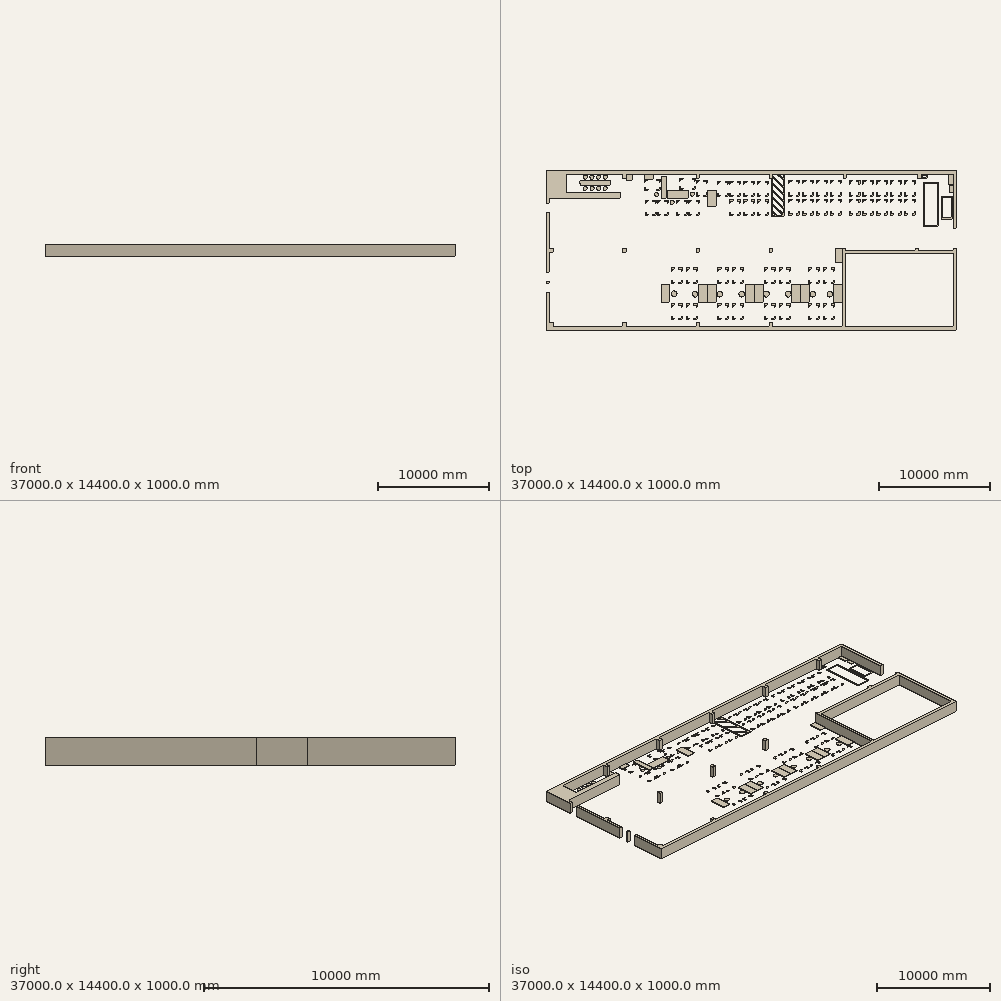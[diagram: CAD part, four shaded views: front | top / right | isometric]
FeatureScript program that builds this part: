
annotation { "Feature Type Name" : "Feature", "Feature Type Description" : "" }
export const myFeature = defineFeature(function(context is Context, id is Id, definition is map)
    precondition{}
    {
        {
            var Q0;
            Q0=qCreatedBy(makeId("Top.planeOp"),FACE);
            var sketch = newSketch(context, id + "F0", { "sketchPlane" : qUnion([Q0])});
            skLineSegment(sketch, "E0.bottom", {"start": v(-16600, 6700) * mm, "end": v(-16300, 6700) * mm});
            skLineSegment(sketch, "E0.top", {"start": v(-16600, 6300) * mm, "end": v(-16300, 6300) * mm});
            skLineSegment(sketch, "E0.left", {"start": v(-16600, 6700) * mm, "end": v(-16600, 6300) * mm});
            skLineSegment(sketch, "E0.right", {"start": v(-16300, 6700) * mm, "end": v(-16300, 6300) * mm});
            skLineSegment(sketch, "E1.1.0.0", {"start": v(-22900, 6700) * mm, "end": v(-22900, 6300) * mm});
            skLineSegment(sketch, "E1.1.0.1", {"start": v(-23200, 6700) * mm, "end": v(-23200, 6300) * mm});
            skLineSegment(sketch, "E1.1.0.2", {"start": v(-23200, 6700) * mm, "end": v(-22900, 6700) * mm});
            skLineSegment(sketch, "E1.1.0.3", {"start": v(-23200, 6300) * mm, "end": v(-22900, 6300) * mm});
            skLineSegment(sketch, "E1.2.0.0", {"start": v(-29500, 6700) * mm, "end": v(-29500, 6300) * mm});
            skLineSegment(sketch, "E1.2.0.1", {"start": v(-29800, 6700) * mm, "end": v(-29800, 6300) * mm});
            skLineSegment(sketch, "E1.2.0.2", {"start": v(-29800, 6700) * mm, "end": v(-29500, 6700) * mm});
            skLineSegment(sketch, "E1.2.0.3", {"start": v(-29800, 6300) * mm, "end": v(-29500, 6300) * mm});
            skLineSegment(sketch, "E1.3.0.0", {"start": v(-36100, 6700) * mm, "end": v(-36100, 6300) * mm});
            skLineSegment(sketch, "E1.3.0.1", {"start": v(-36400, 6700) * mm, "end": v(-36400, 6300) * mm});
            skLineSegment(sketch, "E1.3.0.2", {"start": v(-36400, 6700) * mm, "end": v(-36100, 6700) * mm});
            skLineSegment(sketch, "E1.3.0.3", {"start": v(-36400, 6300) * mm, "end": v(-36100, 6300) * mm});
            skLineSegment(sketch, "E2", {"start": v(-36400, 6700) * mm, "end": v(-36400, 9900) * mm});
            skLineSegment(sketch, "E3.left", {"start": v(-36400, 10700) * mm, "end": v(-36400, 11200) * mm});
            skLineSegment(sketch, "E4.0.1.0", {"start": v(-36400, -400) * mm, "end": v(-36100, -400) * mm});
            skLineSegment(sketch, "E4.0.1.1", {"start": v(-36400, 0) * mm, "end": v(-36400, -400) * mm});
            skLineSegment(sketch, "E4.0.1.2", {"start": v(-36400, 0) * mm, "end": v(-36100, 0) * mm});
            skLineSegment(sketch, "E4.0.1.3", {"start": v(-36100, 0) * mm, "end": v(-36100, -400) * mm});
            skLineSegment(sketch, "E4.0.1.4", {"start": v(-29800, 0) * mm, "end": v(-29500, 0) * mm});
            skLineSegment(sketch, "E4.0.1.5", {"start": v(-29800, 0) * mm, "end": v(-29800, -400) * mm});
            skLineSegment(sketch, "E4.0.1.6", {"start": v(-29800, -400) * mm, "end": v(-29500, -400) * mm});
            skLineSegment(sketch, "E4.0.1.7", {"start": v(-29500, 0) * mm, "end": v(-29500, -400) * mm});
            skLineSegment(sketch, "E4.0.1.8", {"start": v(-22900, 0) * mm, "end": v(-22900, -400) * mm});
            skLineSegment(sketch, "E4.0.1.9", {"start": v(-23200, 0) * mm, "end": v(-23200, -400) * mm});
            skLineSegment(sketch, "E4.0.1.10", {"start": v(-23200, 0) * mm, "end": v(-22900, 0) * mm});
            skLineSegment(sketch, "E4.0.1.11", {"start": v(-23200, -400) * mm, "end": v(-22900, -400) * mm});
            skLineSegment(sketch, "E4.0.1.12", {"start": v(-16600, 0) * mm, "end": v(-16300, 0) * mm});
            skLineSegment(sketch, "E4.0.1.13", {"start": v(-16600, -400) * mm, "end": v(-16300, -400) * mm});
            skLineSegment(sketch, "E4.0.1.14", {"start": v(-16600, 0) * mm, "end": v(-16600, -400) * mm});
            skLineSegment(sketch, "E4.0.1.15", {"start": v(-16300, 0) * mm, "end": v(-16300, -400) * mm});
            skLineSegment(sketch, "E5", {"start": v(-36400, -400) * mm, "end": v(0, -400) * mm});
            skLineSegment(sketch, "E6.bottom", {"start": v(0, -400) * mm, "end": v(-10000, -400) * mm});
            skLineSegment(sketch, "E6.left", {"start": v(0, -400) * mm, "end": v(0, 6300) * mm});
            skLineSegment(sketch, "E6.right", {"start": v(-10000, -400) * mm, "end": v(-10000, 6300) * mm});
            skLineSegment(sketch, "E7.0.1.0", {"start": v(-29800, 13400) * mm, "end": v(-29500, 13400) * mm});
            skLineSegment(sketch, "E7.0.1.1", {"start": v(-29800, 13400) * mm, "end": v(-29800, 13000) * mm});
            skLineSegment(sketch, "E7.0.1.2", {"start": v(-16600, 13000) * mm, "end": v(-16300, 13000) * mm});
            skLineSegment(sketch, "E7.0.1.3", {"start": v(-29800, 13000) * mm, "end": v(-29500, 13000) * mm});
            skLineSegment(sketch, "E7.0.1.4", {"start": v(-36100, 13400) * mm, "end": v(-36100, 13000) * mm});
            skLineSegment(sketch, "E7.0.1.5", {"start": v(-23200, 13000) * mm, "end": v(-22900, 13000) * mm});
            skLineSegment(sketch, "E7.0.1.6", {"start": v(-29500, 13400) * mm, "end": v(-29500, 13000) * mm});
            skLineSegment(sketch, "E7.0.1.7", {"start": v(-23200, 13400) * mm, "end": v(-22900, 13400) * mm});
            skLineSegment(sketch, "E7.0.1.8", {"start": v(-23200, 13400) * mm, "end": v(-23200, 13000) * mm});
            skLineSegment(sketch, "E7.0.1.9", {"start": v(-22900, 13400) * mm, "end": v(-22900, 13000) * mm});
            skLineSegment(sketch, "E7.0.1.10", {"start": v(-16300, 13400) * mm, "end": v(-16300, 13000) * mm});
            skLineSegment(sketch, "E7.0.1.11", {"start": v(-16600, 13400) * mm, "end": v(-16300, 13400) * mm});
            skLineSegment(sketch, "E7.0.1.12", {"start": v(-16600, 13400) * mm, "end": v(-16600, 13000) * mm});
            skLineSegment(sketch, "E7.0.1.13", {"start": v(-36400, 13400) * mm, "end": v(-36100, 13400) * mm});
            skLineSegment(sketch, "E7.0.1.14", {"start": v(-36400, 13400) * mm, "end": v(-36400, 13000) * mm});
            skLineSegment(sketch, "E7.0.1.16", {"start": v(-36400, 13000) * mm, "end": v(-36100, 13000) * mm});
            skLineSegment(sketch, "E8.bottom", {"start": v(-36400, 13400) * mm, "end": v(-34900, 13400) * mm});
            skLineSegment(sketch, "E8.top", {"start": v(-36400, 11200) * mm, "end": v(-34900, 11200) * mm});
            skLineSegment(sketch, "E8.left", {"start": v(-36400, 13400) * mm, "end": v(-36400, 11200) * mm});
            skLineSegment(sketch, "E8.right", {"start": v(-34900, 13400) * mm, "end": v(-34900, 11200) * mm});
            skLineSegment(sketch, "E9.bottom", {"start": v(-34900, 11200) * mm, "end": v(-30000, 11200) * mm});
            skLineSegment(sketch, "E9.top", {"start": v(-34900, 11700) * mm, "end": v(-30000, 11700) * mm});
            skLineSegment(sketch, "E9.left", {"start": v(-34900, 11200) * mm, "end": v(-34900, 11700) * mm});
            skLineSegment(sketch, "E9.right", {"start": v(-30000, 11200) * mm, "end": v(-30000, 11700) * mm});
            skLineSegment(sketch, "E10", {"start": v(-34900, 13400) * mm, "end": v(0, 13400) * mm});
            skLineSegment(sketch, "E11", {"start": v(0, 13400) * mm, "end": v(0, 8500) * mm});
            skLineSegment(sketch, "E12.1.0.0", {"start": v(-9600, 13400) * mm, "end": v(-9600, 13000) * mm});
            skLineSegment(sketch, "E12.1.0.1", {"start": v(-9900, 13000) * mm, "end": v(-9600, 13000) * mm});
            skLineSegment(sketch, "E12.1.0.2", {"start": v(-9900, 13400) * mm, "end": v(-9900, 13000) * mm});
            skLineSegment(sketch, "E12.1.0.3", {"start": v(-9900, 13400) * mm, "end": v(-9600, 13400) * mm});
            skLineSegment(sketch, "E12.2.0.0", {"start": v(-2900, 13400) * mm, "end": v(-2900, 13000) * mm});
            skLineSegment(sketch, "E12.2.0.1", {"start": v(-3200, 13000) * mm, "end": v(-2900, 13000) * mm});
            skLineSegment(sketch, "E12.2.0.2", {"start": v(-3200, 13400) * mm, "end": v(-3200, 13000) * mm});
            skLineSegment(sketch, "E12.2.0.3", {"start": v(-3200, 13400) * mm, "end": v(-2900, 13400) * mm});
            skLineSegment(sketch, "E13", {"start": v(-36400, 6300) * mm, "end": v(-36400, 4500) * mm});
            skLineSegment(sketch, "E14", {"start": v(-36400, 3700) * mm, "end": v(-36400, 3500) * mm});
            skLineSegment(sketch, "E15", {"start": v(-36400, 0) * mm, "end": v(-36400, 2700) * mm});
            skLineSegment(sketch, "E16.1.0.0", {"start": v(-10000, 6700) * mm, "end": v(-10000, 6300) * mm});
            skLineSegment(sketch, "E16.1.0.1", {"start": v(-10000, 6700) * mm, "end": v(-9700, 6700) * mm});
            skLineSegment(sketch, "E16.1.0.2", {"start": v(-9700, 6700) * mm, "end": v(-9700, 6300) * mm});
            skLineSegment(sketch, "E16.1.0.3", {"start": v(-10000, 6300) * mm, "end": v(-9700, 6300) * mm});
            skLineSegment(sketch, "E16.2.0.0", {"start": v(-3400, 6700) * mm, "end": v(-3400, 6300) * mm});
            skLineSegment(sketch, "E16.2.0.1", {"start": v(-3400, 6700) * mm, "end": v(-3100, 6700) * mm});
            skLineSegment(sketch, "E16.2.0.2", {"start": v(-3100, 6700) * mm, "end": v(-3100, 6300) * mm});
            skLineSegment(sketch, "E16.2.0.3", {"start": v(-3400, 6300) * mm, "end": v(-3100, 6300) * mm});
            skLineSegment(sketch, "E17.0", {"start": v(-36700, 13700) * mm, "end": v(300, 13700) * mm});
            skLineSegment(sketch, "E18", {"start": v(-36700, 13700) * mm, "end": v(-36700, 10700) * mm});
            skLineSegment(sketch, "E19", {"start": v(-36700, 10700) * mm, "end": v(-36400, 10700) * mm});
            skLineSegment(sketch, "E20", {"start": v(-36400, 9900) * mm, "end": v(-36700, 9900) * mm});
            skLineSegment(sketch, "E21", {"start": v(-36700, 9900) * mm, "end": v(-36700, 4500) * mm});
            skLineSegment(sketch, "E22", {"start": v(-36400, 3700) * mm, "end": v(-36700, 3700) * mm});
            skLineSegment(sketch, "E23", {"start": v(-36700, 3700) * mm, "end": v(-36700, 3500) * mm});
            skLineSegment(sketch, "E24", {"start": v(-36700, 3500) * mm, "end": v(-36400, 3500) * mm});
            skLineSegment(sketch, "E25", {"start": v(-36400, 2700) * mm, "end": v(-36700, 2700) * mm});
            skLineSegment(sketch, "E26", {"start": v(-36700, 2700) * mm, "end": v(-36700, -700) * mm});
            skLineSegment(sketch, "E27", {"start": v(-36700, -700) * mm, "end": v(300, -700) * mm});
            skLineSegment(sketch, "E28", {"start": v(300, -700) * mm, "end": v(300, 6300) * mm});
            skLineSegment(sketch, "E29", {"start": v(-36700, 4500) * mm, "end": v(-36400, 4500) * mm});
            skLineSegment(sketch, "E30", {"start": v(300, 13700) * mm, "end": v(300, 8500) * mm});
            skLineSegment(sketch, "E31", {"start": v(0, 8500) * mm, "end": v(300, 8500) * mm});
            skLineSegment(sketch, "E32.top", {"start": v(0, 6700) * mm, "end": v(300, 6700) * mm});
            skLineSegment(sketch, "E32.left", {"start": v(0, 6300) * mm, "end": v(0, 6700) * mm});
            skLineSegment(sketch, "E32.right", {"start": v(300, 6300) * mm, "end": v(300, 6700) * mm});
            skLineSegment(sketch, "E33", {"start": v(-9700, -400) * mm, "end": v(-9700, 6200) * mm});
            skLineSegment(sketch, "E34", {"start": v(-9700, 6200) * mm, "end": v(0, 6200) * mm});
            skLineSegment(sketch, "E35", {"start": v(-9700, 6500) * mm, "end": v(-3400, 6500) * mm});
            skLineSegment(sketch, "E36", {"start": v(-3100, 6500) * mm, "end": v(0, 6500) * mm});
            skSolve(sketch);
        }
        {
            var Q0;
            {var subQ0=sQuery(id+"F0.wireOp",EDGE,"E7.0.1.4");Q0=makeQuery(id+"F0.imprint","IMPRINT",FACE,{"disambiguationData":[TD([[makeQuery(id+"F0.imprint","IMPRINT",EDGE,{"derivedFrom":subQ0}),-1.0]])]});}
            var Q1;
            {var subQ1=sQuery(id+"F0.wireOp",EDGE,"E7.0.1.4");Q1=makeQuery(id+"F0.imprint","IMPRINT",FACE,{"disambiguationData":[TD([[makeQuery(id+"F0.imprint","IMPRINT",EDGE,{"derivedFrom":subQ1}),1.0]])]});}
            var Q2;
            Q2=makeQuery(id+"F0.imprint","IMPRINT",FACE,{"disambiguationData":[TD([[makeQuery(id+"F0.imprint","IMPRINT",EDGE,{"derivedFrom":sQuery(id+"F0.wireOp",EDGE,"E9.bottom")}),1.0]])]});
            var Q3;
            {var subQ0=sQuery(id+"F0.wireOp",EDGE,"E7.0.1.1");Q3=makeQuery(id+"F0.imprint","IMPRINT",FACE,{"disambiguationData":[TD([[makeQuery(id+"F0.imprint","IMPRINT",EDGE,{"derivedFrom":subQ0}),1.0]])]});}
            var Q4;
            Q4=makeQuery(id+"F0.imprint","IMPRINT",FACE,{"disambiguationData":[TD([[makeQuery(id+"F0.imprint","IMPRINT",EDGE,{"derivedFrom":sQuery(id+"F0.wireOp",EDGE,"E7.0.1.5")}),1.0]])]});
            var Q5;
            Q5=makeQuery(id+"F0.imprint","IMPRINT",FACE,{"disambiguationData":[TD([[makeQuery(id+"F0.imprint","IMPRINT",EDGE,{"derivedFrom":sQuery(id+"F0.wireOp",EDGE,"E1.1.0.0")}),-1.0]])]});
            var Q6;
            Q6=makeQuery(id+"F0.imprint","IMPRINT",FACE,{"disambiguationData":[TD([[makeQuery(id+"F0.imprint","IMPRINT",EDGE,{"derivedFrom":sQuery(id+"F0.wireOp",EDGE,"E1.2.0.0")}),-1.0]])]});
            var Q7;
            Q7=makeQuery(id+"F0.imprint","IMPRINT",FACE,{"disambiguationData":[TD([[makeQuery(id+"F0.imprint","IMPRINT",EDGE,{"derivedFrom":sQuery(id+"F0.wireOp",EDGE,"E1.3.0.0")}),-1.0]])]});
            var Q8;
            Q8=makeQuery(id+"F0.imprint","IMPRINT",FACE,{"disambiguationData":[TD([[makeQuery(id+"F0.imprint","IMPRINT",EDGE,{"derivedFrom":sQuery(id+"F0.wireOp",EDGE,"E7.0.1.2")}),1.0]])]});
            var Q9;
            Q9=makeQuery(id+"F0.imprint","IMPRINT",FACE,{"disambiguationData":[TD([[makeQuery(id+"F0.imprint","IMPRINT",EDGE,{"derivedFrom":sQuery(id+"F0.wireOp",EDGE,"E0.bottom")}),-1.0]])]});
            var Q10;
            Q10=makeQuery(id+"F0.imprint","IMPRINT",FACE,{"disambiguationData":[TD([[makeQuery(id+"F0.imprint","IMPRINT",EDGE,{"derivedFrom":sQuery(id+"F0.wireOp",EDGE,"E16.1.0.0")}),1.0]])]});
            var Q11;
            Q11=makeQuery(id+"F0.imprint","IMPRINT",FACE,{"disambiguationData":[TD([[makeQuery(id+"F0.imprint","IMPRINT",EDGE,{"derivedFrom":sQuery(id+"F0.wireOp",EDGE,"E12.1.0.0")}),-1.0]])]});
            var Q12;
            Q12=makeQuery(id+"F0.imprint","IMPRINT",FACE,{"disambiguationData":[TD([[makeQuery(id+"F0.imprint","IMPRINT",EDGE,{"derivedFrom":sQuery(id+"F0.wireOp",EDGE,"E12.2.0.0")}),-1.0]])]});
            var Q13;
            Q13=makeQuery(id+"F0.imprint","IMPRINT",FACE,{"disambiguationData":[TD([[makeQuery(id+"F0.imprint","IMPRINT",EDGE,{"derivedFrom":sQuery(id+"F0.wireOp",EDGE,"E16.2.0.0")}),1.0]])]});
            var Q14;
            Q14=makeQuery(id+"F0.imprint","IMPRINT",FACE,{"disambiguationData":[TD([[makeQuery(id+"F0.imprint","IMPRINT",EDGE,{"derivedFrom":sQuery(id+"F0.wireOp",EDGE,"E4.0.1.12")}),-1.0]])]});
            var Q15;
            {var subQ0=sQuery(id+"F0.wireOp",EDGE,"E4.0.1.8");Q15=makeQuery(id+"F0.imprint","IMPRINT",FACE,{"disambiguationData":[TD([[makeQuery(id+"F0.imprint","IMPRINT",EDGE,{"derivedFrom":subQ0}),-1.0]])]});}
            var Q16;
            Q16=makeQuery(id+"F0.imprint","IMPRINT",FACE,{"disambiguationData":[TD([[makeQuery(id+"F0.imprint","IMPRINT",EDGE,{"derivedFrom":sQuery(id+"F0.wireOp",EDGE,"E4.0.1.4")}),-1.0]])]});
            var Q17;
            {var subQ0=sQuery(id+"F0.wireOp",EDGE,"E4.0.1.1");Q17=makeQuery(id+"F0.imprint","IMPRINT",FACE,{"disambiguationData":[TD([[makeQuery(id+"F0.imprint","IMPRINT",EDGE,{"derivedFrom":subQ0}),1.0]])]});}
            var Q18;
            Q18=makeQuery(id+"F0.imprint","IMPRINT",FACE,{"disambiguationData":[TD([[makeQuery(id+"F0.imprint","IMPRINT",EDGE,{"derivedFrom":sQuery(id+"F0.wireOp",EDGE,"E1.3.0.1")}),-1.0]])]});
            var Q19;
            {var subQ7=sQuery(id+"F0.wireOp",EDGE,"E3.left");Q19=makeQuery(id+"F0.imprint","IMPRINT",FACE,{"disambiguationData":[TD([[makeQuery(id+"F0.imprint","IMPRINT",EDGE,{"derivedFrom":subQ7}),1.0]])]});}
            var Q20;
            {var subQ7=sQuery(id+"F0.wireOp",EDGE,"E4.0.1.1");Q20=makeQuery(id+"F0.imprint","IMPRINT",FACE,{"disambiguationData":[TD([[makeQuery(id+"F0.imprint","IMPRINT",EDGE,{"derivedFrom":subQ7}),-1.0]])]});}
            var Q21;
            Q21=makeQuery(id+"F0.imprint","IMPRINT",FACE,{"disambiguationData":[TD([[makeQuery(id+"F0.imprint","IMPRINT",EDGE,{"derivedFrom":sQuery(id+"F0.wireOp",EDGE,"E14")}),-1.0]])]});
            var Q22;
            {var subQ10=sQuery(id+"F0.wireOp",EDGE,"E6.right");Q22=makeQuery(id+"F0.imprint","IMPRINT",FACE,{"disambiguationData":[TD([[makeQuery(id+"F0.imprint","IMPRINT",EDGE,{"derivedFrom":subQ10}),-1.0]])]});}
            extrude(context, id + "F1", {"entities" : qUnion([Q0, Q1, Q2, Q3, Q4, Q5, Q6, Q7, Q8, Q9, Q10, Q11, Q12, Q13, Q14, Q15, Q16, Q17, Q18, Q19, Q20, Q21, Q22]), "depth" : 1000 * mm});
        }
        {
            var Q0;
            Q0=qCreatedBy(makeId("Top.planeOp"),FACE);
            var sketch = newSketch(context, id + "F2", { "sketchPlane" : qUnion([Q0])});
            skLineSegment(sketch, "E37.0.1.0", {"start": v(-4400, 12800) * mm, "end": v(-4400, 12500) * mm});
            skLineSegment(sketch, "E37.0.1.1", {"start": v(-4400, 12800) * mm, "end": v(-4100, 12800) * mm});
            skLineSegment(sketch, "E37.0.1.2", {"start": v(-4400, 11400) * mm, "end": v(-4100, 11400) * mm});
            skLineSegment(sketch, "E37.0.1.3", {"start": v(-3400, 12800) * mm, "end": v(-3400, 12500) * mm});
            skLineSegment(sketch, "E38.bottom", {"start": v(-400, 13400.06) * mm, "end": v(0, 13400.06) * mm});
            skLineSegment(sketch, "E38.top", {"start": v(-400, 12500.06) * mm, "end": v(0, 12500.06) * mm});
            skLineSegment(sketch, "E38.left", {"start": v(-400, 13400.06) * mm, "end": v(-400, 12500.06) * mm});
            skLineSegment(sketch, "E38.right", {"start": v(0, 13400.06) * mm, "end": v(0, 12500.06) * mm});
            skLineSegment(sketch, "E39.bottom", {"start": v(-2691.77, 12623.56) * mm, "end": v(-1291.77, 12623.56) * mm});
            skLineSegment(sketch, "E39.top", {"start": v(-2691.77, 8623.56) * mm, "end": v(-1291.77, 8623.56) * mm});
            skLineSegment(sketch, "E39.left", {"start": v(-2691.77, 12623.56) * mm, "end": v(-2691.77, 8623.56) * mm});
            skLineSegment(sketch, "E39.right", {"start": v(-1291.77, 12623.56) * mm, "end": v(-1291.77, 8623.56) * mm});
            skLineSegment(sketch, "E40.bottom", {"start": v(-1078.64, 11342.13) * mm, "end": v(-78.64, 11342.13) * mm});
            skLineSegment(sketch, "E40.top", {"start": v(-1078.64, 9342.13) * mm, "end": v(-78.64, 9342.13) * mm});
            skLineSegment(sketch, "E40.left", {"start": v(-1078.64, 11342.13) * mm, "end": v(-1078.64, 9342.13) * mm});
            skLineSegment(sketch, "E40.right", {"start": v(-78.64, 11342.13) * mm, "end": v(-78.64, 9342.13) * mm});
            skLineSegment(sketch, "E41.bottom", {"start": v(0, 12322.67) * mm, "end": v(-373.68, 12322.67) * mm});
            skLineSegment(sketch, "E41.top", {"start": v(0, 11732.57) * mm, "end": v(-373.68, 11732.57) * mm});
            skLineSegment(sketch, "E41.left", {"start": v(0, 12322.67) * mm, "end": v(0, 11732.57) * mm});
            skLineSegment(sketch, "E41.right", {"start": v(-373.68, 12322.67) * mm, "end": v(-373.68, 11732.57) * mm});
            skLineSegment(sketch, "E42.bottom", {"start": v(-2890.64, 13380.12) * mm, "end": v(-2300.62, 13380.12) * mm});
            skLineSegment(sketch, "E42.top", {"start": v(-2890.64, 12992.25) * mm, "end": v(-2300.62, 12992.25) * mm});
            skLineSegment(sketch, "E42.left", {"start": v(-2890.64, 13380.12) * mm, "end": v(-2890.64, 12992.25) * mm});
            skLineSegment(sketch, "E42.right", {"start": v(-2300.62, 13380.12) * mm, "end": v(-2300.62, 12992.25) * mm});
            skLineSegment(sketch, "E43.bottom", {"start": v(-16279.42, 13380.32) * mm, "end": v(-15279.42, 13380.32) * mm});
            skLineSegment(sketch, "E43.top", {"start": v(-16279.42, 9680.32) * mm, "end": v(-15279.42, 9680.32) * mm});
            skLineSegment(sketch, "E43.left", {"start": v(-16279.42, 13380.32) * mm, "end": v(-16279.42, 9680.32) * mm});
            skLineSegment(sketch, "E43.right", {"start": v(-15279.42, 13380.32) * mm, "end": v(-15279.42, 9680.32) * mm});
            skLineSegment(sketch, "E44", {"start": v(-4400, 12500) * mm, "end": v(-4300, 12500) * mm});
            skLineSegment(sketch, "E45", {"start": v(-4300, 12500) * mm, "end": v(-4300, 12700) * mm});
            skLineSegment(sketch, "E46", {"start": v(-4300, 12700) * mm, "end": v(-4100, 12700) * mm});
            skLineSegment(sketch, "E47", {"start": v(-4100, 12700) * mm, "end": v(-4100, 12800) * mm});
            skLineSegment(sketch, "E48.MirrorCS", {"start": v(-3700, 12700) * mm, "end": v(-3700, 12800) * mm});
            skLineSegment(sketch, "E49.MirrorCS", {"start": v(-3500, 12700) * mm, "end": v(-3700, 12700) * mm});
            skLineSegment(sketch, "E50.MirrorCS", {"start": v(-3500, 12500) * mm, "end": v(-3500, 12700) * mm});
            skLineSegment(sketch, "E51.MirrorCS", {"start": v(-3400, 12500) * mm, "end": v(-3500, 12500) * mm});
            skLineSegment(sketch, "E52.MirrorCS", {"start": v(-4400, 11700) * mm, "end": v(-4300, 11700) * mm});
            skLineSegment(sketch, "E53.MirrorCS", {"start": v(-4300, 11700) * mm, "end": v(-4300, 11500) * mm});
            skLineSegment(sketch, "E54.MirrorCS", {"start": v(-4300, 11500) * mm, "end": v(-4100, 11500) * mm});
            skLineSegment(sketch, "E55.MirrorCS", {"start": v(-4100, 11500) * mm, "end": v(-4100, 11400) * mm});
            skLineSegment(sketch, "E56.MirrorCS", {"start": v(-3700, 11500) * mm, "end": v(-3700, 11400) * mm});
            skLineSegment(sketch, "E57.MirrorCS", {"start": v(-3500, 11500) * mm, "end": v(-3700, 11500) * mm});
            skLineSegment(sketch, "E58.MirrorCS", {"start": v(-3500, 11700) * mm, "end": v(-3500, 11500) * mm});
            skLineSegment(sketch, "E59.MirrorCS", {"start": v(-3400, 11700) * mm, "end": v(-3500, 11700) * mm});
            skLineSegment(sketch, "E60.trimOffspring", {"start": v(-4400, 11700) * mm, "end": v(-4400, 11400) * mm});
            skLineSegment(sketch, "E61.trimOffspring", {"start": v(-3700, 12800) * mm, "end": v(-3400, 12800) * mm});
            skLineSegment(sketch, "E62.trimOffspring", {"start": v(-3400, 11700) * mm, "end": v(-3400, 11400) * mm});
            skLineSegment(sketch, "E63.trimOffspring", {"start": v(-3700, 11400) * mm, "end": v(-3400, 11400) * mm});
            skLineSegment(sketch, "E64.0.1.0", {"start": v(-3700, 11100) * mm, "end": v(-3400, 11100) * mm});
            skLineSegment(sketch, "E64.0.1.1", {"start": v(-3700, 9700) * mm, "end": v(-3400, 9700) * mm});
            skLineSegment(sketch, "E64.0.1.2", {"start": v(-4400, 10000) * mm, "end": v(-4400, 9700) * mm});
            skLineSegment(sketch, "E64.0.1.3", {"start": v(-4400, 9700) * mm, "end": v(-4100, 9700) * mm});
            skLineSegment(sketch, "E64.0.1.4", {"start": v(-3400, 10000) * mm, "end": v(-3400, 9700) * mm});
            skLineSegment(sketch, "E64.0.1.5", {"start": v(-3400, 11100) * mm, "end": v(-3400, 10800) * mm});
            skLineSegment(sketch, "E64.0.1.6", {"start": v(-4400, 11100) * mm, "end": v(-4400, 10800) * mm});
            skLineSegment(sketch, "E64.0.1.7", {"start": v(-4400, 11100) * mm, "end": v(-4100, 11100) * mm});
            skLineSegment(sketch, "E64.0.1.8", {"start": v(-4300, 9800) * mm, "end": v(-4100, 9800) * mm});
            skLineSegment(sketch, "E64.0.1.9", {"start": v(-3400, 10000) * mm, "end": v(-3500, 10000) * mm});
            skLineSegment(sketch, "E64.0.1.10", {"start": v(-3700, 9800) * mm, "end": v(-3700, 9700) * mm});
            skLineSegment(sketch, "E64.0.1.11", {"start": v(-3500, 11000) * mm, "end": v(-3700, 11000) * mm});
            skLineSegment(sketch, "E64.0.1.12", {"start": v(-4400, 10800) * mm, "end": v(-4300, 10800) * mm});
            skLineSegment(sketch, "E64.0.1.13", {"start": v(-4300, 11000) * mm, "end": v(-4100, 11000) * mm});
            skLineSegment(sketch, "E64.0.1.14", {"start": v(-4400, 10000) * mm, "end": v(-4300, 10000) * mm});
            skLineSegment(sketch, "E64.0.1.15", {"start": v(-3700, 11000) * mm, "end": v(-3700, 11100) * mm});
            skLineSegment(sketch, "E64.0.1.16", {"start": v(-4100, 9800) * mm, "end": v(-4100, 9700) * mm});
            skLineSegment(sketch, "E64.0.1.17", {"start": v(-4300, 10000) * mm, "end": v(-4300, 9800) * mm});
            skLineSegment(sketch, "E64.0.1.18", {"start": v(-4300, 10800) * mm, "end": v(-4300, 11000) * mm});
            skLineSegment(sketch, "E64.0.1.19", {"start": v(-3500, 9800) * mm, "end": v(-3700, 9800) * mm});
            skLineSegment(sketch, "E64.0.1.20", {"start": v(-4100, 11000) * mm, "end": v(-4100, 11100) * mm});
            skLineSegment(sketch, "E64.0.1.21", {"start": v(-3400, 10800) * mm, "end": v(-3500, 10800) * mm});
            skLineSegment(sketch, "E64.0.1.22", {"start": v(-3500, 10000) * mm, "end": v(-3500, 9800) * mm});
            skLineSegment(sketch, "E64.0.1.23", {"start": v(-3500, 10800) * mm, "end": v(-3500, 11000) * mm});
            skLineSegment(sketch, "E64.1.0.0", {"start": v(-4950, 12800) * mm, "end": v(-4650, 12800) * mm});
            skLineSegment(sketch, "E64.1.0.1", {"start": v(-4950, 11400) * mm, "end": v(-4650, 11400) * mm});
            skLineSegment(sketch, "E64.1.0.2", {"start": v(-5650, 11700) * mm, "end": v(-5650, 11400) * mm});
            skLineSegment(sketch, "E64.1.0.3", {"start": v(-5650, 11400) * mm, "end": v(-5350, 11400) * mm});
            skLineSegment(sketch, "E64.1.0.4", {"start": v(-4650, 11700) * mm, "end": v(-4650, 11400) * mm});
            skLineSegment(sketch, "E64.1.0.5", {"start": v(-4650, 12800) * mm, "end": v(-4650, 12500) * mm});
            skLineSegment(sketch, "E64.1.0.6", {"start": v(-5650, 12800) * mm, "end": v(-5650, 12500) * mm});
            skLineSegment(sketch, "E64.1.0.7", {"start": v(-5650, 12800) * mm, "end": v(-5350, 12800) * mm});
            skLineSegment(sketch, "E64.1.0.8", {"start": v(-5550, 11500) * mm, "end": v(-5350, 11500) * mm});
            skLineSegment(sketch, "E64.1.0.9", {"start": v(-4650, 11700) * mm, "end": v(-4750, 11700) * mm});
            skLineSegment(sketch, "E64.1.0.10", {"start": v(-4950, 11500) * mm, "end": v(-4950, 11400) * mm});
            skLineSegment(sketch, "E64.1.0.11", {"start": v(-4750, 12700) * mm, "end": v(-4950, 12700) * mm});
            skLineSegment(sketch, "E64.1.0.12", {"start": v(-5650, 12500) * mm, "end": v(-5550, 12500) * mm});
            skLineSegment(sketch, "E64.1.0.13", {"start": v(-5550, 12700) * mm, "end": v(-5350, 12700) * mm});
            skLineSegment(sketch, "E64.1.0.14", {"start": v(-5650, 11700) * mm, "end": v(-5550, 11700) * mm});
            skLineSegment(sketch, "E64.1.0.15", {"start": v(-4950, 12700) * mm, "end": v(-4950, 12800) * mm});
            skLineSegment(sketch, "E64.1.0.16", {"start": v(-5350, 11500) * mm, "end": v(-5350, 11400) * mm});
            skLineSegment(sketch, "E64.1.0.17", {"start": v(-5550, 11700) * mm, "end": v(-5550, 11500) * mm});
            skLineSegment(sketch, "E64.1.0.18", {"start": v(-5550, 12500) * mm, "end": v(-5550, 12700) * mm});
            skLineSegment(sketch, "E64.1.0.19", {"start": v(-4750, 11500) * mm, "end": v(-4950, 11500) * mm});
            skLineSegment(sketch, "E64.1.0.20", {"start": v(-5350, 12700) * mm, "end": v(-5350, 12800) * mm});
            skLineSegment(sketch, "E64.1.0.21", {"start": v(-4650, 12500) * mm, "end": v(-4750, 12500) * mm});
            skLineSegment(sketch, "E64.1.0.22", {"start": v(-4750, 11700) * mm, "end": v(-4750, 11500) * mm});
            skLineSegment(sketch, "E64.1.0.23", {"start": v(-4750, 12500) * mm, "end": v(-4750, 12700) * mm});
            skLineSegment(sketch, "E64.1.1.0", {"start": v(-4950, 11100) * mm, "end": v(-4650, 11100) * mm});
            skLineSegment(sketch, "E64.1.1.1", {"start": v(-4950, 9700) * mm, "end": v(-4650, 9700) * mm});
            skLineSegment(sketch, "E64.1.1.2", {"start": v(-5650, 10000) * mm, "end": v(-5650, 9700) * mm});
            skLineSegment(sketch, "E64.1.1.3", {"start": v(-5650, 9700) * mm, "end": v(-5350, 9700) * mm});
            skLineSegment(sketch, "E64.1.1.4", {"start": v(-4650, 10000) * mm, "end": v(-4650, 9700) * mm});
            skLineSegment(sketch, "E64.1.1.5", {"start": v(-4650, 11100) * mm, "end": v(-4650, 10800) * mm});
            skLineSegment(sketch, "E64.1.1.6", {"start": v(-5650, 11100) * mm, "end": v(-5650, 10800) * mm});
            skLineSegment(sketch, "E64.1.1.7", {"start": v(-5650, 11100) * mm, "end": v(-5350, 11100) * mm});
            skLineSegment(sketch, "E64.1.1.8", {"start": v(-5550, 9800) * mm, "end": v(-5350, 9800) * mm});
            skLineSegment(sketch, "E64.1.1.9", {"start": v(-4650, 10000) * mm, "end": v(-4750, 10000) * mm});
            skLineSegment(sketch, "E64.1.1.10", {"start": v(-4950, 9800) * mm, "end": v(-4950, 9700) * mm});
            skLineSegment(sketch, "E64.1.1.11", {"start": v(-4750, 11000) * mm, "end": v(-4950, 11000) * mm});
            skLineSegment(sketch, "E64.1.1.12", {"start": v(-5650, 10800) * mm, "end": v(-5550, 10800) * mm});
            skLineSegment(sketch, "E64.1.1.13", {"start": v(-5550, 11000) * mm, "end": v(-5350, 11000) * mm});
            skLineSegment(sketch, "E64.1.1.14", {"start": v(-5650, 10000) * mm, "end": v(-5550, 10000) * mm});
            skLineSegment(sketch, "E64.1.1.15", {"start": v(-4950, 11000) * mm, "end": v(-4950, 11100) * mm});
            skLineSegment(sketch, "E64.1.1.16", {"start": v(-5350, 9800) * mm, "end": v(-5350, 9700) * mm});
            skLineSegment(sketch, "E64.1.1.17", {"start": v(-5550, 10000) * mm, "end": v(-5550, 9800) * mm});
            skLineSegment(sketch, "E64.1.1.18", {"start": v(-5550, 10800) * mm, "end": v(-5550, 11000) * mm});
            skLineSegment(sketch, "E64.1.1.19", {"start": v(-4750, 9800) * mm, "end": v(-4950, 9800) * mm});
            skLineSegment(sketch, "E64.1.1.20", {"start": v(-5350, 11000) * mm, "end": v(-5350, 11100) * mm});
            skLineSegment(sketch, "E64.1.1.21", {"start": v(-4650, 10800) * mm, "end": v(-4750, 10800) * mm});
            skLineSegment(sketch, "E64.1.1.22", {"start": v(-4750, 10000) * mm, "end": v(-4750, 9800) * mm});
            skLineSegment(sketch, "E64.1.1.23", {"start": v(-4750, 10800) * mm, "end": v(-4750, 11000) * mm});
            skLineSegment(sketch, "E64.2.0.0", {"start": v(-6200, 12800) * mm, "end": v(-5900, 12800) * mm});
            skLineSegment(sketch, "E64.2.0.1", {"start": v(-6200, 11400) * mm, "end": v(-5900, 11400) * mm});
            skLineSegment(sketch, "E64.2.0.2", {"start": v(-6900, 11700) * mm, "end": v(-6900, 11400) * mm});
            skLineSegment(sketch, "E64.2.0.3", {"start": v(-6900, 11400) * mm, "end": v(-6600, 11400) * mm});
            skLineSegment(sketch, "E64.2.0.4", {"start": v(-5900, 11700) * mm, "end": v(-5900, 11400) * mm});
            skLineSegment(sketch, "E64.2.0.5", {"start": v(-5900, 12800) * mm, "end": v(-5900, 12500) * mm});
            skLineSegment(sketch, "E64.2.0.6", {"start": v(-6900, 12800) * mm, "end": v(-6900, 12500) * mm});
            skLineSegment(sketch, "E64.2.0.7", {"start": v(-6900, 12800) * mm, "end": v(-6600, 12800) * mm});
            skLineSegment(sketch, "E64.2.0.8", {"start": v(-6800, 11500) * mm, "end": v(-6600, 11500) * mm});
            skLineSegment(sketch, "E64.2.0.9", {"start": v(-5900, 11700) * mm, "end": v(-6000, 11700) * mm});
            skLineSegment(sketch, "E64.2.0.10", {"start": v(-6200, 11500) * mm, "end": v(-6200, 11400) * mm});
            skLineSegment(sketch, "E64.2.0.11", {"start": v(-6000, 12700) * mm, "end": v(-6200, 12700) * mm});
            skLineSegment(sketch, "E64.2.0.12", {"start": v(-6900, 12500) * mm, "end": v(-6800, 12500) * mm});
            skLineSegment(sketch, "E64.2.0.13", {"start": v(-6800, 12700) * mm, "end": v(-6600, 12700) * mm});
            skLineSegment(sketch, "E64.2.0.14", {"start": v(-6900, 11700) * mm, "end": v(-6800, 11700) * mm});
            skLineSegment(sketch, "E64.2.0.15", {"start": v(-6200, 12700) * mm, "end": v(-6200, 12800) * mm});
            skLineSegment(sketch, "E64.2.0.16", {"start": v(-6600, 11500) * mm, "end": v(-6600, 11400) * mm});
            skLineSegment(sketch, "E64.2.0.17", {"start": v(-6800, 11700) * mm, "end": v(-6800, 11500) * mm});
            skLineSegment(sketch, "E64.2.0.18", {"start": v(-6800, 12500) * mm, "end": v(-6800, 12700) * mm});
            skLineSegment(sketch, "E64.2.0.19", {"start": v(-6000, 11500) * mm, "end": v(-6200, 11500) * mm});
            skLineSegment(sketch, "E64.2.0.20", {"start": v(-6600, 12700) * mm, "end": v(-6600, 12800) * mm});
            skLineSegment(sketch, "E64.2.0.21", {"start": v(-5900, 12500) * mm, "end": v(-6000, 12500) * mm});
            skLineSegment(sketch, "E64.2.0.22", {"start": v(-6000, 11700) * mm, "end": v(-6000, 11500) * mm});
            skLineSegment(sketch, "E64.2.0.23", {"start": v(-6000, 12500) * mm, "end": v(-6000, 12700) * mm});
            skLineSegment(sketch, "E64.2.1.0", {"start": v(-6200, 11100) * mm, "end": v(-5900, 11100) * mm});
            skLineSegment(sketch, "E64.2.1.1", {"start": v(-6200, 9700) * mm, "end": v(-5900, 9700) * mm});
            skLineSegment(sketch, "E64.2.1.2", {"start": v(-6900, 10000) * mm, "end": v(-6900, 9700) * mm});
            skLineSegment(sketch, "E64.2.1.3", {"start": v(-6900, 9700) * mm, "end": v(-6600, 9700) * mm});
            skLineSegment(sketch, "E64.2.1.4", {"start": v(-5900, 10000) * mm, "end": v(-5900, 9700) * mm});
            skLineSegment(sketch, "E64.2.1.5", {"start": v(-5900, 11100) * mm, "end": v(-5900, 10800) * mm});
            skLineSegment(sketch, "E64.2.1.6", {"start": v(-6900, 11100) * mm, "end": v(-6900, 10800) * mm});
            skLineSegment(sketch, "E64.2.1.7", {"start": v(-6900, 11100) * mm, "end": v(-6600, 11100) * mm});
            skLineSegment(sketch, "E64.2.1.8", {"start": v(-6800, 9800) * mm, "end": v(-6600, 9800) * mm});
            skLineSegment(sketch, "E64.2.1.9", {"start": v(-5900, 10000) * mm, "end": v(-6000, 10000) * mm});
            skLineSegment(sketch, "E64.2.1.10", {"start": v(-6200, 9800) * mm, "end": v(-6200, 9700) * mm});
            skLineSegment(sketch, "E64.2.1.11", {"start": v(-6000, 11000) * mm, "end": v(-6200, 11000) * mm});
            skLineSegment(sketch, "E64.2.1.12", {"start": v(-6900, 10800) * mm, "end": v(-6800, 10800) * mm});
            skLineSegment(sketch, "E64.2.1.13", {"start": v(-6800, 11000) * mm, "end": v(-6600, 11000) * mm});
            skLineSegment(sketch, "E64.2.1.14", {"start": v(-6900, 10000) * mm, "end": v(-6800, 10000) * mm});
            skLineSegment(sketch, "E64.2.1.15", {"start": v(-6200, 11000) * mm, "end": v(-6200, 11100) * mm});
            skLineSegment(sketch, "E64.2.1.16", {"start": v(-6600, 9800) * mm, "end": v(-6600, 9700) * mm});
            skLineSegment(sketch, "E64.2.1.17", {"start": v(-6800, 10000) * mm, "end": v(-6800, 9800) * mm});
            skLineSegment(sketch, "E64.2.1.18", {"start": v(-6800, 10800) * mm, "end": v(-6800, 11000) * mm});
            skLineSegment(sketch, "E64.2.1.19", {"start": v(-6000, 9800) * mm, "end": v(-6200, 9800) * mm});
            skLineSegment(sketch, "E64.2.1.20", {"start": v(-6600, 11000) * mm, "end": v(-6600, 11100) * mm});
            skLineSegment(sketch, "E64.2.1.21", {"start": v(-5900, 10800) * mm, "end": v(-6000, 10800) * mm});
            skLineSegment(sketch, "E64.2.1.22", {"start": v(-6000, 10000) * mm, "end": v(-6000, 9800) * mm});
            skLineSegment(sketch, "E64.2.1.23", {"start": v(-6000, 10800) * mm, "end": v(-6000, 11000) * mm});
            skLineSegment(sketch, "E64.3.0.0", {"start": v(-7450, 12800) * mm, "end": v(-7150, 12800) * mm});
            skLineSegment(sketch, "E64.3.0.1", {"start": v(-7450, 11400) * mm, "end": v(-7150, 11400) * mm});
            skLineSegment(sketch, "E64.3.0.2", {"start": v(-8150, 11700) * mm, "end": v(-8150, 11400) * mm});
            skLineSegment(sketch, "E64.3.0.3", {"start": v(-8150, 11400) * mm, "end": v(-7850, 11400) * mm});
            skLineSegment(sketch, "E64.3.0.4", {"start": v(-7150, 11700) * mm, "end": v(-7150, 11400) * mm});
            skLineSegment(sketch, "E64.3.0.5", {"start": v(-7150, 12800) * mm, "end": v(-7150, 12500) * mm});
            skLineSegment(sketch, "E64.3.0.6", {"start": v(-8150, 12800) * mm, "end": v(-8150, 12500) * mm});
            skLineSegment(sketch, "E64.3.0.7", {"start": v(-8150, 12800) * mm, "end": v(-7850, 12800) * mm});
            skLineSegment(sketch, "E64.3.0.8", {"start": v(-8050, 11500) * mm, "end": v(-7850, 11500) * mm});
            skLineSegment(sketch, "E64.3.0.9", {"start": v(-7150, 11700) * mm, "end": v(-7250, 11700) * mm});
            skLineSegment(sketch, "E64.3.0.10", {"start": v(-7450, 11500) * mm, "end": v(-7450, 11400) * mm});
            skLineSegment(sketch, "E64.3.0.11", {"start": v(-7250, 12700) * mm, "end": v(-7450, 12700) * mm});
            skLineSegment(sketch, "E64.3.0.12", {"start": v(-8150, 12500) * mm, "end": v(-8050, 12500) * mm});
            skLineSegment(sketch, "E64.3.0.13", {"start": v(-8050, 12700) * mm, "end": v(-7850, 12700) * mm});
            skLineSegment(sketch, "E64.3.0.14", {"start": v(-8150, 11700) * mm, "end": v(-8050, 11700) * mm});
            skLineSegment(sketch, "E64.3.0.15", {"start": v(-7450, 12700) * mm, "end": v(-7450, 12800) * mm});
            skLineSegment(sketch, "E64.3.0.16", {"start": v(-7850, 11500) * mm, "end": v(-7850, 11400) * mm});
            skLineSegment(sketch, "E64.3.0.17", {"start": v(-8050, 11700) * mm, "end": v(-8050, 11500) * mm});
            skLineSegment(sketch, "E64.3.0.18", {"start": v(-8050, 12500) * mm, "end": v(-8050, 12700) * mm});
            skLineSegment(sketch, "E64.3.0.19", {"start": v(-7250, 11500) * mm, "end": v(-7450, 11500) * mm});
            skLineSegment(sketch, "E64.3.0.20", {"start": v(-7850, 12700) * mm, "end": v(-7850, 12800) * mm});
            skLineSegment(sketch, "E64.3.0.21", {"start": v(-7150, 12500) * mm, "end": v(-7250, 12500) * mm});
            skLineSegment(sketch, "E64.3.0.22", {"start": v(-7250, 11700) * mm, "end": v(-7250, 11500) * mm});
            skLineSegment(sketch, "E64.3.0.23", {"start": v(-7250, 12500) * mm, "end": v(-7250, 12700) * mm});
            skLineSegment(sketch, "E64.3.1.0", {"start": v(-7450, 11100) * mm, "end": v(-7150, 11100) * mm});
            skLineSegment(sketch, "E64.3.1.1", {"start": v(-7450, 9700) * mm, "end": v(-7150, 9700) * mm});
            skLineSegment(sketch, "E64.3.1.2", {"start": v(-8150, 10000) * mm, "end": v(-8150, 9700) * mm});
            skLineSegment(sketch, "E64.3.1.3", {"start": v(-8150, 9700) * mm, "end": v(-7850, 9700) * mm});
            skLineSegment(sketch, "E64.3.1.4", {"start": v(-7150, 10000) * mm, "end": v(-7150, 9700) * mm});
            skLineSegment(sketch, "E64.3.1.5", {"start": v(-7150, 11100) * mm, "end": v(-7150, 10800) * mm});
            skLineSegment(sketch, "E64.3.1.6", {"start": v(-8150, 11100) * mm, "end": v(-8150, 10800) * mm});
            skLineSegment(sketch, "E64.3.1.7", {"start": v(-8150, 11100) * mm, "end": v(-7850, 11100) * mm});
            skLineSegment(sketch, "E64.3.1.8", {"start": v(-8050, 9800) * mm, "end": v(-7850, 9800) * mm});
            skLineSegment(sketch, "E64.3.1.9", {"start": v(-7150, 10000) * mm, "end": v(-7250, 10000) * mm});
            skLineSegment(sketch, "E64.3.1.10", {"start": v(-7450, 9800) * mm, "end": v(-7450, 9700) * mm});
            skLineSegment(sketch, "E64.3.1.11", {"start": v(-7250, 11000) * mm, "end": v(-7450, 11000) * mm});
            skLineSegment(sketch, "E64.3.1.12", {"start": v(-8150, 10800) * mm, "end": v(-8050, 10800) * mm});
            skLineSegment(sketch, "E64.3.1.13", {"start": v(-8050, 11000) * mm, "end": v(-7850, 11000) * mm});
            skLineSegment(sketch, "E64.3.1.14", {"start": v(-8150, 10000) * mm, "end": v(-8050, 10000) * mm});
            skLineSegment(sketch, "E64.3.1.15", {"start": v(-7450, 11000) * mm, "end": v(-7450, 11100) * mm});
            skLineSegment(sketch, "E64.3.1.16", {"start": v(-7850, 9800) * mm, "end": v(-7850, 9700) * mm});
            skLineSegment(sketch, "E64.3.1.17", {"start": v(-8050, 10000) * mm, "end": v(-8050, 9800) * mm});
            skLineSegment(sketch, "E64.3.1.18", {"start": v(-8050, 10800) * mm, "end": v(-8050, 11000) * mm});
            skLineSegment(sketch, "E64.3.1.19", {"start": v(-7250, 9800) * mm, "end": v(-7450, 9800) * mm});
            skLineSegment(sketch, "E64.3.1.20", {"start": v(-7850, 11000) * mm, "end": v(-7850, 11100) * mm});
            skLineSegment(sketch, "E64.3.1.21", {"start": v(-7150, 10800) * mm, "end": v(-7250, 10800) * mm});
            skLineSegment(sketch, "E64.3.1.22", {"start": v(-7250, 10000) * mm, "end": v(-7250, 9800) * mm});
            skLineSegment(sketch, "E64.3.1.23", {"start": v(-7250, 10800) * mm, "end": v(-7250, 11000) * mm});
            skLineSegment(sketch, "E64.4.0.0", {"start": v(-8700, 12800) * mm, "end": v(-8400, 12800) * mm});
            skLineSegment(sketch, "E64.4.0.1", {"start": v(-8700, 11400) * mm, "end": v(-8400, 11400) * mm});
            skLineSegment(sketch, "E64.4.0.2", {"start": v(-9400, 11700) * mm, "end": v(-9400, 11400) * mm});
            skLineSegment(sketch, "E64.4.0.3", {"start": v(-9400, 11400) * mm, "end": v(-9100, 11400) * mm});
            skLineSegment(sketch, "E64.4.0.4", {"start": v(-8400, 11700) * mm, "end": v(-8400, 11400) * mm});
            skLineSegment(sketch, "E64.4.0.5", {"start": v(-8400, 12800) * mm, "end": v(-8400, 12500) * mm});
            skLineSegment(sketch, "E64.4.0.6", {"start": v(-9400, 12800) * mm, "end": v(-9400, 12500) * mm});
            skLineSegment(sketch, "E64.4.0.7", {"start": v(-9400, 12800) * mm, "end": v(-9100, 12800) * mm});
            skLineSegment(sketch, "E64.4.0.8", {"start": v(-9300, 11500) * mm, "end": v(-9100, 11500) * mm});
            skLineSegment(sketch, "E64.4.0.9", {"start": v(-8400, 11700) * mm, "end": v(-8500, 11700) * mm});
            skLineSegment(sketch, "E64.4.0.10", {"start": v(-8700, 11500) * mm, "end": v(-8700, 11400) * mm});
            skLineSegment(sketch, "E64.4.0.11", {"start": v(-8500, 12700) * mm, "end": v(-8700, 12700) * mm});
            skLineSegment(sketch, "E64.4.0.12", {"start": v(-9400, 12500) * mm, "end": v(-9300, 12500) * mm});
            skLineSegment(sketch, "E64.4.0.13", {"start": v(-9300, 12700) * mm, "end": v(-9100, 12700) * mm});
            skLineSegment(sketch, "E64.4.0.14", {"start": v(-9400, 11700) * mm, "end": v(-9300, 11700) * mm});
            skLineSegment(sketch, "E64.4.0.15", {"start": v(-8700, 12700) * mm, "end": v(-8700, 12800) * mm});
            skLineSegment(sketch, "E64.4.0.16", {"start": v(-9100, 11500) * mm, "end": v(-9100, 11400) * mm});
            skLineSegment(sketch, "E64.4.0.17", {"start": v(-9300, 11700) * mm, "end": v(-9300, 11500) * mm});
            skLineSegment(sketch, "E64.4.0.18", {"start": v(-9300, 12500) * mm, "end": v(-9300, 12700) * mm});
            skLineSegment(sketch, "E64.4.0.19", {"start": v(-8500, 11500) * mm, "end": v(-8700, 11500) * mm});
            skLineSegment(sketch, "E64.4.0.20", {"start": v(-9100, 12700) * mm, "end": v(-9100, 12800) * mm});
            skLineSegment(sketch, "E64.4.0.21", {"start": v(-8400, 12500) * mm, "end": v(-8500, 12500) * mm});
            skLineSegment(sketch, "E64.4.0.22", {"start": v(-8500, 11700) * mm, "end": v(-8500, 11500) * mm});
            skLineSegment(sketch, "E64.4.0.23", {"start": v(-8500, 12500) * mm, "end": v(-8500, 12700) * mm});
            skLineSegment(sketch, "E64.4.1.0", {"start": v(-8700, 11100) * mm, "end": v(-8400, 11100) * mm});
            skLineSegment(sketch, "E64.4.1.1", {"start": v(-8700, 9700) * mm, "end": v(-8400, 9700) * mm});
            skLineSegment(sketch, "E64.4.1.2", {"start": v(-9400, 10000) * mm, "end": v(-9400, 9700) * mm});
            skLineSegment(sketch, "E64.4.1.3", {"start": v(-9400, 9700) * mm, "end": v(-9100, 9700) * mm});
            skLineSegment(sketch, "E64.4.1.4", {"start": v(-8400, 10000) * mm, "end": v(-8400, 9700) * mm});
            skLineSegment(sketch, "E64.4.1.5", {"start": v(-8400, 11100) * mm, "end": v(-8400, 10800) * mm});
            skLineSegment(sketch, "E64.4.1.6", {"start": v(-9400, 11100) * mm, "end": v(-9400, 10800) * mm});
            skLineSegment(sketch, "E64.4.1.7", {"start": v(-9400, 11100) * mm, "end": v(-9100, 11100) * mm});
            skLineSegment(sketch, "E64.4.1.8", {"start": v(-9300, 9800) * mm, "end": v(-9100, 9800) * mm});
            skLineSegment(sketch, "E64.4.1.9", {"start": v(-8400, 10000) * mm, "end": v(-8500, 10000) * mm});
            skLineSegment(sketch, "E64.4.1.10", {"start": v(-8700, 9800) * mm, "end": v(-8700, 9700) * mm});
            skLineSegment(sketch, "E64.4.1.11", {"start": v(-8500, 11000) * mm, "end": v(-8700, 11000) * mm});
            skLineSegment(sketch, "E64.4.1.12", {"start": v(-9400, 10800) * mm, "end": v(-9300, 10800) * mm});
            skLineSegment(sketch, "E64.4.1.13", {"start": v(-9300, 11000) * mm, "end": v(-9100, 11000) * mm});
            skLineSegment(sketch, "E64.4.1.14", {"start": v(-9400, 10000) * mm, "end": v(-9300, 10000) * mm});
            skLineSegment(sketch, "E64.4.1.15", {"start": v(-8700, 11000) * mm, "end": v(-8700, 11100) * mm});
            skLineSegment(sketch, "E64.4.1.16", {"start": v(-9100, 9800) * mm, "end": v(-9100, 9700) * mm});
            skLineSegment(sketch, "E64.4.1.17", {"start": v(-9300, 10000) * mm, "end": v(-9300, 9800) * mm});
            skLineSegment(sketch, "E64.4.1.18", {"start": v(-9300, 10800) * mm, "end": v(-9300, 11000) * mm});
            skLineSegment(sketch, "E64.4.1.19", {"start": v(-8500, 9800) * mm, "end": v(-8700, 9800) * mm});
            skLineSegment(sketch, "E64.4.1.20", {"start": v(-9100, 11000) * mm, "end": v(-9100, 11100) * mm});
            skLineSegment(sketch, "E64.4.1.21", {"start": v(-8400, 10800) * mm, "end": v(-8500, 10800) * mm});
            skLineSegment(sketch, "E64.4.1.22", {"start": v(-8500, 10000) * mm, "end": v(-8500, 9800) * mm});
            skLineSegment(sketch, "E64.4.1.23", {"start": v(-8500, 10800) * mm, "end": v(-8500, 11000) * mm});
            skLineSegment(sketch, "E64.direction1", {"start": v(-4400, 11400) * mm, "end": v(-5650, 11400) * mm, "construction": true});
            skLineSegment(sketch, "E64.direction2", {"start": v(-4400, 11400) * mm, "end": v(-4400, 9700) * mm, "construction": true});
            skLineSegment(sketch, "E65.4.0.0", {"start": v(-10376.9, 12802.04) * mm, "end": v(-10076.9, 12802.04) * mm});
            skLineSegment(sketch, "E65.4.0.1", {"start": v(-10376.9, 11402.04) * mm, "end": v(-10076.9, 11402.04) * mm});
            skLineSegment(sketch, "E65.4.0.2", {"start": v(-11076.9, 11702.04) * mm, "end": v(-11076.9, 11402.04) * mm});
            skLineSegment(sketch, "E65.4.0.3", {"start": v(-11076.9, 11402.04) * mm, "end": v(-10776.9, 11402.04) * mm});
            skLineSegment(sketch, "E65.4.0.4", {"start": v(-10076.9, 11702.04) * mm, "end": v(-10076.9, 11402.04) * mm});
            skLineSegment(sketch, "E65.4.0.5", {"start": v(-10076.9, 12802.04) * mm, "end": v(-10076.9, 12502.04) * mm});
            skLineSegment(sketch, "E65.4.0.6", {"start": v(-11076.9, 12802.04) * mm, "end": v(-11076.9, 12502.04) * mm});
            skLineSegment(sketch, "E65.4.0.7", {"start": v(-11076.9, 12802.04) * mm, "end": v(-10776.9, 12802.04) * mm});
            skLineSegment(sketch, "E65.4.0.8", {"start": v(-10976.9, 11502.04) * mm, "end": v(-10776.9, 11502.04) * mm});
            skLineSegment(sketch, "E65.4.0.9", {"start": v(-10076.9, 11702.04) * mm, "end": v(-10176.9, 11702.04) * mm});
            skLineSegment(sketch, "E65.4.0.10", {"start": v(-10376.9, 11502.04) * mm, "end": v(-10376.9, 11402.04) * mm});
            skLineSegment(sketch, "E65.4.0.11", {"start": v(-10176.9, 12702.04) * mm, "end": v(-10376.9, 12702.04) * mm});
            skLineSegment(sketch, "E65.4.0.12", {"start": v(-11076.9, 12502.04) * mm, "end": v(-10976.9, 12502.04) * mm});
            skLineSegment(sketch, "E65.4.0.13", {"start": v(-10976.9, 12702.04) * mm, "end": v(-10776.9, 12702.04) * mm});
            skLineSegment(sketch, "E65.4.0.14", {"start": v(-11076.9, 11702.04) * mm, "end": v(-10976.9, 11702.04) * mm});
            skLineSegment(sketch, "E65.4.0.15", {"start": v(-10376.9, 12702.04) * mm, "end": v(-10376.9, 12802.04) * mm});
            skLineSegment(sketch, "E65.4.0.16", {"start": v(-10776.9, 11502.04) * mm, "end": v(-10776.9, 11402.04) * mm});
            skLineSegment(sketch, "E65.4.0.17", {"start": v(-10976.9, 11702.04) * mm, "end": v(-10976.9, 11502.04) * mm});
            skLineSegment(sketch, "E65.4.0.18", {"start": v(-10976.9, 12502.04) * mm, "end": v(-10976.9, 12702.04) * mm});
            skLineSegment(sketch, "E65.4.0.19", {"start": v(-10176.9, 11502.04) * mm, "end": v(-10376.9, 11502.04) * mm});
            skLineSegment(sketch, "E65.4.0.20", {"start": v(-10776.9, 12702.04) * mm, "end": v(-10776.9, 12802.04) * mm});
            skLineSegment(sketch, "E65.4.0.21", {"start": v(-10076.9, 12502.04) * mm, "end": v(-10176.9, 12502.04) * mm});
            skLineSegment(sketch, "E65.4.0.22", {"start": v(-10176.9, 11702.04) * mm, "end": v(-10176.9, 11502.04) * mm});
            skLineSegment(sketch, "E65.4.0.23", {"start": v(-10176.9, 12502.04) * mm, "end": v(-10176.9, 12702.04) * mm});
            skLineSegment(sketch, "E66.0.1.0", {"start": v(-10176.9, 11002.04) * mm, "end": v(-10376.9, 11002.04) * mm});
            skLineSegment(sketch, "E66.0.1.1", {"start": v(-10976.9, 10802.04) * mm, "end": v(-10976.9, 11002.04) * mm});
            skLineSegment(sketch, "E66.0.1.2", {"start": v(-10176.9, 10802.04) * mm, "end": v(-10176.9, 11002.04) * mm});
            skLineSegment(sketch, "E66.0.1.3", {"start": v(-10076.9, 10002.04) * mm, "end": v(-10076.9, 9702.04) * mm});
            skLineSegment(sketch, "E66.0.1.4", {"start": v(-11076.9, 11102.04) * mm, "end": v(-11076.9, 10802.04) * mm});
            skLineSegment(sketch, "E66.0.1.5", {"start": v(-10976.9, 9802.04) * mm, "end": v(-10776.9, 9802.04) * mm});
            skLineSegment(sketch, "E66.0.1.6", {"start": v(-11076.9, 10002.04) * mm, "end": v(-11076.9, 9702.04) * mm});
            skLineSegment(sketch, "E66.0.1.7", {"start": v(-10176.9, 10002.04) * mm, "end": v(-10176.9, 9802.04) * mm});
            skLineSegment(sketch, "E66.0.1.8", {"start": v(-10976.9, 10002.04) * mm, "end": v(-10976.9, 9802.04) * mm});
            skLineSegment(sketch, "E66.0.1.9", {"start": v(-10976.9, 11002.04) * mm, "end": v(-10776.9, 11002.04) * mm});
            skLineSegment(sketch, "E66.0.1.10", {"start": v(-11076.9, 9702.04) * mm, "end": v(-10776.9, 9702.04) * mm});
            skLineSegment(sketch, "E66.0.1.11", {"start": v(-10376.9, 11102.04) * mm, "end": v(-10076.9, 11102.04) * mm});
            skLineSegment(sketch, "E66.0.1.12", {"start": v(-10376.9, 9702.04) * mm, "end": v(-10076.9, 9702.04) * mm});
            skLineSegment(sketch, "E66.0.1.13", {"start": v(-11076.9, 11102.04) * mm, "end": v(-10776.9, 11102.04) * mm});
            skLineSegment(sketch, "E66.0.1.14", {"start": v(-10076.9, 11102.04) * mm, "end": v(-10076.9, 10802.04) * mm});
            skLineSegment(sketch, "E66.0.1.15", {"start": v(-10176.9, 9802.04) * mm, "end": v(-10376.9, 9802.04) * mm});
            skLineSegment(sketch, "E66.0.1.16", {"start": v(-10376.9, 9802.04) * mm, "end": v(-10376.9, 9702.04) * mm});
            skLineSegment(sketch, "E66.0.1.17", {"start": v(-10376.9, 11002.04) * mm, "end": v(-10376.9, 11102.04) * mm});
            skLineSegment(sketch, "E66.0.1.18", {"start": v(-10776.9, 11002.04) * mm, "end": v(-10776.9, 11102.04) * mm});
            skLineSegment(sketch, "E66.0.1.19", {"start": v(-11076.9, 10802.04) * mm, "end": v(-10976.9, 10802.04) * mm});
            skLineSegment(sketch, "E66.0.1.20", {"start": v(-11076.9, 10002.04) * mm, "end": v(-10976.9, 10002.04) * mm});
            skLineSegment(sketch, "E66.0.1.21", {"start": v(-10076.9, 10002.04) * mm, "end": v(-10176.9, 10002.04) * mm});
            skLineSegment(sketch, "E66.0.1.22", {"start": v(-10776.9, 9802.04) * mm, "end": v(-10776.9, 9702.04) * mm});
            skLineSegment(sketch, "E66.0.1.23", {"start": v(-10076.9, 10802.04) * mm, "end": v(-10176.9, 10802.04) * mm});
            skLineSegment(sketch, "E66.1.0.0", {"start": v(-11426.9, 12702.04) * mm, "end": v(-11626.9, 12702.04) * mm});
            skLineSegment(sketch, "E66.1.0.1", {"start": v(-12226.9, 12502.04) * mm, "end": v(-12226.9, 12702.04) * mm});
            skLineSegment(sketch, "E66.1.0.2", {"start": v(-11426.9, 12502.04) * mm, "end": v(-11426.9, 12702.04) * mm});
            skLineSegment(sketch, "E66.1.0.3", {"start": v(-11326.9, 11702.04) * mm, "end": v(-11326.9, 11402.04) * mm});
            skLineSegment(sketch, "E66.1.0.4", {"start": v(-12326.9, 12802.04) * mm, "end": v(-12326.9, 12502.04) * mm});
            skLineSegment(sketch, "E66.1.0.5", {"start": v(-12226.9, 11502.04) * mm, "end": v(-12026.9, 11502.04) * mm});
            skLineSegment(sketch, "E66.1.0.6", {"start": v(-12326.9, 11702.04) * mm, "end": v(-12326.9, 11402.04) * mm});
            skLineSegment(sketch, "E66.1.0.7", {"start": v(-11426.9, 11702.04) * mm, "end": v(-11426.9, 11502.04) * mm});
            skLineSegment(sketch, "E66.1.0.8", {"start": v(-12226.9, 11702.04) * mm, "end": v(-12226.9, 11502.04) * mm});
            skLineSegment(sketch, "E66.1.0.9", {"start": v(-12226.9, 12702.04) * mm, "end": v(-12026.9, 12702.04) * mm});
            skLineSegment(sketch, "E66.1.0.10", {"start": v(-12326.9, 11402.04) * mm, "end": v(-12026.9, 11402.04) * mm});
            skLineSegment(sketch, "E66.1.0.11", {"start": v(-11626.9, 12802.04) * mm, "end": v(-11326.9, 12802.04) * mm});
            skLineSegment(sketch, "E66.1.0.12", {"start": v(-11626.9, 11402.04) * mm, "end": v(-11326.9, 11402.04) * mm});
            skLineSegment(sketch, "E66.1.0.13", {"start": v(-12326.9, 12802.04) * mm, "end": v(-12026.9, 12802.04) * mm});
            skLineSegment(sketch, "E66.1.0.14", {"start": v(-11326.9, 12802.04) * mm, "end": v(-11326.9, 12502.04) * mm});
            skLineSegment(sketch, "E66.1.0.15", {"start": v(-11426.9, 11502.04) * mm, "end": v(-11626.9, 11502.04) * mm});
            skLineSegment(sketch, "E66.1.0.16", {"start": v(-11626.9, 11502.04) * mm, "end": v(-11626.9, 11402.04) * mm});
            skLineSegment(sketch, "E66.1.0.17", {"start": v(-11626.9, 12702.04) * mm, "end": v(-11626.9, 12802.04) * mm});
            skLineSegment(sketch, "E66.1.0.18", {"start": v(-12026.9, 12702.04) * mm, "end": v(-12026.9, 12802.04) * mm});
            skLineSegment(sketch, "E66.1.0.19", {"start": v(-12326.9, 12502.04) * mm, "end": v(-12226.9, 12502.04) * mm});
            skLineSegment(sketch, "E66.1.0.20", {"start": v(-12326.9, 11702.04) * mm, "end": v(-12226.9, 11702.04) * mm});
            skLineSegment(sketch, "E66.1.0.21", {"start": v(-11326.9, 11702.04) * mm, "end": v(-11426.9, 11702.04) * mm});
            skLineSegment(sketch, "E66.1.0.22", {"start": v(-12026.9, 11502.04) * mm, "end": v(-12026.9, 11402.04) * mm});
            skLineSegment(sketch, "E66.1.0.23", {"start": v(-11326.9, 12502.04) * mm, "end": v(-11426.9, 12502.04) * mm});
            skLineSegment(sketch, "E66.1.1.0", {"start": v(-11426.9, 11002.04) * mm, "end": v(-11626.9, 11002.04) * mm});
            skLineSegment(sketch, "E66.1.1.1", {"start": v(-12226.9, 10802.04) * mm, "end": v(-12226.9, 11002.04) * mm});
            skLineSegment(sketch, "E66.1.1.2", {"start": v(-11426.9, 10802.04) * mm, "end": v(-11426.9, 11002.04) * mm});
            skLineSegment(sketch, "E66.1.1.3", {"start": v(-11326.9, 10002.04) * mm, "end": v(-11326.9, 9702.04) * mm});
            skLineSegment(sketch, "E66.1.1.4", {"start": v(-12326.9, 11102.04) * mm, "end": v(-12326.9, 10802.04) * mm});
            skLineSegment(sketch, "E66.1.1.5", {"start": v(-12226.9, 9802.04) * mm, "end": v(-12026.9, 9802.04) * mm});
            skLineSegment(sketch, "E66.1.1.6", {"start": v(-12326.9, 10002.04) * mm, "end": v(-12326.9, 9702.04) * mm});
            skLineSegment(sketch, "E66.1.1.7", {"start": v(-11426.9, 10002.04) * mm, "end": v(-11426.9, 9802.04) * mm});
            skLineSegment(sketch, "E66.1.1.8", {"start": v(-12226.9, 10002.04) * mm, "end": v(-12226.9, 9802.04) * mm});
            skLineSegment(sketch, "E66.1.1.9", {"start": v(-12226.9, 11002.04) * mm, "end": v(-12026.9, 11002.04) * mm});
            skLineSegment(sketch, "E66.1.1.10", {"start": v(-12326.9, 9702.04) * mm, "end": v(-12026.9, 9702.04) * mm});
            skLineSegment(sketch, "E66.1.1.11", {"start": v(-11626.9, 11102.04) * mm, "end": v(-11326.9, 11102.04) * mm});
            skLineSegment(sketch, "E66.1.1.12", {"start": v(-11626.9, 9702.04) * mm, "end": v(-11326.9, 9702.04) * mm});
            skLineSegment(sketch, "E66.1.1.13", {"start": v(-12326.9, 11102.04) * mm, "end": v(-12026.9, 11102.04) * mm});
            skLineSegment(sketch, "E66.1.1.14", {"start": v(-11326.9, 11102.04) * mm, "end": v(-11326.9, 10802.04) * mm});
            skLineSegment(sketch, "E66.1.1.15", {"start": v(-11426.9, 9802.04) * mm, "end": v(-11626.9, 9802.04) * mm});
            skLineSegment(sketch, "E66.1.1.16", {"start": v(-11626.9, 9802.04) * mm, "end": v(-11626.9, 9702.04) * mm});
            skLineSegment(sketch, "E66.1.1.17", {"start": v(-11626.9, 11002.04) * mm, "end": v(-11626.9, 11102.04) * mm});
            skLineSegment(sketch, "E66.1.1.18", {"start": v(-12026.9, 11002.04) * mm, "end": v(-12026.9, 11102.04) * mm});
            skLineSegment(sketch, "E66.1.1.19", {"start": v(-12326.9, 10802.04) * mm, "end": v(-12226.9, 10802.04) * mm});
            skLineSegment(sketch, "E66.1.1.20", {"start": v(-12326.9, 10002.04) * mm, "end": v(-12226.9, 10002.04) * mm});
            skLineSegment(sketch, "E66.1.1.21", {"start": v(-11326.9, 10002.04) * mm, "end": v(-11426.9, 10002.04) * mm});
            skLineSegment(sketch, "E66.1.1.22", {"start": v(-12026.9, 9802.04) * mm, "end": v(-12026.9, 9702.04) * mm});
            skLineSegment(sketch, "E66.1.1.23", {"start": v(-11326.9, 10802.04) * mm, "end": v(-11426.9, 10802.04) * mm});
            skLineSegment(sketch, "E66.2.0.0", {"start": v(-12676.9, 12702.04) * mm, "end": v(-12876.9, 12702.04) * mm});
            skLineSegment(sketch, "E66.2.0.1", {"start": v(-13476.9, 12502.04) * mm, "end": v(-13476.9, 12702.04) * mm});
            skLineSegment(sketch, "E66.2.0.2", {"start": v(-12676.9, 12502.04) * mm, "end": v(-12676.9, 12702.04) * mm});
            skLineSegment(sketch, "E66.2.0.3", {"start": v(-12576.9, 11702.04) * mm, "end": v(-12576.9, 11402.04) * mm});
            skLineSegment(sketch, "E66.2.0.4", {"start": v(-13576.9, 12802.04) * mm, "end": v(-13576.9, 12502.04) * mm});
            skLineSegment(sketch, "E66.2.0.5", {"start": v(-13476.9, 11502.04) * mm, "end": v(-13276.9, 11502.04) * mm});
            skLineSegment(sketch, "E66.2.0.6", {"start": v(-13576.9, 11702.04) * mm, "end": v(-13576.9, 11402.04) * mm});
            skLineSegment(sketch, "E66.2.0.7", {"start": v(-12676.9, 11702.04) * mm, "end": v(-12676.9, 11502.04) * mm});
            skLineSegment(sketch, "E66.2.0.8", {"start": v(-13476.9, 11702.04) * mm, "end": v(-13476.9, 11502.04) * mm});
            skLineSegment(sketch, "E66.2.0.9", {"start": v(-13476.9, 12702.04) * mm, "end": v(-13276.9, 12702.04) * mm});
            skLineSegment(sketch, "E66.2.0.10", {"start": v(-13576.9, 11402.04) * mm, "end": v(-13276.9, 11402.04) * mm});
            skLineSegment(sketch, "E66.2.0.11", {"start": v(-12876.9, 12802.04) * mm, "end": v(-12576.9, 12802.04) * mm});
            skLineSegment(sketch, "E66.2.0.12", {"start": v(-12876.9, 11402.04) * mm, "end": v(-12576.9, 11402.04) * mm});
            skLineSegment(sketch, "E66.2.0.13", {"start": v(-13576.9, 12802.04) * mm, "end": v(-13276.9, 12802.04) * mm});
            skLineSegment(sketch, "E66.2.0.14", {"start": v(-12576.9, 12802.04) * mm, "end": v(-12576.9, 12502.04) * mm});
            skLineSegment(sketch, "E66.2.0.15", {"start": v(-12676.9, 11502.04) * mm, "end": v(-12876.9, 11502.04) * mm});
            skLineSegment(sketch, "E66.2.0.16", {"start": v(-12876.9, 11502.04) * mm, "end": v(-12876.9, 11402.04) * mm});
            skLineSegment(sketch, "E66.2.0.17", {"start": v(-12876.9, 12702.04) * mm, "end": v(-12876.9, 12802.04) * mm});
            skLineSegment(sketch, "E66.2.0.18", {"start": v(-13276.9, 12702.04) * mm, "end": v(-13276.9, 12802.04) * mm});
            skLineSegment(sketch, "E66.2.0.19", {"start": v(-13576.9, 12502.04) * mm, "end": v(-13476.9, 12502.04) * mm});
            skLineSegment(sketch, "E66.2.0.20", {"start": v(-13576.9, 11702.04) * mm, "end": v(-13476.9, 11702.04) * mm});
            skLineSegment(sketch, "E66.2.0.21", {"start": v(-12576.9, 11702.04) * mm, "end": v(-12676.9, 11702.04) * mm});
            skLineSegment(sketch, "E66.2.0.22", {"start": v(-13276.9, 11502.04) * mm, "end": v(-13276.9, 11402.04) * mm});
            skLineSegment(sketch, "E66.2.0.23", {"start": v(-12576.9, 12502.04) * mm, "end": v(-12676.9, 12502.04) * mm});
            skLineSegment(sketch, "E66.2.1.0", {"start": v(-12676.9, 11002.04) * mm, "end": v(-12876.9, 11002.04) * mm});
            skLineSegment(sketch, "E66.2.1.1", {"start": v(-13476.9, 10802.04) * mm, "end": v(-13476.9, 11002.04) * mm});
            skLineSegment(sketch, "E66.2.1.2", {"start": v(-12676.9, 10802.04) * mm, "end": v(-12676.9, 11002.04) * mm});
            skLineSegment(sketch, "E66.2.1.3", {"start": v(-12576.9, 10002.04) * mm, "end": v(-12576.9, 9702.04) * mm});
            skLineSegment(sketch, "E66.2.1.4", {"start": v(-13576.9, 11102.04) * mm, "end": v(-13576.9, 10802.04) * mm});
            skLineSegment(sketch, "E66.2.1.5", {"start": v(-13476.9, 9802.04) * mm, "end": v(-13276.9, 9802.04) * mm});
            skLineSegment(sketch, "E66.2.1.6", {"start": v(-13576.9, 10002.04) * mm, "end": v(-13576.9, 9702.04) * mm});
            skLineSegment(sketch, "E66.2.1.7", {"start": v(-12676.9, 10002.04) * mm, "end": v(-12676.9, 9802.04) * mm});
            skLineSegment(sketch, "E66.2.1.8", {"start": v(-13476.9, 10002.04) * mm, "end": v(-13476.9, 9802.04) * mm});
            skLineSegment(sketch, "E66.2.1.9", {"start": v(-13476.9, 11002.04) * mm, "end": v(-13276.9, 11002.04) * mm});
            skLineSegment(sketch, "E66.2.1.10", {"start": v(-13576.9, 9702.04) * mm, "end": v(-13276.9, 9702.04) * mm});
            skLineSegment(sketch, "E66.2.1.11", {"start": v(-12876.9, 11102.04) * mm, "end": v(-12576.9, 11102.04) * mm});
            skLineSegment(sketch, "E66.2.1.12", {"start": v(-12876.9, 9702.04) * mm, "end": v(-12576.9, 9702.04) * mm});
            skLineSegment(sketch, "E66.2.1.13", {"start": v(-13576.9, 11102.04) * mm, "end": v(-13276.9, 11102.04) * mm});
            skLineSegment(sketch, "E66.2.1.14", {"start": v(-12576.9, 11102.04) * mm, "end": v(-12576.9, 10802.04) * mm});
            skLineSegment(sketch, "E66.2.1.15", {"start": v(-12676.9, 9802.04) * mm, "end": v(-12876.9, 9802.04) * mm});
            skLineSegment(sketch, "E66.2.1.16", {"start": v(-12876.9, 9802.04) * mm, "end": v(-12876.9, 9702.04) * mm});
            skLineSegment(sketch, "E66.2.1.17", {"start": v(-12876.9, 11002.04) * mm, "end": v(-12876.9, 11102.04) * mm});
            skLineSegment(sketch, "E66.2.1.18", {"start": v(-13276.9, 11002.04) * mm, "end": v(-13276.9, 11102.04) * mm});
            skLineSegment(sketch, "E66.2.1.19", {"start": v(-13576.9, 10802.04) * mm, "end": v(-13476.9, 10802.04) * mm});
            skLineSegment(sketch, "E66.2.1.20", {"start": v(-13576.9, 10002.04) * mm, "end": v(-13476.9, 10002.04) * mm});
            skLineSegment(sketch, "E66.2.1.21", {"start": v(-12576.9, 10002.04) * mm, "end": v(-12676.9, 10002.04) * mm});
            skLineSegment(sketch, "E66.2.1.22", {"start": v(-13276.9, 9802.04) * mm, "end": v(-13276.9, 9702.04) * mm});
            skLineSegment(sketch, "E66.2.1.23", {"start": v(-12576.9, 10802.04) * mm, "end": v(-12676.9, 10802.04) * mm});
            skLineSegment(sketch, "E66.3.0.0", {"start": v(-13926.9, 12702.04) * mm, "end": v(-14126.9, 12702.04) * mm});
            skLineSegment(sketch, "E66.3.0.1", {"start": v(-14726.9, 12502.04) * mm, "end": v(-14726.9, 12702.04) * mm});
            skLineSegment(sketch, "E66.3.0.2", {"start": v(-13926.9, 12502.04) * mm, "end": v(-13926.9, 12702.04) * mm});
            skLineSegment(sketch, "E66.3.0.3", {"start": v(-13826.9, 11702.04) * mm, "end": v(-13826.9, 11402.04) * mm});
            skLineSegment(sketch, "E66.3.0.4", {"start": v(-14826.9, 12802.04) * mm, "end": v(-14826.9, 12502.04) * mm});
            skLineSegment(sketch, "E66.3.0.5", {"start": v(-14726.9, 11502.04) * mm, "end": v(-14526.9, 11502.04) * mm});
            skLineSegment(sketch, "E66.3.0.6", {"start": v(-14826.9, 11702.04) * mm, "end": v(-14826.9, 11402.04) * mm});
            skLineSegment(sketch, "E66.3.0.7", {"start": v(-13926.9, 11702.04) * mm, "end": v(-13926.9, 11502.04) * mm});
            skLineSegment(sketch, "E66.3.0.8", {"start": v(-14726.9, 11702.04) * mm, "end": v(-14726.9, 11502.04) * mm});
            skLineSegment(sketch, "E66.3.0.9", {"start": v(-14726.9, 12702.04) * mm, "end": v(-14526.9, 12702.04) * mm});
            skLineSegment(sketch, "E66.3.0.10", {"start": v(-14826.9, 11402.04) * mm, "end": v(-14526.9, 11402.04) * mm});
            skLineSegment(sketch, "E66.3.0.11", {"start": v(-14126.9, 12802.04) * mm, "end": v(-13826.9, 12802.04) * mm});
            skLineSegment(sketch, "E66.3.0.12", {"start": v(-14126.9, 11402.04) * mm, "end": v(-13826.9, 11402.04) * mm});
            skLineSegment(sketch, "E66.3.0.13", {"start": v(-14826.9, 12802.04) * mm, "end": v(-14526.9, 12802.04) * mm});
            skLineSegment(sketch, "E66.3.0.14", {"start": v(-13826.9, 12802.04) * mm, "end": v(-13826.9, 12502.04) * mm});
            skLineSegment(sketch, "E66.3.0.15", {"start": v(-13926.9, 11502.04) * mm, "end": v(-14126.9, 11502.04) * mm});
            skLineSegment(sketch, "E66.3.0.16", {"start": v(-14126.9, 11502.04) * mm, "end": v(-14126.9, 11402.04) * mm});
            skLineSegment(sketch, "E66.3.0.17", {"start": v(-14126.9, 12702.04) * mm, "end": v(-14126.9, 12802.04) * mm});
            skLineSegment(sketch, "E66.3.0.18", {"start": v(-14526.9, 12702.04) * mm, "end": v(-14526.9, 12802.04) * mm});
            skLineSegment(sketch, "E66.3.0.19", {"start": v(-14826.9, 12502.04) * mm, "end": v(-14726.9, 12502.04) * mm});
            skLineSegment(sketch, "E66.3.0.20", {"start": v(-14826.9, 11702.04) * mm, "end": v(-14726.9, 11702.04) * mm});
            skLineSegment(sketch, "E66.3.0.21", {"start": v(-13826.9, 11702.04) * mm, "end": v(-13926.9, 11702.04) * mm});
            skLineSegment(sketch, "E66.3.0.22", {"start": v(-14526.9, 11502.04) * mm, "end": v(-14526.9, 11402.04) * mm});
            skLineSegment(sketch, "E66.3.0.23", {"start": v(-13826.9, 12502.04) * mm, "end": v(-13926.9, 12502.04) * mm});
            skLineSegment(sketch, "E66.3.1.0", {"start": v(-13926.9, 11002.04) * mm, "end": v(-14126.9, 11002.04) * mm});
            skLineSegment(sketch, "E66.3.1.1", {"start": v(-14726.9, 10802.04) * mm, "end": v(-14726.9, 11002.04) * mm});
            skLineSegment(sketch, "E66.3.1.2", {"start": v(-13926.9, 10802.04) * mm, "end": v(-13926.9, 11002.04) * mm});
            skLineSegment(sketch, "E66.3.1.3", {"start": v(-13826.9, 10002.04) * mm, "end": v(-13826.9, 9702.04) * mm});
            skLineSegment(sketch, "E66.3.1.4", {"start": v(-14826.9, 11102.04) * mm, "end": v(-14826.9, 10802.04) * mm});
            skLineSegment(sketch, "E66.3.1.5", {"start": v(-14726.9, 9802.04) * mm, "end": v(-14526.9, 9802.04) * mm});
            skLineSegment(sketch, "E66.3.1.6", {"start": v(-14826.9, 10002.04) * mm, "end": v(-14826.9, 9702.04) * mm});
            skLineSegment(sketch, "E66.3.1.7", {"start": v(-13926.9, 10002.04) * mm, "end": v(-13926.9, 9802.04) * mm});
            skLineSegment(sketch, "E66.3.1.8", {"start": v(-14726.9, 10002.04) * mm, "end": v(-14726.9, 9802.04) * mm});
            skLineSegment(sketch, "E66.3.1.9", {"start": v(-14726.9, 11002.04) * mm, "end": v(-14526.9, 11002.04) * mm});
            skLineSegment(sketch, "E66.3.1.10", {"start": v(-14826.9, 9702.04) * mm, "end": v(-14526.9, 9702.04) * mm});
            skLineSegment(sketch, "E66.3.1.11", {"start": v(-14126.9, 11102.04) * mm, "end": v(-13826.9, 11102.04) * mm});
            skLineSegment(sketch, "E66.3.1.12", {"start": v(-14126.9, 9702.04) * mm, "end": v(-13826.9, 9702.04) * mm});
            skLineSegment(sketch, "E66.3.1.13", {"start": v(-14826.9, 11102.04) * mm, "end": v(-14526.9, 11102.04) * mm});
            skLineSegment(sketch, "E66.3.1.14", {"start": v(-13826.9, 11102.04) * mm, "end": v(-13826.9, 10802.04) * mm});
            skLineSegment(sketch, "E66.3.1.15", {"start": v(-13926.9, 9802.04) * mm, "end": v(-14126.9, 9802.04) * mm});
            skLineSegment(sketch, "E66.3.1.16", {"start": v(-14126.9, 9802.04) * mm, "end": v(-14126.9, 9702.04) * mm});
            skLineSegment(sketch, "E66.3.1.17", {"start": v(-14126.9, 11002.04) * mm, "end": v(-14126.9, 11102.04) * mm});
            skLineSegment(sketch, "E66.3.1.18", {"start": v(-14526.9, 11002.04) * mm, "end": v(-14526.9, 11102.04) * mm});
            skLineSegment(sketch, "E66.3.1.19", {"start": v(-14826.9, 10802.04) * mm, "end": v(-14726.9, 10802.04) * mm});
            skLineSegment(sketch, "E66.3.1.20", {"start": v(-14826.9, 10002.04) * mm, "end": v(-14726.9, 10002.04) * mm});
            skLineSegment(sketch, "E66.3.1.21", {"start": v(-13826.9, 10002.04) * mm, "end": v(-13926.9, 10002.04) * mm});
            skLineSegment(sketch, "E66.3.1.22", {"start": v(-14526.9, 9802.04) * mm, "end": v(-14526.9, 9702.04) * mm});
            skLineSegment(sketch, "E66.3.1.23", {"start": v(-13826.9, 10802.04) * mm, "end": v(-13926.9, 10802.04) * mm});
            skLineSegment(sketch, "E66.direction1", {"start": v(-11076.9, 11402.04) * mm, "end": v(-12326.9, 11402.04) * mm, "construction": true});
            skLineSegment(sketch, "E66.direction2", {"start": v(-11076.9, 11402.04) * mm, "end": v(-11076.9, 9702.04) * mm, "construction": true});
            skLineSegment(sketch, "E67", {"start": v(-15779.42, 13380.32) * mm, "end": v(-15279.42, 12922.62) * mm});
            skLineSegment(sketch, "E68", {"start": v(-15894.57, 13380.32) * mm, "end": v(-15279.42, 12828.34) * mm});
            skLineSegment(sketch, "E69", {"start": v(-16279.42, 13198.23) * mm, "end": v(-15279.42, 12226.36) * mm});
            skLineSegment(sketch, "E70", {"start": v(-16279.42, 13074.93) * mm, "end": v(-15279.42, 12103.9) * mm});
            skLineSegment(sketch, "E71.0.1.0", {"start": v(-16279.42, 12573.23) * mm, "end": v(-15279.42, 11601.36) * mm});
            skLineSegment(sketch, "E71.0.1.1", {"start": v(-16279.42, 12449.93) * mm, "end": v(-15279.42, 11478.9) * mm});
            skLineSegment(sketch, "E71.0.2.0", {"start": v(-16279.42, 11948.23) * mm, "end": v(-15279.42, 10976.36) * mm});
            skLineSegment(sketch, "E71.0.2.1", {"start": v(-16279.42, 11824.93) * mm, "end": v(-15279.42, 10853.9) * mm});
            skLineSegment(sketch, "E71.0.3.0", {"start": v(-16279.42, 11323.23) * mm, "end": v(-15279.42, 10351.36) * mm});
            skLineSegment(sketch, "E71.0.3.1", {"start": v(-16279.42, 11199.93) * mm, "end": v(-15279.42, 10228.9) * mm});
            skLineSegment(sketch, "E71.0.4.0", {"start": v(-16279.42, 10698.23) * mm, "end": v(-15279.42, 9726.36) * mm});
            skLineSegment(sketch, "E71.0.4.1", {"start": v(-16279.42, 10574.93) * mm, "end": v(-15358.13, 9680.32) * mm});
            skLineSegment(sketch, "E71.0.5.0", {"start": v(-16279.42, 10073.23) * mm, "end": v(-15875.14, 9680.32) * mm});
            skLineSegment(sketch, "E71.0.5.1", {"start": v(-16279.42, 9949.93) * mm, "end": v(-16001.77, 9680.32) * mm});
            skLineSegment(sketch, "E71.direction1", {"start": v(-16279.42, 13074.93) * mm, "end": v(-16254.42, 13074.93) * mm, "construction": true});
            skLineSegment(sketch, "E71.direction2", {"start": v(-16279.42, 13074.93) * mm, "end": v(-16279.42, 12449.93) * mm, "construction": true});
            skLineSegment(sketch, "E72", {"start": v(-15179.42, 13380.46) * mm, "end": v(-15179.42, 9580.32) * mm});
            skLineSegment(sketch, "E73", {"start": v(-15179.42, 9580.32) * mm, "end": v(-16379.42, 9580.32) * mm});
            skLineSegment(sketch, "E74", {"start": v(-16379.42, 9580.32) * mm, "end": v(-16379.42, 12992.53) * mm});
            skLineSegment(sketch, "E75", {"start": v(-16379.42, 12992.53) * mm, "end": v(-16279.42, 12995.58) * mm});
            skLineSegment(sketch, "E76", {"start": v(-15179.42, 13380.46) * mm, "end": v(-15279.42, 13380.32) * mm});
            skLineSegment(sketch, "E77.3.0.0", {"start": v(-16750.5, 12660.51) * mm, "end": v(-16950.5, 12660.51) * mm});
            skLineSegment(sketch, "E77.3.0.1", {"start": v(-17550.5, 12460.51) * mm, "end": v(-17550.5, 12660.51) * mm});
            skLineSegment(sketch, "E77.3.0.2", {"start": v(-16750.5, 12460.51) * mm, "end": v(-16750.5, 12660.51) * mm});
            skLineSegment(sketch, "E77.3.0.3", {"start": v(-16650.5, 11660.51) * mm, "end": v(-16650.5, 11360.51) * mm});
            skLineSegment(sketch, "E77.3.0.4", {"start": v(-17650.5, 12760.51) * mm, "end": v(-17650.5, 12460.51) * mm});
            skLineSegment(sketch, "E77.3.0.5", {"start": v(-17550.5, 11460.51) * mm, "end": v(-17350.5, 11460.51) * mm});
            skLineSegment(sketch, "E77.3.0.6", {"start": v(-17650.5, 11660.51) * mm, "end": v(-17650.5, 11360.51) * mm});
            skLineSegment(sketch, "E77.3.0.7", {"start": v(-16750.5, 11660.51) * mm, "end": v(-16750.5, 11460.51) * mm});
            skLineSegment(sketch, "E77.3.0.8", {"start": v(-17550.5, 11660.51) * mm, "end": v(-17550.5, 11460.51) * mm});
            skLineSegment(sketch, "E77.3.0.9", {"start": v(-17550.5, 12660.51) * mm, "end": v(-17350.5, 12660.51) * mm});
            skLineSegment(sketch, "E77.3.0.10", {"start": v(-17650.5, 11360.51) * mm, "end": v(-17350.5, 11360.51) * mm});
            skLineSegment(sketch, "E77.3.0.11", {"start": v(-16950.5, 12760.51) * mm, "end": v(-16650.5, 12760.51) * mm});
            skLineSegment(sketch, "E77.3.0.12", {"start": v(-16950.5, 11360.51) * mm, "end": v(-16650.5, 11360.51) * mm});
            skLineSegment(sketch, "E77.3.0.13", {"start": v(-17650.5, 12760.51) * mm, "end": v(-17350.5, 12760.51) * mm});
            skLineSegment(sketch, "E77.3.0.14", {"start": v(-16650.5, 12760.51) * mm, "end": v(-16650.5, 12460.51) * mm});
            skLineSegment(sketch, "E77.3.0.15", {"start": v(-16750.5, 11460.51) * mm, "end": v(-16950.5, 11460.51) * mm});
            skLineSegment(sketch, "E77.3.0.16", {"start": v(-16950.5, 11460.51) * mm, "end": v(-16950.5, 11360.51) * mm});
            skLineSegment(sketch, "E77.3.0.17", {"start": v(-16950.5, 12660.51) * mm, "end": v(-16950.5, 12760.51) * mm});
            skLineSegment(sketch, "E77.3.0.18", {"start": v(-17350.5, 12660.51) * mm, "end": v(-17350.5, 12760.51) * mm});
            skLineSegment(sketch, "E77.3.0.19", {"start": v(-17650.5, 12460.51) * mm, "end": v(-17550.5, 12460.51) * mm});
            skLineSegment(sketch, "E77.3.0.20", {"start": v(-17650.5, 11660.51) * mm, "end": v(-17550.5, 11660.51) * mm});
            skLineSegment(sketch, "E77.3.0.21", {"start": v(-16650.5, 11660.51) * mm, "end": v(-16750.5, 11660.51) * mm});
            skLineSegment(sketch, "E77.3.0.22", {"start": v(-17350.5, 11460.51) * mm, "end": v(-17350.5, 11360.51) * mm});
            skLineSegment(sketch, "E77.3.0.23", {"start": v(-16650.5, 12460.51) * mm, "end": v(-16750.5, 12460.51) * mm});
            skLineSegment(sketch, "E78.0.1.0", {"start": v(-16650.5, 11060.51) * mm, "end": v(-16650.5, 10760.51) * mm});
            skLineSegment(sketch, "E78.0.1.1", {"start": v(-17650.5, 9960.51) * mm, "end": v(-17650.5, 9660.51) * mm});
            skLineSegment(sketch, "E78.0.1.2", {"start": v(-16950.5, 9660.51) * mm, "end": v(-16650.5, 9660.51) * mm});
            skLineSegment(sketch, "E78.0.1.3", {"start": v(-16650.5, 9960.51) * mm, "end": v(-16650.5, 9660.51) * mm});
            skLineSegment(sketch, "E78.0.1.4", {"start": v(-17650.5, 9660.51) * mm, "end": v(-17350.5, 9660.51) * mm});
            skLineSegment(sketch, "E78.0.1.5", {"start": v(-17650.5, 11060.51) * mm, "end": v(-17650.5, 10760.51) * mm});
            skLineSegment(sketch, "E78.0.1.6", {"start": v(-17550.5, 10760.51) * mm, "end": v(-17550.5, 10960.51) * mm});
            skLineSegment(sketch, "E78.0.1.7", {"start": v(-16750.5, 10760.51) * mm, "end": v(-16750.5, 10960.51) * mm});
            skLineSegment(sketch, "E78.0.1.8", {"start": v(-17550.5, 9960.51) * mm, "end": v(-17550.5, 9760.51) * mm});
            skLineSegment(sketch, "E78.0.1.9", {"start": v(-17350.5, 9760.51) * mm, "end": v(-17350.5, 9660.51) * mm});
            skLineSegment(sketch, "E78.0.1.10", {"start": v(-17550.5, 10960.51) * mm, "end": v(-17350.5, 10960.51) * mm});
            skLineSegment(sketch, "E78.0.1.11", {"start": v(-16950.5, 10960.51) * mm, "end": v(-16950.5, 11060.51) * mm});
            skLineSegment(sketch, "E78.0.1.12", {"start": v(-16750.5, 9760.51) * mm, "end": v(-16950.5, 9760.51) * mm});
            skLineSegment(sketch, "E78.0.1.13", {"start": v(-16950.5, 9760.51) * mm, "end": v(-16950.5, 9660.51) * mm});
            skLineSegment(sketch, "E78.0.1.14", {"start": v(-17350.5, 10960.51) * mm, "end": v(-17350.5, 11060.51) * mm});
            skLineSegment(sketch, "E78.0.1.15", {"start": v(-17650.5, 10760.51) * mm, "end": v(-17550.5, 10760.51) * mm});
            skLineSegment(sketch, "E78.0.1.16", {"start": v(-16650.5, 10760.51) * mm, "end": v(-16750.5, 10760.51) * mm});
            skLineSegment(sketch, "E78.0.1.17", {"start": v(-16750.5, 9960.51) * mm, "end": v(-16750.5, 9760.51) * mm});
            skLineSegment(sketch, "E78.0.1.18", {"start": v(-16750.5, 10960.51) * mm, "end": v(-16950.5, 10960.51) * mm});
            skLineSegment(sketch, "E78.0.1.19", {"start": v(-16950.5, 11060.51) * mm, "end": v(-16650.5, 11060.51) * mm});
            skLineSegment(sketch, "E78.0.1.20", {"start": v(-17650.5, 11060.51) * mm, "end": v(-17350.5, 11060.51) * mm});
            skLineSegment(sketch, "E78.0.1.21", {"start": v(-16650.5, 9960.51) * mm, "end": v(-16750.5, 9960.51) * mm});
            skLineSegment(sketch, "E78.0.1.22", {"start": v(-17650.5, 9960.51) * mm, "end": v(-17550.5, 9960.51) * mm});
            skLineSegment(sketch, "E78.0.1.23", {"start": v(-17550.5, 9760.51) * mm, "end": v(-17350.5, 9760.51) * mm});
            skLineSegment(sketch, "E78.1.0.0", {"start": v(-17900.5, 12760.51) * mm, "end": v(-17900.5, 12460.51) * mm});
            skLineSegment(sketch, "E78.1.0.1", {"start": v(-18900.5, 11660.51) * mm, "end": v(-18900.5, 11360.51) * mm});
            skLineSegment(sketch, "E78.1.0.2", {"start": v(-18200.5, 11360.51) * mm, "end": v(-17900.5, 11360.51) * mm});
            skLineSegment(sketch, "E78.1.0.3", {"start": v(-17900.5, 11660.51) * mm, "end": v(-17900.5, 11360.51) * mm});
            skLineSegment(sketch, "E78.1.0.4", {"start": v(-18900.5, 11360.51) * mm, "end": v(-18600.5, 11360.51) * mm});
            skLineSegment(sketch, "E78.1.0.5", {"start": v(-18900.5, 12760.51) * mm, "end": v(-18900.5, 12460.51) * mm});
            skLineSegment(sketch, "E78.1.0.6", {"start": v(-18800.5, 12460.51) * mm, "end": v(-18800.5, 12660.51) * mm});
            skLineSegment(sketch, "E78.1.0.7", {"start": v(-18000.5, 12460.51) * mm, "end": v(-18000.5, 12660.51) * mm});
            skLineSegment(sketch, "E78.1.0.8", {"start": v(-18800.5, 11660.51) * mm, "end": v(-18800.5, 11460.51) * mm});
            skLineSegment(sketch, "E78.1.0.9", {"start": v(-18600.5, 11460.51) * mm, "end": v(-18600.5, 11360.51) * mm});
            skLineSegment(sketch, "E78.1.0.10", {"start": v(-18800.5, 12660.51) * mm, "end": v(-18600.5, 12660.51) * mm});
            skLineSegment(sketch, "E78.1.0.11", {"start": v(-18200.5, 12660.51) * mm, "end": v(-18200.5, 12760.51) * mm});
            skLineSegment(sketch, "E78.1.0.12", {"start": v(-18000.5, 11460.51) * mm, "end": v(-18200.5, 11460.51) * mm});
            skLineSegment(sketch, "E78.1.0.13", {"start": v(-18200.5, 11460.51) * mm, "end": v(-18200.5, 11360.51) * mm});
            skLineSegment(sketch, "E78.1.0.14", {"start": v(-18600.5, 12660.51) * mm, "end": v(-18600.5, 12760.51) * mm});
            skLineSegment(sketch, "E78.1.0.15", {"start": v(-18900.5, 12460.51) * mm, "end": v(-18800.5, 12460.51) * mm});
            skLineSegment(sketch, "E78.1.0.16", {"start": v(-17900.5, 12460.51) * mm, "end": v(-18000.5, 12460.51) * mm});
            skLineSegment(sketch, "E78.1.0.17", {"start": v(-18000.5, 11660.51) * mm, "end": v(-18000.5, 11460.51) * mm});
            skLineSegment(sketch, "E78.1.0.18", {"start": v(-18000.5, 12660.51) * mm, "end": v(-18200.5, 12660.51) * mm});
            skLineSegment(sketch, "E78.1.0.19", {"start": v(-18200.5, 12760.51) * mm, "end": v(-17900.5, 12760.51) * mm});
            skLineSegment(sketch, "E78.1.0.20", {"start": v(-18900.5, 12760.51) * mm, "end": v(-18600.5, 12760.51) * mm});
            skLineSegment(sketch, "E78.1.0.21", {"start": v(-17900.5, 11660.51) * mm, "end": v(-18000.5, 11660.51) * mm});
            skLineSegment(sketch, "E78.1.0.22", {"start": v(-18900.5, 11660.51) * mm, "end": v(-18800.5, 11660.51) * mm});
            skLineSegment(sketch, "E78.1.0.23", {"start": v(-18800.5, 11460.51) * mm, "end": v(-18600.5, 11460.51) * mm});
            skLineSegment(sketch, "E78.1.1.0", {"start": v(-17900.5, 11060.51) * mm, "end": v(-17900.5, 10760.51) * mm});
            skLineSegment(sketch, "E78.1.1.1", {"start": v(-18900.5, 9960.51) * mm, "end": v(-18900.5, 9660.51) * mm});
            skLineSegment(sketch, "E78.1.1.2", {"start": v(-18200.5, 9660.51) * mm, "end": v(-17900.5, 9660.51) * mm});
            skLineSegment(sketch, "E78.1.1.3", {"start": v(-17900.5, 9960.51) * mm, "end": v(-17900.5, 9660.51) * mm});
            skLineSegment(sketch, "E78.1.1.4", {"start": v(-18900.5, 9660.51) * mm, "end": v(-18600.5, 9660.51) * mm});
            skLineSegment(sketch, "E78.1.1.5", {"start": v(-18900.5, 11060.51) * mm, "end": v(-18900.5, 10760.51) * mm});
            skLineSegment(sketch, "E78.1.1.6", {"start": v(-18800.5, 10760.51) * mm, "end": v(-18800.5, 10960.51) * mm});
            skLineSegment(sketch, "E78.1.1.7", {"start": v(-18000.5, 10760.51) * mm, "end": v(-18000.5, 10960.51) * mm});
            skLineSegment(sketch, "E78.1.1.8", {"start": v(-18800.5, 9960.51) * mm, "end": v(-18800.5, 9760.51) * mm});
            skLineSegment(sketch, "E78.1.1.9", {"start": v(-18600.5, 9760.51) * mm, "end": v(-18600.5, 9660.51) * mm});
            skLineSegment(sketch, "E78.1.1.10", {"start": v(-18800.5, 10960.51) * mm, "end": v(-18600.5, 10960.51) * mm});
            skLineSegment(sketch, "E78.1.1.11", {"start": v(-18200.5, 10960.51) * mm, "end": v(-18200.5, 11060.51) * mm});
            skLineSegment(sketch, "E78.1.1.12", {"start": v(-18000.5, 9760.51) * mm, "end": v(-18200.5, 9760.51) * mm});
            skLineSegment(sketch, "E78.1.1.13", {"start": v(-18200.5, 9760.51) * mm, "end": v(-18200.5, 9660.51) * mm});
            skLineSegment(sketch, "E78.1.1.14", {"start": v(-18600.5, 10960.51) * mm, "end": v(-18600.5, 11060.51) * mm});
            skLineSegment(sketch, "E78.1.1.15", {"start": v(-18900.5, 10760.51) * mm, "end": v(-18800.5, 10760.51) * mm});
            skLineSegment(sketch, "E78.1.1.16", {"start": v(-17900.5, 10760.51) * mm, "end": v(-18000.5, 10760.51) * mm});
            skLineSegment(sketch, "E78.1.1.17", {"start": v(-18000.5, 9960.51) * mm, "end": v(-18000.5, 9760.51) * mm});
            skLineSegment(sketch, "E78.1.1.18", {"start": v(-18000.5, 10960.51) * mm, "end": v(-18200.5, 10960.51) * mm});
            skLineSegment(sketch, "E78.1.1.19", {"start": v(-18200.5, 11060.51) * mm, "end": v(-17900.5, 11060.51) * mm});
            skLineSegment(sketch, "E78.1.1.20", {"start": v(-18900.5, 11060.51) * mm, "end": v(-18600.5, 11060.51) * mm});
            skLineSegment(sketch, "E78.1.1.21", {"start": v(-17900.5, 9960.51) * mm, "end": v(-18000.5, 9960.51) * mm});
            skLineSegment(sketch, "E78.1.1.22", {"start": v(-18900.5, 9960.51) * mm, "end": v(-18800.5, 9960.51) * mm});
            skLineSegment(sketch, "E78.1.1.23", {"start": v(-18800.5, 9760.51) * mm, "end": v(-18600.5, 9760.51) * mm});
            skLineSegment(sketch, "E78.2.0.0", {"start": v(-19150.5, 12760.51) * mm, "end": v(-19150.5, 12460.51) * mm});
            skLineSegment(sketch, "E78.2.0.1", {"start": v(-20150.5, 11660.51) * mm, "end": v(-20150.5, 11360.51) * mm});
            skLineSegment(sketch, "E78.2.0.2", {"start": v(-19450.5, 11360.51) * mm, "end": v(-19150.5, 11360.51) * mm});
            skLineSegment(sketch, "E78.2.0.3", {"start": v(-19150.5, 11660.51) * mm, "end": v(-19150.5, 11360.51) * mm});
            skLineSegment(sketch, "E78.2.0.4", {"start": v(-20150.5, 11360.51) * mm, "end": v(-19850.5, 11360.51) * mm});
            skLineSegment(sketch, "E78.2.0.5", {"start": v(-20150.5, 12760.51) * mm, "end": v(-20150.5, 12460.51) * mm});
            skLineSegment(sketch, "E78.2.0.6", {"start": v(-20050.5, 12460.51) * mm, "end": v(-20050.5, 12660.51) * mm});
            skLineSegment(sketch, "E78.2.0.7", {"start": v(-19250.5, 12460.51) * mm, "end": v(-19250.5, 12660.51) * mm});
            skLineSegment(sketch, "E78.2.0.8", {"start": v(-20050.5, 11660.51) * mm, "end": v(-20050.5, 11460.51) * mm});
            skLineSegment(sketch, "E78.2.0.9", {"start": v(-19850.5, 11460.51) * mm, "end": v(-19850.5, 11360.51) * mm});
            skLineSegment(sketch, "E78.2.0.10", {"start": v(-20050.5, 12660.51) * mm, "end": v(-19850.5, 12660.51) * mm});
            skLineSegment(sketch, "E78.2.0.11", {"start": v(-19450.5, 12660.51) * mm, "end": v(-19450.5, 12760.51) * mm});
            skLineSegment(sketch, "E78.2.0.12", {"start": v(-19250.5, 11460.51) * mm, "end": v(-19450.5, 11460.51) * mm});
            skLineSegment(sketch, "E78.2.0.13", {"start": v(-19450.5, 11460.51) * mm, "end": v(-19450.5, 11360.51) * mm});
            skLineSegment(sketch, "E78.2.0.14", {"start": v(-19850.5, 12660.51) * mm, "end": v(-19850.5, 12760.51) * mm});
            skLineSegment(sketch, "E78.2.0.15", {"start": v(-20150.5, 12460.51) * mm, "end": v(-20050.5, 12460.51) * mm});
            skLineSegment(sketch, "E78.2.0.16", {"start": v(-19150.5, 12460.51) * mm, "end": v(-19250.5, 12460.51) * mm});
            skLineSegment(sketch, "E78.2.0.17", {"start": v(-19250.5, 11660.51) * mm, "end": v(-19250.5, 11460.51) * mm});
            skLineSegment(sketch, "E78.2.0.18", {"start": v(-19250.5, 12660.51) * mm, "end": v(-19450.5, 12660.51) * mm});
            skLineSegment(sketch, "E78.2.0.19", {"start": v(-19450.5, 12760.51) * mm, "end": v(-19150.5, 12760.51) * mm});
            skLineSegment(sketch, "E78.2.0.20", {"start": v(-20150.5, 12760.51) * mm, "end": v(-19850.5, 12760.51) * mm});
            skLineSegment(sketch, "E78.2.0.21", {"start": v(-19150.5, 11660.51) * mm, "end": v(-19250.5, 11660.51) * mm});
            skLineSegment(sketch, "E78.2.0.22", {"start": v(-20150.5, 11660.51) * mm, "end": v(-20050.5, 11660.51) * mm});
            skLineSegment(sketch, "E78.2.0.23", {"start": v(-20050.5, 11460.51) * mm, "end": v(-19850.5, 11460.51) * mm});
            skLineSegment(sketch, "E78.2.1.0", {"start": v(-19150.5, 11060.51) * mm, "end": v(-19150.5, 10760.51) * mm});
            skLineSegment(sketch, "E78.2.1.1", {"start": v(-20150.5, 9960.51) * mm, "end": v(-20150.5, 9660.51) * mm});
            skLineSegment(sketch, "E78.2.1.2", {"start": v(-19450.5, 9660.51) * mm, "end": v(-19150.5, 9660.51) * mm});
            skLineSegment(sketch, "E78.2.1.3", {"start": v(-19150.5, 9960.51) * mm, "end": v(-19150.5, 9660.51) * mm});
            skLineSegment(sketch, "E78.2.1.4", {"start": v(-20150.5, 9660.51) * mm, "end": v(-19850.5, 9660.51) * mm});
            skLineSegment(sketch, "E78.2.1.5", {"start": v(-20150.5, 11060.51) * mm, "end": v(-20150.5, 10760.51) * mm});
            skLineSegment(sketch, "E78.2.1.6", {"start": v(-20050.5, 10760.51) * mm, "end": v(-20050.5, 10960.51) * mm});
            skLineSegment(sketch, "E78.2.1.7", {"start": v(-19250.5, 10760.51) * mm, "end": v(-19250.5, 10960.51) * mm});
            skLineSegment(sketch, "E78.2.1.8", {"start": v(-20050.5, 9960.51) * mm, "end": v(-20050.5, 9760.51) * mm});
            skLineSegment(sketch, "E78.2.1.9", {"start": v(-19850.5, 9760.51) * mm, "end": v(-19850.5, 9660.51) * mm});
            skLineSegment(sketch, "E78.2.1.10", {"start": v(-20050.5, 10960.51) * mm, "end": v(-19850.5, 10960.51) * mm});
            skLineSegment(sketch, "E78.2.1.11", {"start": v(-19450.5, 10960.51) * mm, "end": v(-19450.5, 11060.51) * mm});
            skLineSegment(sketch, "E78.2.1.12", {"start": v(-19250.5, 9760.51) * mm, "end": v(-19450.5, 9760.51) * mm});
            skLineSegment(sketch, "E78.2.1.13", {"start": v(-19450.5, 9760.51) * mm, "end": v(-19450.5, 9660.51) * mm});
            skLineSegment(sketch, "E78.2.1.14", {"start": v(-19850.5, 10960.51) * mm, "end": v(-19850.5, 11060.51) * mm});
            skLineSegment(sketch, "E78.2.1.15", {"start": v(-20150.5, 10760.51) * mm, "end": v(-20050.5, 10760.51) * mm});
            skLineSegment(sketch, "E78.2.1.16", {"start": v(-19150.5, 10760.51) * mm, "end": v(-19250.5, 10760.51) * mm});
            skLineSegment(sketch, "E78.2.1.17", {"start": v(-19250.5, 9960.51) * mm, "end": v(-19250.5, 9760.51) * mm});
            skLineSegment(sketch, "E78.2.1.18", {"start": v(-19250.5, 10960.51) * mm, "end": v(-19450.5, 10960.51) * mm});
            skLineSegment(sketch, "E78.2.1.19", {"start": v(-19450.5, 11060.51) * mm, "end": v(-19150.5, 11060.51) * mm});
            skLineSegment(sketch, "E78.2.1.20", {"start": v(-20150.5, 11060.51) * mm, "end": v(-19850.5, 11060.51) * mm});
            skLineSegment(sketch, "E78.2.1.21", {"start": v(-19150.5, 9960.51) * mm, "end": v(-19250.5, 9960.51) * mm});
            skLineSegment(sketch, "E78.2.1.22", {"start": v(-20150.5, 9960.51) * mm, "end": v(-20050.5, 9960.51) * mm});
            skLineSegment(sketch, "E78.2.1.23", {"start": v(-20050.5, 9760.51) * mm, "end": v(-19850.5, 9760.51) * mm});
            skLineSegment(sketch, "E78.direction1", {"start": v(-17650.5, 11360.51) * mm, "end": v(-18900.5, 11360.51) * mm, "construction": true});
            skLineSegment(sketch, "E78.direction2", {"start": v(-17650.5, 11360.51) * mm, "end": v(-17650.5, 9660.51) * mm, "construction": true});
            skLineSegment(sketch, "E79.bottom", {"start": v(-2591.77, 12523.56) * mm, "end": v(-1391.77, 12523.56) * mm});
            skLineSegment(sketch, "E79.top", {"start": v(-2591.77, 8723.56) * mm, "end": v(-1391.77, 8723.56) * mm});
            skLineSegment(sketch, "E79.left", {"start": v(-2591.77, 12523.56) * mm, "end": v(-2591.77, 8723.56) * mm});
            skLineSegment(sketch, "E79.right", {"start": v(-1391.77, 12523.56) * mm, "end": v(-1391.77, 8723.56) * mm});
            skLineSegment(sketch, "E80.bottom", {"start": v(-978.64, 11242.13) * mm, "end": v(-178.64, 11242.13) * mm});
            skLineSegment(sketch, "E80.top", {"start": v(-978.64, 9442.13) * mm, "end": v(-178.64, 9442.13) * mm});
            skLineSegment(sketch, "E80.left", {"start": v(-978.64, 11242.13) * mm, "end": v(-978.64, 9442.13) * mm});
            skLineSegment(sketch, "E80.right", {"start": v(-178.64, 11242.13) * mm, "end": v(-178.64, 9442.13) * mm});
            skLineSegment(sketch, "E81.bottom", {"start": v(-2790.64, 13280.12) * mm, "end": v(-2400.62, 13280.12) * mm});
            skLineSegment(sketch, "E81.top", {"start": v(-2790.64, 13092.25) * mm, "end": v(-2400.62, 13092.25) * mm});
            skLineSegment(sketch, "E81.left", {"start": v(-2790.64, 13280.12) * mm, "end": v(-2790.64, 13092.25) * mm});
            skLineSegment(sketch, "E81.right", {"start": v(-2400.62, 13280.12) * mm, "end": v(-2400.62, 13092.25) * mm});
            skSolve(sketch);
        }
        {
            var Q0;
            Q0=makeQuery(id+"F2.imprint","IMPRINT",FACE,{"disambiguationData":[TD([[makeQuery(id+"F2.imprint","IMPRINT",EDGE,{"derivedFrom":sQuery(id+"F2.wireOp",EDGE,"E37.0.1.0")}),1.0]])]});
            var Q1;
            Q1=makeQuery(id+"F2.imprint","IMPRINT",FACE,{"disambiguationData":[TD([[makeQuery(id+"F2.imprint","IMPRINT",EDGE,{"derivedFrom":sQuery(id+"F2.wireOp",EDGE,"E37.0.1.2")}),1.0]])]});
            var Q2;
            Q2=makeQuery(id+"F2.imprint","IMPRINT",FACE,{"disambiguationData":[TD([[makeQuery(id+"F2.imprint","IMPRINT",EDGE,{"derivedFrom":sQuery(id+"F2.wireOp",EDGE,"E37.0.1.3")}),-1.0]])]});
            var Q3;
            Q3=makeQuery(id+"F2.imprint","IMPRINT",FACE,{"disambiguationData":[TD([[makeQuery(id+"F2.imprint","IMPRINT",EDGE,{"derivedFrom":sQuery(id+"F2.wireOp",EDGE,"E38.bottom")}),-1.0]])]});
            var Q4;
            Q4=makeQuery(id+"F2.imprint","IMPRINT",FACE,{"disambiguationData":[TD([[makeQuery(id+"F2.imprint","IMPRINT",EDGE,{"derivedFrom":sQuery(id+"F2.wireOp",EDGE,"E41.bottom")}),1.0]])]});
            var Q5;
            Q5=makeQuery(id+"F2.imprint","IMPRINT",FACE,{"disambiguationData":[TD([[makeQuery(id+"F2.imprint","IMPRINT",EDGE,{"derivedFrom":sQuery(id+"F2.wireOp",EDGE,"E56.MirrorCS")}),1.0]])]});
            var Q6;
            Q6=makeQuery(id+"F2.imprint","IMPRINT",FACE,{"disambiguationData":[TD([[makeQuery(id+"F2.imprint","IMPRINT",EDGE,{"derivedFrom":sQuery(id+"F2.wireOp",EDGE,"E64.0.1.0")}),-1.0]])]});
            var Q7;
            Q7=makeQuery(id+"F2.imprint","IMPRINT",FACE,{"disambiguationData":[TD([[makeQuery(id+"F2.imprint","IMPRINT",EDGE,{"derivedFrom":sQuery(id+"F2.wireOp",EDGE,"E64.0.1.1")}),1.0]])]});
            var Q8;
            Q8=makeQuery(id+"F2.imprint","IMPRINT",FACE,{"disambiguationData":[TD([[makeQuery(id+"F2.imprint","IMPRINT",EDGE,{"derivedFrom":sQuery(id+"F2.wireOp",EDGE,"E64.0.1.2")}),1.0]])]});
            var Q9;
            Q9=makeQuery(id+"F2.imprint","IMPRINT",FACE,{"disambiguationData":[TD([[makeQuery(id+"F2.imprint","IMPRINT",EDGE,{"derivedFrom":sQuery(id+"F2.wireOp",EDGE,"E64.0.1.6")}),1.0]])]});
            var Q10;
            Q10=makeQuery(id+"F2.imprint","IMPRINT",FACE,{"disambiguationData":[TD([[makeQuery(id+"F2.imprint","IMPRINT",EDGE,{"derivedFrom":sQuery(id+"F2.wireOp",EDGE,"E64.1.0.0")}),-1.0]])]});
            var Q11;
            Q11=makeQuery(id+"F2.imprint","IMPRINT",FACE,{"disambiguationData":[TD([[makeQuery(id+"F2.imprint","IMPRINT",EDGE,{"derivedFrom":sQuery(id+"F2.wireOp",EDGE,"E64.1.0.1")}),1.0]])]});
            var Q12;
            Q12=makeQuery(id+"F2.imprint","IMPRINT",FACE,{"disambiguationData":[TD([[makeQuery(id+"F2.imprint","IMPRINT",EDGE,{"derivedFrom":sQuery(id+"F2.wireOp",EDGE,"E64.1.0.2")}),1.0]])]});
            var Q13;
            Q13=makeQuery(id+"F2.imprint","IMPRINT",FACE,{"disambiguationData":[TD([[makeQuery(id+"F2.imprint","IMPRINT",EDGE,{"derivedFrom":sQuery(id+"F2.wireOp",EDGE,"E64.1.0.6")}),1.0]])]});
            var Q14;
            Q14=makeQuery(id+"F2.imprint","IMPRINT",FACE,{"disambiguationData":[TD([[makeQuery(id+"F2.imprint","IMPRINT",EDGE,{"derivedFrom":sQuery(id+"F2.wireOp",EDGE,"E64.1.1.0")}),-1.0]])]});
            var Q15;
            Q15=makeQuery(id+"F2.imprint","IMPRINT",FACE,{"disambiguationData":[TD([[makeQuery(id+"F2.imprint","IMPRINT",EDGE,{"derivedFrom":sQuery(id+"F2.wireOp",EDGE,"E64.1.1.1")}),1.0]])]});
            var Q16;
            Q16=makeQuery(id+"F2.imprint","IMPRINT",FACE,{"disambiguationData":[TD([[makeQuery(id+"F2.imprint","IMPRINT",EDGE,{"derivedFrom":sQuery(id+"F2.wireOp",EDGE,"E64.1.1.2")}),1.0]])]});
            var Q17;
            Q17=makeQuery(id+"F2.imprint","IMPRINT",FACE,{"disambiguationData":[TD([[makeQuery(id+"F2.imprint","IMPRINT",EDGE,{"derivedFrom":sQuery(id+"F2.wireOp",EDGE,"E64.1.1.6")}),1.0]])]});
            var Q18;
            Q18=makeQuery(id+"F2.imprint","IMPRINT",FACE,{"disambiguationData":[TD([[makeQuery(id+"F2.imprint","IMPRINT",EDGE,{"derivedFrom":sQuery(id+"F2.wireOp",EDGE,"E64.2.0.0")}),-1.0]])]});
            var Q19;
            Q19=makeQuery(id+"F2.imprint","IMPRINT",FACE,{"disambiguationData":[TD([[makeQuery(id+"F2.imprint","IMPRINT",EDGE,{"derivedFrom":sQuery(id+"F2.wireOp",EDGE,"E64.2.0.1")}),1.0]])]});
            var Q20;
            Q20=makeQuery(id+"F2.imprint","IMPRINT",FACE,{"disambiguationData":[TD([[makeQuery(id+"F2.imprint","IMPRINT",EDGE,{"derivedFrom":sQuery(id+"F2.wireOp",EDGE,"E64.2.0.2")}),1.0]])]});
            var Q21;
            Q21=makeQuery(id+"F2.imprint","IMPRINT",FACE,{"disambiguationData":[TD([[makeQuery(id+"F2.imprint","IMPRINT",EDGE,{"derivedFrom":sQuery(id+"F2.wireOp",EDGE,"E64.2.0.6")}),1.0]])]});
            var Q22;
            Q22=makeQuery(id+"F2.imprint","IMPRINT",FACE,{"disambiguationData":[TD([[makeQuery(id+"F2.imprint","IMPRINT",EDGE,{"derivedFrom":sQuery(id+"F2.wireOp",EDGE,"E64.2.1.0")}),-1.0]])]});
            var Q23;
            Q23=makeQuery(id+"F2.imprint","IMPRINT",FACE,{"disambiguationData":[TD([[makeQuery(id+"F2.imprint","IMPRINT",EDGE,{"derivedFrom":sQuery(id+"F2.wireOp",EDGE,"E64.2.1.1")}),1.0]])]});
            var Q24;
            Q24=makeQuery(id+"F2.imprint","IMPRINT",FACE,{"disambiguationData":[TD([[makeQuery(id+"F2.imprint","IMPRINT",EDGE,{"derivedFrom":sQuery(id+"F2.wireOp",EDGE,"E64.2.1.2")}),1.0]])]});
            var Q25;
            Q25=makeQuery(id+"F2.imprint","IMPRINT",FACE,{"disambiguationData":[TD([[makeQuery(id+"F2.imprint","IMPRINT",EDGE,{"derivedFrom":sQuery(id+"F2.wireOp",EDGE,"E64.2.1.6")}),1.0]])]});
            var Q26;
            Q26=makeQuery(id+"F2.imprint","IMPRINT",FACE,{"disambiguationData":[TD([[makeQuery(id+"F2.imprint","IMPRINT",EDGE,{"derivedFrom":sQuery(id+"F2.wireOp",EDGE,"E64.3.0.0")}),-1.0]])]});
            var Q27;
            Q27=makeQuery(id+"F2.imprint","IMPRINT",FACE,{"disambiguationData":[TD([[makeQuery(id+"F2.imprint","IMPRINT",EDGE,{"derivedFrom":sQuery(id+"F2.wireOp",EDGE,"E64.3.0.1")}),1.0]])]});
            var Q28;
            Q28=makeQuery(id+"F2.imprint","IMPRINT",FACE,{"disambiguationData":[TD([[makeQuery(id+"F2.imprint","IMPRINT",EDGE,{"derivedFrom":sQuery(id+"F2.wireOp",EDGE,"E64.3.0.2")}),1.0]])]});
            var Q29;
            Q29=makeQuery(id+"F2.imprint","IMPRINT",FACE,{"disambiguationData":[TD([[makeQuery(id+"F2.imprint","IMPRINT",EDGE,{"derivedFrom":sQuery(id+"F2.wireOp",EDGE,"E64.3.0.6")}),1.0]])]});
            var Q30;
            Q30=makeQuery(id+"F2.imprint","IMPRINT",FACE,{"disambiguationData":[TD([[makeQuery(id+"F2.imprint","IMPRINT",EDGE,{"derivedFrom":sQuery(id+"F2.wireOp",EDGE,"E64.3.1.0")}),-1.0]])]});
            var Q31;
            Q31=makeQuery(id+"F2.imprint","IMPRINT",FACE,{"disambiguationData":[TD([[makeQuery(id+"F2.imprint","IMPRINT",EDGE,{"derivedFrom":sQuery(id+"F2.wireOp",EDGE,"E64.3.1.1")}),1.0]])]});
            var Q32;
            Q32=makeQuery(id+"F2.imprint","IMPRINT",FACE,{"disambiguationData":[TD([[makeQuery(id+"F2.imprint","IMPRINT",EDGE,{"derivedFrom":sQuery(id+"F2.wireOp",EDGE,"E64.3.1.2")}),1.0]])]});
            var Q33;
            Q33=makeQuery(id+"F2.imprint","IMPRINT",FACE,{"disambiguationData":[TD([[makeQuery(id+"F2.imprint","IMPRINT",EDGE,{"derivedFrom":sQuery(id+"F2.wireOp",EDGE,"E64.3.1.6")}),1.0]])]});
            var Q34;
            Q34=makeQuery(id+"F2.imprint","IMPRINT",FACE,{"disambiguationData":[TD([[makeQuery(id+"F2.imprint","IMPRINT",EDGE,{"derivedFrom":sQuery(id+"F2.wireOp",EDGE,"E64.4.0.0")}),-1.0]])]});
            var Q35;
            Q35=makeQuery(id+"F2.imprint","IMPRINT",FACE,{"disambiguationData":[TD([[makeQuery(id+"F2.imprint","IMPRINT",EDGE,{"derivedFrom":sQuery(id+"F2.wireOp",EDGE,"E64.4.0.1")}),1.0]])]});
            var Q36;
            Q36=makeQuery(id+"F2.imprint","IMPRINT",FACE,{"disambiguationData":[TD([[makeQuery(id+"F2.imprint","IMPRINT",EDGE,{"derivedFrom":sQuery(id+"F2.wireOp",EDGE,"E64.4.0.2")}),1.0]])]});
            var Q37;
            Q37=makeQuery(id+"F2.imprint","IMPRINT",FACE,{"disambiguationData":[TD([[makeQuery(id+"F2.imprint","IMPRINT",EDGE,{"derivedFrom":sQuery(id+"F2.wireOp",EDGE,"E64.4.0.6")}),1.0]])]});
            var Q38;
            Q38=makeQuery(id+"F2.imprint","IMPRINT",FACE,{"disambiguationData":[TD([[makeQuery(id+"F2.imprint","IMPRINT",EDGE,{"derivedFrom":sQuery(id+"F2.wireOp",EDGE,"E64.4.1.0")}),-1.0]])]});
            var Q39;
            Q39=makeQuery(id+"F2.imprint","IMPRINT",FACE,{"disambiguationData":[TD([[makeQuery(id+"F2.imprint","IMPRINT",EDGE,{"derivedFrom":sQuery(id+"F2.wireOp",EDGE,"E64.4.1.1")}),1.0]])]});
            var Q40;
            Q40=makeQuery(id+"F2.imprint","IMPRINT",FACE,{"disambiguationData":[TD([[makeQuery(id+"F2.imprint","IMPRINT",EDGE,{"derivedFrom":sQuery(id+"F2.wireOp",EDGE,"E64.4.1.2")}),1.0]])]});
            var Q41;
            Q41=makeQuery(id+"F2.imprint","IMPRINT",FACE,{"disambiguationData":[TD([[makeQuery(id+"F2.imprint","IMPRINT",EDGE,{"derivedFrom":sQuery(id+"F2.wireOp",EDGE,"E64.4.1.6")}),1.0]])]});
            var Q42;
            Q42=makeQuery(id+"F2.imprint","IMPRINT",FACE,{"disambiguationData":[TD([[makeQuery(id+"F2.imprint","IMPRINT",EDGE,{"derivedFrom":sQuery(id+"F2.wireOp",EDGE,"E65.4.0.0")}),-1.0]])]});
            var Q43;
            Q43=makeQuery(id+"F2.imprint","IMPRINT",FACE,{"disambiguationData":[TD([[makeQuery(id+"F2.imprint","IMPRINT",EDGE,{"derivedFrom":sQuery(id+"F2.wireOp",EDGE,"E65.4.0.1")}),1.0]])]});
            var Q44;
            Q44=makeQuery(id+"F2.imprint","IMPRINT",FACE,{"disambiguationData":[TD([[makeQuery(id+"F2.imprint","IMPRINT",EDGE,{"derivedFrom":sQuery(id+"F2.wireOp",EDGE,"E65.4.0.2")}),1.0]])]});
            var Q45;
            Q45=makeQuery(id+"F2.imprint","IMPRINT",FACE,{"disambiguationData":[TD([[makeQuery(id+"F2.imprint","IMPRINT",EDGE,{"derivedFrom":sQuery(id+"F2.wireOp",EDGE,"E65.4.0.6")}),1.0]])]});
            var Q46;
            Q46=makeQuery(id+"F2.imprint","IMPRINT",FACE,{"disambiguationData":[TD([[makeQuery(id+"F2.imprint","IMPRINT",EDGE,{"derivedFrom":sQuery(id+"F2.wireOp",EDGE,"E66.0.1.0")}),-1.0]])]});
            var Q47;
            Q47=makeQuery(id+"F2.imprint","IMPRINT",FACE,{"disambiguationData":[TD([[makeQuery(id+"F2.imprint","IMPRINT",EDGE,{"derivedFrom":sQuery(id+"F2.wireOp",EDGE,"E66.0.1.1")}),1.0]])]});
            var Q48;
            Q48=makeQuery(id+"F2.imprint","IMPRINT",FACE,{"disambiguationData":[TD([[makeQuery(id+"F2.imprint","IMPRINT",EDGE,{"derivedFrom":sQuery(id+"F2.wireOp",EDGE,"E66.0.1.3")}),-1.0]])]});
            var Q49;
            Q49=makeQuery(id+"F2.imprint","IMPRINT",FACE,{"disambiguationData":[TD([[makeQuery(id+"F2.imprint","IMPRINT",EDGE,{"derivedFrom":sQuery(id+"F2.wireOp",EDGE,"E66.0.1.5")}),-1.0]])]});
            var Q50;
            Q50=makeQuery(id+"F2.imprint","IMPRINT",FACE,{"disambiguationData":[TD([[makeQuery(id+"F2.imprint","IMPRINT",EDGE,{"derivedFrom":sQuery(id+"F2.wireOp",EDGE,"E66.1.0.0")}),-1.0]])]});
            var Q51;
            Q51=makeQuery(id+"F2.imprint","IMPRINT",FACE,{"disambiguationData":[TD([[makeQuery(id+"F2.imprint","IMPRINT",EDGE,{"derivedFrom":sQuery(id+"F2.wireOp",EDGE,"E66.1.0.1")}),1.0]])]});
            var Q52;
            Q52=makeQuery(id+"F2.imprint","IMPRINT",FACE,{"disambiguationData":[TD([[makeQuery(id+"F2.imprint","IMPRINT",EDGE,{"derivedFrom":sQuery(id+"F2.wireOp",EDGE,"E66.1.0.3")}),-1.0]])]});
            var Q53;
            Q53=makeQuery(id+"F2.imprint","IMPRINT",FACE,{"disambiguationData":[TD([[makeQuery(id+"F2.imprint","IMPRINT",EDGE,{"derivedFrom":sQuery(id+"F2.wireOp",EDGE,"E66.1.0.5")}),-1.0]])]});
            var Q54;
            Q54=makeQuery(id+"F2.imprint","IMPRINT",FACE,{"disambiguationData":[TD([[makeQuery(id+"F2.imprint","IMPRINT",EDGE,{"derivedFrom":sQuery(id+"F2.wireOp",EDGE,"E66.1.1.0")}),-1.0]])]});
            var Q55;
            Q55=makeQuery(id+"F2.imprint","IMPRINT",FACE,{"disambiguationData":[TD([[makeQuery(id+"F2.imprint","IMPRINT",EDGE,{"derivedFrom":sQuery(id+"F2.wireOp",EDGE,"E66.1.1.1")}),1.0]])]});
            var Q56;
            Q56=makeQuery(id+"F2.imprint","IMPRINT",FACE,{"disambiguationData":[TD([[makeQuery(id+"F2.imprint","IMPRINT",EDGE,{"derivedFrom":sQuery(id+"F2.wireOp",EDGE,"E66.1.1.3")}),-1.0]])]});
            var Q57;
            Q57=makeQuery(id+"F2.imprint","IMPRINT",FACE,{"disambiguationData":[TD([[makeQuery(id+"F2.imprint","IMPRINT",EDGE,{"derivedFrom":sQuery(id+"F2.wireOp",EDGE,"E66.1.1.5")}),-1.0]])]});
            var Q58;
            Q58=makeQuery(id+"F2.imprint","IMPRINT",FACE,{"disambiguationData":[TD([[makeQuery(id+"F2.imprint","IMPRINT",EDGE,{"derivedFrom":sQuery(id+"F2.wireOp",EDGE,"E66.2.0.0")}),-1.0]])]});
            var Q59;
            Q59=makeQuery(id+"F2.imprint","IMPRINT",FACE,{"disambiguationData":[TD([[makeQuery(id+"F2.imprint","IMPRINT",EDGE,{"derivedFrom":sQuery(id+"F2.wireOp",EDGE,"E66.2.0.1")}),1.0]])]});
            var Q60;
            Q60=makeQuery(id+"F2.imprint","IMPRINT",FACE,{"disambiguationData":[TD([[makeQuery(id+"F2.imprint","IMPRINT",EDGE,{"derivedFrom":sQuery(id+"F2.wireOp",EDGE,"E66.2.0.3")}),-1.0]])]});
            var Q61;
            Q61=makeQuery(id+"F2.imprint","IMPRINT",FACE,{"disambiguationData":[TD([[makeQuery(id+"F2.imprint","IMPRINT",EDGE,{"derivedFrom":sQuery(id+"F2.wireOp",EDGE,"E66.2.0.5")}),-1.0]])]});
            var Q62;
            Q62=makeQuery(id+"F2.imprint","IMPRINT",FACE,{"disambiguationData":[TD([[makeQuery(id+"F2.imprint","IMPRINT",EDGE,{"derivedFrom":sQuery(id+"F2.wireOp",EDGE,"E66.2.1.0")}),-1.0]])]});
            var Q63;
            Q63=makeQuery(id+"F2.imprint","IMPRINT",FACE,{"disambiguationData":[TD([[makeQuery(id+"F2.imprint","IMPRINT",EDGE,{"derivedFrom":sQuery(id+"F2.wireOp",EDGE,"E66.2.1.1")}),1.0]])]});
            var Q64;
            Q64=makeQuery(id+"F2.imprint","IMPRINT",FACE,{"disambiguationData":[TD([[makeQuery(id+"F2.imprint","IMPRINT",EDGE,{"derivedFrom":sQuery(id+"F2.wireOp",EDGE,"E66.2.1.3")}),-1.0]])]});
            var Q65;
            Q65=makeQuery(id+"F2.imprint","IMPRINT",FACE,{"disambiguationData":[TD([[makeQuery(id+"F2.imprint","IMPRINT",EDGE,{"derivedFrom":sQuery(id+"F2.wireOp",EDGE,"E66.2.1.5")}),-1.0]])]});
            var Q66;
            Q66=makeQuery(id+"F2.imprint","IMPRINT",FACE,{"disambiguationData":[TD([[makeQuery(id+"F2.imprint","IMPRINT",EDGE,{"derivedFrom":sQuery(id+"F2.wireOp",EDGE,"E66.3.0.0")}),-1.0]])]});
            var Q67;
            Q67=makeQuery(id+"F2.imprint","IMPRINT",FACE,{"disambiguationData":[TD([[makeQuery(id+"F2.imprint","IMPRINT",EDGE,{"derivedFrom":sQuery(id+"F2.wireOp",EDGE,"E66.3.0.1")}),1.0]])]});
            var Q68;
            Q68=makeQuery(id+"F2.imprint","IMPRINT",FACE,{"disambiguationData":[TD([[makeQuery(id+"F2.imprint","IMPRINT",EDGE,{"derivedFrom":sQuery(id+"F2.wireOp",EDGE,"E66.3.0.3")}),-1.0]])]});
            var Q69;
            Q69=makeQuery(id+"F2.imprint","IMPRINT",FACE,{"disambiguationData":[TD([[makeQuery(id+"F2.imprint","IMPRINT",EDGE,{"derivedFrom":sQuery(id+"F2.wireOp",EDGE,"E66.3.0.5")}),-1.0]])]});
            var Q70;
            Q70=makeQuery(id+"F2.imprint","IMPRINT",FACE,{"disambiguationData":[TD([[makeQuery(id+"F2.imprint","IMPRINT",EDGE,{"derivedFrom":sQuery(id+"F2.wireOp",EDGE,"E66.3.1.0")}),-1.0]])]});
            var Q71;
            Q71=makeQuery(id+"F2.imprint","IMPRINT",FACE,{"disambiguationData":[TD([[makeQuery(id+"F2.imprint","IMPRINT",EDGE,{"derivedFrom":sQuery(id+"F2.wireOp",EDGE,"E66.3.1.1")}),1.0]])]});
            var Q72;
            Q72=makeQuery(id+"F2.imprint","IMPRINT",FACE,{"disambiguationData":[TD([[makeQuery(id+"F2.imprint","IMPRINT",EDGE,{"derivedFrom":sQuery(id+"F2.wireOp",EDGE,"E66.3.1.3")}),-1.0]])]});
            var Q73;
            Q73=makeQuery(id+"F2.imprint","IMPRINT",FACE,{"disambiguationData":[TD([[makeQuery(id+"F2.imprint","IMPRINT",EDGE,{"derivedFrom":sQuery(id+"F2.wireOp",EDGE,"E66.3.1.5")}),-1.0]])]});
            var Q74;
            Q74=makeQuery(id+"F2.imprint","IMPRINT",FACE,{"disambiguationData":[TD([[makeQuery(id+"F2.imprint","IMPRINT",EDGE,{"derivedFrom":sQuery(id+"F2.wireOp",EDGE,"E77.3.0.0")}),-1.0]])]});
            var Q75;
            Q75=makeQuery(id+"F2.imprint","IMPRINT",FACE,{"disambiguationData":[TD([[makeQuery(id+"F2.imprint","IMPRINT",EDGE,{"derivedFrom":sQuery(id+"F2.wireOp",EDGE,"E77.3.0.1")}),1.0]])]});
            var Q76;
            Q76=makeQuery(id+"F2.imprint","IMPRINT",FACE,{"disambiguationData":[TD([[makeQuery(id+"F2.imprint","IMPRINT",EDGE,{"derivedFrom":sQuery(id+"F2.wireOp",EDGE,"E77.3.0.3")}),-1.0]])]});
            var Q77;
            Q77=makeQuery(id+"F2.imprint","IMPRINT",FACE,{"disambiguationData":[TD([[makeQuery(id+"F2.imprint","IMPRINT",EDGE,{"derivedFrom":sQuery(id+"F2.wireOp",EDGE,"E77.3.0.5")}),-1.0]])]});
            var Q78;
            Q78=makeQuery(id+"F2.imprint","IMPRINT",FACE,{"disambiguationData":[TD([[makeQuery(id+"F2.imprint","IMPRINT",EDGE,{"derivedFrom":sQuery(id+"F2.wireOp",EDGE,"E78.0.1.0")}),-1.0]])]});
            var Q79;
            Q79=makeQuery(id+"F2.imprint","IMPRINT",FACE,{"disambiguationData":[TD([[makeQuery(id+"F2.imprint","IMPRINT",EDGE,{"derivedFrom":sQuery(id+"F2.wireOp",EDGE,"E78.0.1.1")}),1.0]])]});
            var Q80;
            Q80=makeQuery(id+"F2.imprint","IMPRINT",FACE,{"disambiguationData":[TD([[makeQuery(id+"F2.imprint","IMPRINT",EDGE,{"derivedFrom":sQuery(id+"F2.wireOp",EDGE,"E78.0.1.2")}),1.0]])]});
            var Q81;
            Q81=makeQuery(id+"F2.imprint","IMPRINT",FACE,{"disambiguationData":[TD([[makeQuery(id+"F2.imprint","IMPRINT",EDGE,{"derivedFrom":sQuery(id+"F2.wireOp",EDGE,"E78.0.1.5")}),1.0]])]});
            var Q82;
            Q82=makeQuery(id+"F2.imprint","IMPRINT",FACE,{"disambiguationData":[TD([[makeQuery(id+"F2.imprint","IMPRINT",EDGE,{"derivedFrom":sQuery(id+"F2.wireOp",EDGE,"E78.1.0.0")}),-1.0]])]});
            var Q83;
            Q83=makeQuery(id+"F2.imprint","IMPRINT",FACE,{"disambiguationData":[TD([[makeQuery(id+"F2.imprint","IMPRINT",EDGE,{"derivedFrom":sQuery(id+"F2.wireOp",EDGE,"E78.1.0.1")}),1.0]])]});
            var Q84;
            Q84=makeQuery(id+"F2.imprint","IMPRINT",FACE,{"disambiguationData":[TD([[makeQuery(id+"F2.imprint","IMPRINT",EDGE,{"derivedFrom":sQuery(id+"F2.wireOp",EDGE,"E78.1.0.2")}),1.0]])]});
            var Q85;
            Q85=makeQuery(id+"F2.imprint","IMPRINT",FACE,{"disambiguationData":[TD([[makeQuery(id+"F2.imprint","IMPRINT",EDGE,{"derivedFrom":sQuery(id+"F2.wireOp",EDGE,"E78.1.0.5")}),1.0]])]});
            var Q86;
            Q86=makeQuery(id+"F2.imprint","IMPRINT",FACE,{"disambiguationData":[TD([[makeQuery(id+"F2.imprint","IMPRINT",EDGE,{"derivedFrom":sQuery(id+"F2.wireOp",EDGE,"E78.1.1.0")}),-1.0]])]});
            var Q87;
            Q87=makeQuery(id+"F2.imprint","IMPRINT",FACE,{"disambiguationData":[TD([[makeQuery(id+"F2.imprint","IMPRINT",EDGE,{"derivedFrom":sQuery(id+"F2.wireOp",EDGE,"E78.1.1.1")}),1.0]])]});
            var Q88;
            Q88=makeQuery(id+"F2.imprint","IMPRINT",FACE,{"disambiguationData":[TD([[makeQuery(id+"F2.imprint","IMPRINT",EDGE,{"derivedFrom":sQuery(id+"F2.wireOp",EDGE,"E78.1.1.2")}),1.0]])]});
            var Q89;
            Q89=makeQuery(id+"F2.imprint","IMPRINT",FACE,{"disambiguationData":[TD([[makeQuery(id+"F2.imprint","IMPRINT",EDGE,{"derivedFrom":sQuery(id+"F2.wireOp",EDGE,"E78.1.1.5")}),1.0]])]});
            var Q90;
            Q90=makeQuery(id+"F2.imprint","IMPRINT",FACE,{"disambiguationData":[TD([[makeQuery(id+"F2.imprint","IMPRINT",EDGE,{"derivedFrom":sQuery(id+"F2.wireOp",EDGE,"E78.2.0.0")}),-1.0]])]});
            var Q91;
            Q91=makeQuery(id+"F2.imprint","IMPRINT",FACE,{"disambiguationData":[TD([[makeQuery(id+"F2.imprint","IMPRINT",EDGE,{"derivedFrom":sQuery(id+"F2.wireOp",EDGE,"E78.2.0.1")}),1.0]])]});
            var Q92;
            Q92=makeQuery(id+"F2.imprint","IMPRINT",FACE,{"disambiguationData":[TD([[makeQuery(id+"F2.imprint","IMPRINT",EDGE,{"derivedFrom":sQuery(id+"F2.wireOp",EDGE,"E78.2.0.2")}),1.0]])]});
            var Q93;
            Q93=makeQuery(id+"F2.imprint","IMPRINT",FACE,{"disambiguationData":[TD([[makeQuery(id+"F2.imprint","IMPRINT",EDGE,{"derivedFrom":sQuery(id+"F2.wireOp",EDGE,"E78.2.0.5")}),1.0]])]});
            var Q94;
            Q94=makeQuery(id+"F2.imprint","IMPRINT",FACE,{"disambiguationData":[TD([[makeQuery(id+"F2.imprint","IMPRINT",EDGE,{"derivedFrom":sQuery(id+"F2.wireOp",EDGE,"E78.2.1.0")}),-1.0]])]});
            var Q95;
            Q95=makeQuery(id+"F2.imprint","IMPRINT",FACE,{"disambiguationData":[TD([[makeQuery(id+"F2.imprint","IMPRINT",EDGE,{"derivedFrom":sQuery(id+"F2.wireOp",EDGE,"E78.2.1.1")}),1.0]])]});
            var Q96;
            Q96=makeQuery(id+"F2.imprint","IMPRINT",FACE,{"disambiguationData":[TD([[makeQuery(id+"F2.imprint","IMPRINT",EDGE,{"derivedFrom":sQuery(id+"F2.wireOp",EDGE,"E78.2.1.2")}),1.0]])]});
            var Q97;
            Q97=makeQuery(id+"F2.imprint","IMPRINT",FACE,{"disambiguationData":[TD([[makeQuery(id+"F2.imprint","IMPRINT",EDGE,{"derivedFrom":sQuery(id+"F2.wireOp",EDGE,"E78.2.1.5")}),1.0]])]});
            var Q98;
            Q98=makeQuery(id+"F2.imprint","IMPRINT",FACE,{"disambiguationData":[TD([[makeQuery(id+"F2.imprint","IMPRINT",EDGE,{"derivedFrom":sQuery(id+"F2.wireOp",EDGE,"E39.bottom")}),-1.0]])]});
            var Q99;
            Q99=makeQuery(id+"F2.imprint","IMPRINT",FACE,{"disambiguationData":[TD([[makeQuery(id+"F2.imprint","IMPRINT",EDGE,{"derivedFrom":sQuery(id+"F2.wireOp",EDGE,"E40.bottom")}),-1.0]])]});
            var Q100;
            Q100=makeQuery(id+"F2.imprint","IMPRINT",FACE,{"disambiguationData":[TD([[makeQuery(id+"F2.imprint","IMPRINT",EDGE,{"derivedFrom":sQuery(id+"F2.wireOp",EDGE,"E42.bottom")}),-1.0]])]});
            var Q101;
            {var subQ0=sQuery(id+"F2.wireOp",EDGE,"E67");Q101=makeQuery(id+"F2.imprint","IMPRINT",FACE,{"disambiguationData":[TD([[makeQuery(id+"F2.imprint","IMPRINT",EDGE,{"derivedFrom":subQ0}),-1.0]])]});}
            var Q102;
            {var subQ0=sQuery(id+"F2.wireOp",EDGE,"E69");Q102=makeQuery(id+"F2.imprint","IMPRINT",FACE,{"disambiguationData":[TD([[makeQuery(id+"F2.imprint","IMPRINT",EDGE,{"derivedFrom":subQ0}),-1.0]])]});}
            var Q103;
            Q103=makeQuery(id+"F2.imprint","IMPRINT",FACE,{"disambiguationData":[TD([[makeQuery(id+"F2.imprint","IMPRINT",EDGE,{"derivedFrom":sQuery(id+"F2.wireOp",EDGE,"E72")}),-1.0]])]});
            var Q104;
            {var subQ0=sQuery(id+"F2.wireOp",EDGE,"E71.0.2.0");Q104=makeQuery(id+"F2.imprint","IMPRINT",FACE,{"disambiguationData":[TD([[makeQuery(id+"F2.imprint","IMPRINT",EDGE,{"derivedFrom":subQ0}),-1.0]])]});}
            var Q105;
            {var subQ0=sQuery(id+"F2.wireOp",EDGE,"E71.0.3.0");Q105=makeQuery(id+"F2.imprint","IMPRINT",FACE,{"disambiguationData":[TD([[makeQuery(id+"F2.imprint","IMPRINT",EDGE,{"derivedFrom":subQ0}),-1.0]])]});}
            var Q106;
            {var subQ3=sQuery(id+"F2.wireOp",EDGE,"E71.0.4.0");Q106=makeQuery(id+"F2.imprint","IMPRINT",FACE,{"disambiguationData":[TD([[makeQuery(id+"F2.imprint","IMPRINT",EDGE,{"derivedFrom":subQ3}),-1.0]])]});}
            var Q107;
            {var subQ0=sQuery(id+"F2.wireOp",EDGE,"E71.0.5.0");Q107=makeQuery(id+"F2.imprint","IMPRINT",FACE,{"disambiguationData":[TD([[makeQuery(id+"F2.imprint","IMPRINT",EDGE,{"derivedFrom":subQ0}),-1.0]])]});}
            var Q108;
            {var subQ0=sQuery(id+"F2.wireOp",EDGE,"E71.0.1.0");Q108=makeQuery(id+"F2.imprint","IMPRINT",FACE,{"disambiguationData":[TD([[makeQuery(id+"F2.imprint","IMPRINT",EDGE,{"derivedFrom":subQ0}),-1.0]])]});}
            extrude(context, id + "F3", {"entities" : qUnion([Q0, Q1, Q2, Q3, Q4, Q5, Q6, Q7, Q8, Q9, Q10, Q11, Q12, Q13, Q14, Q15, Q16, Q17, Q18, Q19, Q20, Q21, Q22, Q23, Q24, Q25, Q26, Q27, Q28, Q29, Q30, Q31, Q32, Q33, Q34, Q35, Q36, Q37, Q38, Q39, Q40, Q41, Q42, Q43, Q44, Q45, Q46, Q47, Q48, Q49, Q50, Q51, Q52, Q53, Q54, Q55, Q56, Q57, Q58, Q59, Q60, Q61, Q62, Q63, Q64, Q65, Q66, Q67, Q68, Q69, Q70, Q71, Q72, Q73, Q74, Q75, Q76, Q77, Q78, Q79, Q80, Q81, Q82, Q83, Q84, Q85, Q86, Q87, Q88, Q89, Q90, Q91, Q92, Q93, Q94, Q95, Q96, Q97, Q98, Q99, Q100, Q101, Q102, Q103, Q104, Q105, Q106, Q107, Q108]), "depth" : 25 * mm});
        }
        {
            var Q0;
            Q0=qCreatedBy(makeId("Top.planeOp"),FACE);
            var sketch = newSketch(context, id + "F4", { "sketchPlane" : qUnion([Q0])});
            skLineSegment(sketch, "E82.bottom", {"start": v(-10002.05, 6689.9) * mm, "end": v(-10602.05, 6689.9) * mm});
            skLineSegment(sketch, "E82.top", {"start": v(-10002.05, 6289.9) * mm, "end": v(-10602.05, 6289.9) * mm});
            skLineSegment(sketch, "E82.left", {"start": v(-10002.05, 6689.9) * mm, "end": v(-10002.05, 6289.9) * mm});
            skLineSegment(sketch, "E82.right", {"start": v(-10602.05, 6689.9) * mm, "end": v(-10602.05, 6289.9) * mm});
            skLineSegment(sketch, "E83.bottom", {"start": v(-10602.05, 6289.9) * mm, "end": v(-10002.05, 6289.9) * mm});
            skLineSegment(sketch, "E83.top", {"start": v(-10602.05, 5389.9) * mm, "end": v(-10002.05, 5389.9) * mm});
            skLineSegment(sketch, "E83.left", {"start": v(-10602.05, 6289.9) * mm, "end": v(-10602.05, 5389.9) * mm});
            skLineSegment(sketch, "E83.right", {"start": v(-10002.05, 6289.9) * mm, "end": v(-10002.05, 5389.9) * mm});
            skLineSegment(sketch, "E84.bottom", {"start": v(-9999.8, 3389.9) * mm, "end": v(-10799.8, 3389.9) * mm});
            skLineSegment(sketch, "E84.top", {"start": v(-9999.8, 1789.9) * mm, "end": v(-10799.8, 1789.9) * mm});
            skLineSegment(sketch, "E84.left", {"start": v(-9999.8, 3389.9) * mm, "end": v(-9999.8, 1789.9) * mm});
            skLineSegment(sketch, "E84.right", {"start": v(-10799.8, 3389.9) * mm, "end": v(-10799.8, 1789.9) * mm});
            skLineSegment(sketch, "E85.0", {"start": v(-13050, 4925.02) * mm, "end": v(-12750, 4925.02) * mm});
            skLineSegment(sketch, "E86.0", {"start": v(-13050, 4925.02) * mm, "end": v(-13050, 4625.02) * mm});
            skCircle(sketch, "E87", {"center": v(-11116.18, 2550.32) * mm, "radius": 256.58 * mm});
            skCircle(sketch, "E88.MirrorC", {"center": v(-12643.22, 2550.32) * mm, "radius": 256.58 * mm});
            skLineSegment(sketch, "E89.MirrorCS", {"start": v(-13757.63, 1789.9) * mm, "end": v(-12959.6, 1789.9) * mm});
            skLineSegment(sketch, "E90.MirrorCS", {"start": v(-13759.6, 3389.9) * mm, "end": v(-13759.6, 1789.9) * mm});
            skLineSegment(sketch, "E91.MirrorCS", {"start": v(-12959.6, 3389.9) * mm, "end": v(-12959.6, 1789.9) * mm});
            skLineSegment(sketch, "E92.MirrorCS", {"start": v(-13755.8, 3389.9) * mm, "end": v(-12959.6, 3389.9) * mm});
            skLineSegment(sketch, "E93.left", {"start": v(-13759.6, 1789.9) * mm, "end": v(-13759.6, 3389.9) * mm});
            skLineSegment(sketch, "E94.bottom", {"start": v(-13759.6, 1789.9) * mm, "end": v(-14559.6, 1789.9) * mm});
            skLineSegment(sketch, "E94.top", {"start": v(-13759.6, 3389.9) * mm, "end": v(-14559.6, 3389.9) * mm});
            skLineSegment(sketch, "E94.right", {"start": v(-14559.6, 1789.9) * mm, "end": v(-14559.6, 3389.9) * mm});
            skCircle(sketch, "E95.MirrorC", {"center": v(-14875.97, 2550.32) * mm, "radius": 256.58 * mm});
            skLineSegment(sketch, "E96", {"start": v(-13050, 4625.02) * mm, "end": v(-12950, 4625.02) * mm});
            skLineSegment(sketch, "E97", {"start": v(-12950, 4625.02) * mm, "end": v(-12950, 4825.02) * mm});
            skLineSegment(sketch, "E98", {"start": v(-12950, 4825.02) * mm, "end": v(-12750, 4825.02) * mm});
            skLineSegment(sketch, "E99", {"start": v(-12750, 4825.02) * mm, "end": v(-12750, 4925.02) * mm});
            skLineSegment(sketch, "E100.MirrorCS", {"start": v(-12050, 4625.02) * mm, "end": v(-12150, 4625.02) * mm});
            skLineSegment(sketch, "E101.MirrorCS", {"start": v(-12050, 4925.02) * mm, "end": v(-12050, 4625.02) * mm});
            skLineSegment(sketch, "E102.MirrorCS", {"start": v(-12150, 4625.02) * mm, "end": v(-12150, 4825.02) * mm});
            skLineSegment(sketch, "E103.MirrorCS", {"start": v(-12350, 4825.02) * mm, "end": v(-12350, 4925.02) * mm});
            skLineSegment(sketch, "E104.MirrorCS", {"start": v(-12150, 4825.02) * mm, "end": v(-12350, 4825.02) * mm});
            skLineSegment(sketch, "E105.MirrorCS", {"start": v(-12050, 4925.02) * mm, "end": v(-12350, 4925.02) * mm});
            skLineSegment(sketch, "E106.MirrorCS", {"start": v(-12150, 3825.02) * mm, "end": v(-12150, 3625.02) * mm});
            skLineSegment(sketch, "E107.MirrorCS", {"start": v(-13050, 3525.02) * mm, "end": v(-13050, 3825.02) * mm});
            skLineSegment(sketch, "E108.MirrorCS", {"start": v(-13050, 3525.02) * mm, "end": v(-12750, 3525.02) * mm});
            skLineSegment(sketch, "E109.MirrorCS", {"start": v(-12350, 3625.02) * mm, "end": v(-12350, 3525.02) * mm});
            skLineSegment(sketch, "E110.MirrorCS", {"start": v(-12050, 3825.02) * mm, "end": v(-12150, 3825.02) * mm});
            skLineSegment(sketch, "E111.MirrorCS", {"start": v(-12050, 3525.02) * mm, "end": v(-12350, 3525.02) * mm});
            skLineSegment(sketch, "E112.MirrorCS", {"start": v(-12950, 3825.02) * mm, "end": v(-12950, 3625.02) * mm});
            skLineSegment(sketch, "E113.MirrorCS", {"start": v(-12050, 3525.02) * mm, "end": v(-12050, 3825.02) * mm});
            skLineSegment(sketch, "E114.MirrorCS", {"start": v(-12150, 3625.02) * mm, "end": v(-12350, 3625.02) * mm});
            skLineSegment(sketch, "E115.MirrorCS", {"start": v(-13050, 3825.02) * mm, "end": v(-12950, 3825.02) * mm});
            skLineSegment(sketch, "E116.MirrorCS", {"start": v(-12750, 3625.02) * mm, "end": v(-12750, 3525.02) * mm});
            skLineSegment(sketch, "E117.MirrorCS", {"start": v(-12950, 3625.02) * mm, "end": v(-12750, 3625.02) * mm});
            skLineSegment(sketch, "E118.0.1.0", {"start": v(-12150, 375.02) * mm, "end": v(-12350, 375.02) * mm});
            skLineSegment(sketch, "E118.0.1.1", {"start": v(-13050, 1675.02) * mm, "end": v(-13050, 1375.02) * mm});
            skLineSegment(sketch, "E118.0.1.2", {"start": v(-12050, 275.02) * mm, "end": v(-12050, 575.02) * mm});
            skLineSegment(sketch, "E118.0.1.3", {"start": v(-12950, 575.02) * mm, "end": v(-12950, 375.02) * mm});
            skLineSegment(sketch, "E118.0.1.4", {"start": v(-13050, 1675.02) * mm, "end": v(-12750, 1675.02) * mm});
            skLineSegment(sketch, "E118.0.1.5", {"start": v(-12950, 375.02) * mm, "end": v(-12750, 375.02) * mm});
            skLineSegment(sketch, "E118.0.1.6", {"start": v(-13050, 275.02) * mm, "end": v(-12750, 275.02) * mm});
            skLineSegment(sketch, "E118.0.1.7", {"start": v(-12150, 575.02) * mm, "end": v(-12150, 375.02) * mm});
            skLineSegment(sketch, "E118.0.1.8", {"start": v(-12150, 1575.02) * mm, "end": v(-12350, 1575.02) * mm});
            skLineSegment(sketch, "E118.0.1.9", {"start": v(-13050, 275.02) * mm, "end": v(-13050, 575.02) * mm});
            skLineSegment(sketch, "E118.0.1.10", {"start": v(-12050, 1675.02) * mm, "end": v(-12350, 1675.02) * mm});
            skLineSegment(sketch, "E118.0.1.11", {"start": v(-12050, 275.02) * mm, "end": v(-12350, 275.02) * mm});
            skLineSegment(sketch, "E118.0.1.12", {"start": v(-12950, 1575.02) * mm, "end": v(-12750, 1575.02) * mm});
            skLineSegment(sketch, "E118.0.1.13", {"start": v(-12050, 1675.02) * mm, "end": v(-12050, 1375.02) * mm});
            skLineSegment(sketch, "E118.0.1.14", {"start": v(-12950, 1375.02) * mm, "end": v(-12950, 1575.02) * mm});
            skLineSegment(sketch, "E118.0.1.15", {"start": v(-12150, 1375.02) * mm, "end": v(-12150, 1575.02) * mm});
            skLineSegment(sketch, "E118.0.1.16", {"start": v(-13050, 575.02) * mm, "end": v(-12950, 575.02) * mm});
            skLineSegment(sketch, "E118.0.1.17", {"start": v(-12350, 375.02) * mm, "end": v(-12350, 275.02) * mm});
            skLineSegment(sketch, "E118.0.1.18", {"start": v(-12050, 1375.02) * mm, "end": v(-12150, 1375.02) * mm});
            skLineSegment(sketch, "E118.0.1.19", {"start": v(-12350, 1575.02) * mm, "end": v(-12350, 1675.02) * mm});
            skLineSegment(sketch, "E118.0.1.20", {"start": v(-12750, 375.02) * mm, "end": v(-12750, 275.02) * mm});
            skLineSegment(sketch, "E118.0.1.21", {"start": v(-12750, 1575.02) * mm, "end": v(-12750, 1675.02) * mm});
            skLineSegment(sketch, "E118.0.1.22", {"start": v(-13050, 1375.02) * mm, "end": v(-12950, 1375.02) * mm});
            skLineSegment(sketch, "E118.0.1.23", {"start": v(-12050, 575.02) * mm, "end": v(-12150, 575.02) * mm});
            skLineSegment(sketch, "E118.1.0.0", {"start": v(-10800, 3625.02) * mm, "end": v(-11000, 3625.02) * mm});
            skLineSegment(sketch, "E118.1.0.1", {"start": v(-11700, 4925.02) * mm, "end": v(-11700, 4625.02) * mm});
            skLineSegment(sketch, "E118.1.0.2", {"start": v(-10700, 3525.02) * mm, "end": v(-10700, 3825.02) * mm});
            skLineSegment(sketch, "E118.1.0.3", {"start": v(-11600, 3825.02) * mm, "end": v(-11600, 3625.02) * mm});
            skLineSegment(sketch, "E118.1.0.4", {"start": v(-11700, 4925.02) * mm, "end": v(-11400, 4925.02) * mm});
            skLineSegment(sketch, "E118.1.0.5", {"start": v(-11600, 3625.02) * mm, "end": v(-11400, 3625.02) * mm});
            skLineSegment(sketch, "E118.1.0.6", {"start": v(-11700, 3525.02) * mm, "end": v(-11400, 3525.02) * mm});
            skLineSegment(sketch, "E118.1.0.7", {"start": v(-10800, 3825.02) * mm, "end": v(-10800, 3625.02) * mm});
            skLineSegment(sketch, "E118.1.0.8", {"start": v(-10800, 4825.02) * mm, "end": v(-11000, 4825.02) * mm});
            skLineSegment(sketch, "E118.1.0.9", {"start": v(-11700, 3525.02) * mm, "end": v(-11700, 3825.02) * mm});
            skLineSegment(sketch, "E118.1.0.10", {"start": v(-10700, 4925.02) * mm, "end": v(-11000, 4925.02) * mm});
            skLineSegment(sketch, "E118.1.0.11", {"start": v(-10700, 3525.02) * mm, "end": v(-11000, 3525.02) * mm});
            skLineSegment(sketch, "E118.1.0.12", {"start": v(-11600, 4825.02) * mm, "end": v(-11400, 4825.02) * mm});
            skLineSegment(sketch, "E118.1.0.13", {"start": v(-10700, 4925.02) * mm, "end": v(-10700, 4625.02) * mm});
            skLineSegment(sketch, "E118.1.0.14", {"start": v(-11600, 4625.02) * mm, "end": v(-11600, 4825.02) * mm});
            skLineSegment(sketch, "E118.1.0.15", {"start": v(-10800, 4625.02) * mm, "end": v(-10800, 4825.02) * mm});
            skLineSegment(sketch, "E118.1.0.16", {"start": v(-11700, 3825.02) * mm, "end": v(-11600, 3825.02) * mm});
            skLineSegment(sketch, "E118.1.0.17", {"start": v(-11000, 3625.02) * mm, "end": v(-11000, 3525.02) * mm});
            skLineSegment(sketch, "E118.1.0.18", {"start": v(-10700, 4625.02) * mm, "end": v(-10800, 4625.02) * mm});
            skLineSegment(sketch, "E118.1.0.19", {"start": v(-11000, 4825.02) * mm, "end": v(-11000, 4925.02) * mm});
            skLineSegment(sketch, "E118.1.0.20", {"start": v(-11400, 3625.02) * mm, "end": v(-11400, 3525.02) * mm});
            skLineSegment(sketch, "E118.1.0.21", {"start": v(-11400, 4825.02) * mm, "end": v(-11400, 4925.02) * mm});
            skLineSegment(sketch, "E118.1.0.22", {"start": v(-11700, 4625.02) * mm, "end": v(-11600, 4625.02) * mm});
            skLineSegment(sketch, "E118.1.0.23", {"start": v(-10700, 3825.02) * mm, "end": v(-10800, 3825.02) * mm});
            skLineSegment(sketch, "E118.1.1.0", {"start": v(-10800, 375.02) * mm, "end": v(-11000, 375.02) * mm});
            skLineSegment(sketch, "E118.1.1.1", {"start": v(-11700, 1675.02) * mm, "end": v(-11700, 1375.02) * mm});
            skLineSegment(sketch, "E118.1.1.2", {"start": v(-10700, 275.02) * mm, "end": v(-10700, 575.02) * mm});
            skLineSegment(sketch, "E118.1.1.3", {"start": v(-11600, 575.02) * mm, "end": v(-11600, 375.02) * mm});
            skLineSegment(sketch, "E118.1.1.4", {"start": v(-11700, 1675.02) * mm, "end": v(-11400, 1675.02) * mm});
            skLineSegment(sketch, "E118.1.1.5", {"start": v(-11600, 375.02) * mm, "end": v(-11400, 375.02) * mm});
            skLineSegment(sketch, "E118.1.1.6", {"start": v(-11700, 275.02) * mm, "end": v(-11400, 275.02) * mm});
            skLineSegment(sketch, "E118.1.1.7", {"start": v(-10800, 575.02) * mm, "end": v(-10800, 375.02) * mm});
            skLineSegment(sketch, "E118.1.1.8", {"start": v(-10800, 1575.02) * mm, "end": v(-11000, 1575.02) * mm});
            skLineSegment(sketch, "E118.1.1.9", {"start": v(-11700, 275.02) * mm, "end": v(-11700, 575.02) * mm});
            skLineSegment(sketch, "E118.1.1.10", {"start": v(-10700, 1675.02) * mm, "end": v(-11000, 1675.02) * mm});
            skLineSegment(sketch, "E118.1.1.11", {"start": v(-10700, 275.02) * mm, "end": v(-11000, 275.02) * mm});
            skLineSegment(sketch, "E118.1.1.12", {"start": v(-11600, 1575.02) * mm, "end": v(-11400, 1575.02) * mm});
            skLineSegment(sketch, "E118.1.1.13", {"start": v(-10700, 1675.02) * mm, "end": v(-10700, 1375.02) * mm});
            skLineSegment(sketch, "E118.1.1.14", {"start": v(-11600, 1375.02) * mm, "end": v(-11600, 1575.02) * mm});
            skLineSegment(sketch, "E118.1.1.15", {"start": v(-10800, 1375.02) * mm, "end": v(-10800, 1575.02) * mm});
            skLineSegment(sketch, "E118.1.1.16", {"start": v(-11700, 575.02) * mm, "end": v(-11600, 575.02) * mm});
            skLineSegment(sketch, "E118.1.1.17", {"start": v(-11000, 375.02) * mm, "end": v(-11000, 275.02) * mm});
            skLineSegment(sketch, "E118.1.1.18", {"start": v(-10700, 1375.02) * mm, "end": v(-10800, 1375.02) * mm});
            skLineSegment(sketch, "E118.1.1.19", {"start": v(-11000, 1575.02) * mm, "end": v(-11000, 1675.02) * mm});
            skLineSegment(sketch, "E118.1.1.20", {"start": v(-11400, 375.02) * mm, "end": v(-11400, 275.02) * mm});
            skLineSegment(sketch, "E118.1.1.21", {"start": v(-11400, 1575.02) * mm, "end": v(-11400, 1675.02) * mm});
            skLineSegment(sketch, "E118.1.1.22", {"start": v(-11700, 1375.02) * mm, "end": v(-11600, 1375.02) * mm});
            skLineSegment(sketch, "E118.1.1.23", {"start": v(-10700, 575.02) * mm, "end": v(-10800, 575.02) * mm});
            skLineSegment(sketch, "E119.1.0.0", {"start": v(-17953.2, 1789.9) * mm, "end": v(-17159.6, 1789.9) * mm});
            skLineSegment(sketch, "E119.1.0.1", {"start": v(-17959.6, 1789.9) * mm, "end": v(-18759.6, 1789.9) * mm});
            skLineSegment(sketch, "E119.1.0.2", {"start": v(-17959.6, 1789.9) * mm, "end": v(-17959.6, 3389.9) * mm});
            skCircle(sketch, "E119.1.0.3", {"center": v(-16843.22, 2550.32) * mm, "radius": 256.58 * mm});
            skLineSegment(sketch, "E119.1.0.4", {"start": v(-17159.6, 3389.9) * mm, "end": v(-17159.6, 1789.9) * mm});
            skLineSegment(sketch, "E119.1.0.5", {"start": v(-17953.2, 3389.9) * mm, "end": v(-17159.6, 3389.9) * mm});
            skLineSegment(sketch, "E119.1.0.6", {"start": v(-17959.6, 3389.9) * mm, "end": v(-18759.6, 3389.9) * mm});
            skCircle(sketch, "E119.1.0.7", {"center": v(-19075.97, 2550.32) * mm, "radius": 256.58 * mm});
            skLineSegment(sketch, "E119.1.0.8", {"start": v(-18759.6, 1789.9) * mm, "end": v(-18759.6, 3389.9) * mm});
            skLineSegment(sketch, "E119.1.0.9", {"start": v(-17959.6, 1789.9) * mm, "end": v(-17959.6, 3389.9) * mm});
            skLineSegment(sketch, "E119.1.0.10", {"start": v(-17959.6, 3389.9) * mm, "end": v(-17959.6, 1789.9) * mm});
            skLineSegment(sketch, "E119.2.0.0", {"start": v(-22141.24, 1789.9) * mm, "end": v(-21359.6, 1789.9) * mm});
            skLineSegment(sketch, "E119.2.0.1", {"start": v(-22159.6, 1789.9) * mm, "end": v(-22959.6, 1789.9) * mm});
            skLineSegment(sketch, "E119.2.0.2", {"start": v(-22159.6, 1789.9) * mm, "end": v(-22159.6, 3389.9) * mm});
            skCircle(sketch, "E119.2.0.3", {"center": v(-21043.22, 2550.32) * mm, "radius": 256.58 * mm});
            skLineSegment(sketch, "E119.2.0.4", {"start": v(-21359.6, 3389.9) * mm, "end": v(-21359.6, 1789.9) * mm});
            skLineSegment(sketch, "E119.2.0.5", {"start": v(-22141.24, 3389.9) * mm, "end": v(-21359.6, 3389.9) * mm});
            skLineSegment(sketch, "E119.2.0.6", {"start": v(-22159.6, 3389.9) * mm, "end": v(-22959.6, 3389.9) * mm});
            skCircle(sketch, "E119.2.0.7", {"center": v(-23275.97, 2550.32) * mm, "radius": 256.58 * mm});
            skLineSegment(sketch, "E119.2.0.8", {"start": v(-22959.6, 1789.9) * mm, "end": v(-22959.6, 3389.9) * mm});
            skLineSegment(sketch, "E119.2.0.9", {"start": v(-22159.6, 1789.9) * mm, "end": v(-22159.6, 3389.9) * mm});
            skLineSegment(sketch, "E119.2.0.10", {"start": v(-22159.6, 3389.9) * mm, "end": v(-22159.6, 1789.9) * mm});
            skLineSegment(sketch, "E120.1.0.0", {"start": v(-15700, 4925.02) * mm, "end": v(-15700, 4625.02) * mm});
            skLineSegment(sketch, "E120.1.0.1", {"start": v(-17050, 4925.02) * mm, "end": v(-16750, 4925.02) * mm});
            skLineSegment(sketch, "E120.1.0.2", {"start": v(-17050, 3825.02) * mm, "end": v(-16950, 3825.02) * mm});
            skLineSegment(sketch, "E120.1.0.3", {"start": v(-15700, 4625.02) * mm, "end": v(-15600, 4625.02) * mm});
            skLineSegment(sketch, "E120.1.0.4", {"start": v(-16050, 4925.02) * mm, "end": v(-16050, 4625.02) * mm});
            skLineSegment(sketch, "E120.1.0.5", {"start": v(-16150, 4625.02) * mm, "end": v(-16150, 4825.02) * mm});
            skLineSegment(sketch, "E120.1.0.6", {"start": v(-16150, 3625.02) * mm, "end": v(-16350, 3625.02) * mm});
            skLineSegment(sketch, "E120.1.0.7", {"start": v(-15400, 3625.02) * mm, "end": v(-15400, 3525.02) * mm});
            skLineSegment(sketch, "E120.1.0.8", {"start": v(-15700, 3825.02) * mm, "end": v(-15600, 3825.02) * mm});
            skLineSegment(sketch, "E120.1.0.9", {"start": v(-16050, 3825.02) * mm, "end": v(-16150, 3825.02) * mm});
            skLineSegment(sketch, "E120.1.0.10", {"start": v(-16050, 3525.02) * mm, "end": v(-16350, 3525.02) * mm});
            skLineSegment(sketch, "E120.1.0.11", {"start": v(-16150, 4825.02) * mm, "end": v(-16350, 4825.02) * mm});
            skLineSegment(sketch, "E120.1.0.12", {"start": v(-14700, 4925.02) * mm, "end": v(-14700, 4625.02) * mm});
            skLineSegment(sketch, "E120.1.0.13", {"start": v(-14800, 4625.02) * mm, "end": v(-14800, 4825.02) * mm});
            skLineSegment(sketch, "E120.1.0.14", {"start": v(-15700, 3525.02) * mm, "end": v(-15400, 3525.02) * mm});
            skLineSegment(sketch, "E120.1.0.15", {"start": v(-15600, 3625.02) * mm, "end": v(-15400, 3625.02) * mm});
            skLineSegment(sketch, "E120.1.0.16", {"start": v(-16750, 4825.02) * mm, "end": v(-16750, 4925.02) * mm});
            skLineSegment(sketch, "E120.1.0.17", {"start": v(-16050, 4925.02) * mm, "end": v(-16350, 4925.02) * mm});
            skLineSegment(sketch, "E120.1.0.18", {"start": v(-15600, 4825.02) * mm, "end": v(-15400, 4825.02) * mm});
            skLineSegment(sketch, "E120.1.0.19", {"start": v(-16950, 4825.02) * mm, "end": v(-16750, 4825.02) * mm});
            skLineSegment(sketch, "E120.1.0.20", {"start": v(-16350, 3625.02) * mm, "end": v(-16350, 3525.02) * mm});
            skLineSegment(sketch, "E120.1.0.21", {"start": v(-17050, 3525.02) * mm, "end": v(-17050, 3825.02) * mm});
            skLineSegment(sketch, "E120.1.0.22", {"start": v(-14800, 3825.02) * mm, "end": v(-14800, 3625.02) * mm});
            skLineSegment(sketch, "E120.1.0.23", {"start": v(-16050, 4625.02) * mm, "end": v(-16150, 4625.02) * mm});
            skLineSegment(sketch, "E120.1.0.24", {"start": v(-15600, 4625.02) * mm, "end": v(-15600, 4825.02) * mm});
            skLineSegment(sketch, "E120.1.0.25", {"start": v(-17050, 4625.02) * mm, "end": v(-16950, 4625.02) * mm});
            skLineSegment(sketch, "E120.1.0.26", {"start": v(-15400, 4825.02) * mm, "end": v(-15400, 4925.02) * mm});
            skLineSegment(sketch, "E120.1.0.27", {"start": v(-14700, 4625.02) * mm, "end": v(-14800, 4625.02) * mm});
            skLineSegment(sketch, "E120.1.0.28", {"start": v(-16350, 4825.02) * mm, "end": v(-16350, 4925.02) * mm});
            skLineSegment(sketch, "E120.1.0.29", {"start": v(-15600, 3825.02) * mm, "end": v(-15600, 3625.02) * mm});
            skLineSegment(sketch, "E120.1.0.30", {"start": v(-15000, 4825.02) * mm, "end": v(-15000, 4925.02) * mm});
            skLineSegment(sketch, "E120.1.0.31", {"start": v(-16950, 3825.02) * mm, "end": v(-16950, 3625.02) * mm});
            skLineSegment(sketch, "E120.1.0.32", {"start": v(-14700, 3525.02) * mm, "end": v(-14700, 3825.02) * mm});
            skLineSegment(sketch, "E120.1.0.33", {"start": v(-15700, 4925.02) * mm, "end": v(-15400, 4925.02) * mm});
            skLineSegment(sketch, "E120.1.0.34", {"start": v(-16050, 3525.02) * mm, "end": v(-16050, 3825.02) * mm});
            skLineSegment(sketch, "E120.1.0.35", {"start": v(-16950, 4625.02) * mm, "end": v(-16950, 4825.02) * mm});
            skLineSegment(sketch, "E120.1.0.36", {"start": v(-17050, 4925.02) * mm, "end": v(-17050, 4625.02) * mm});
            skLineSegment(sketch, "E120.1.0.37", {"start": v(-16150, 3825.02) * mm, "end": v(-16150, 3625.02) * mm});
            skLineSegment(sketch, "E120.1.0.38", {"start": v(-16750, 3625.02) * mm, "end": v(-16750, 3525.02) * mm});
            skLineSegment(sketch, "E120.1.0.39", {"start": v(-14800, 4825.02) * mm, "end": v(-15000, 4825.02) * mm});
            skLineSegment(sketch, "E120.1.0.40", {"start": v(-16950, 3625.02) * mm, "end": v(-16750, 3625.02) * mm});
            skLineSegment(sketch, "E120.1.0.41", {"start": v(-14700, 4925.02) * mm, "end": v(-15000, 4925.02) * mm});
            skLineSegment(sketch, "E120.1.0.42", {"start": v(-14800, 3625.02) * mm, "end": v(-15000, 3625.02) * mm});
            skLineSegment(sketch, "E120.1.0.43", {"start": v(-14700, 3825.02) * mm, "end": v(-14800, 3825.02) * mm});
            skLineSegment(sketch, "E120.1.0.44", {"start": v(-15700, 3525.02) * mm, "end": v(-15700, 3825.02) * mm});
            skLineSegment(sketch, "E120.1.0.45", {"start": v(-17050, 3525.02) * mm, "end": v(-16750, 3525.02) * mm});
            skLineSegment(sketch, "E120.1.0.46", {"start": v(-15000, 3625.02) * mm, "end": v(-15000, 3525.02) * mm});
            skLineSegment(sketch, "E120.1.0.47", {"start": v(-14700, 3525.02) * mm, "end": v(-15000, 3525.02) * mm});
            skLineSegment(sketch, "E120.1.0.48", {"start": v(-15600, 1375.02) * mm, "end": v(-15600, 1575.02) * mm});
            skLineSegment(sketch, "E120.1.0.49", {"start": v(-15600, 375.02) * mm, "end": v(-15400, 375.02) * mm});
            skLineSegment(sketch, "E120.1.0.50", {"start": v(-15700, 1375.02) * mm, "end": v(-15600, 1375.02) * mm});
            skLineSegment(sketch, "E120.1.0.51", {"start": v(-16950, 575.02) * mm, "end": v(-16950, 375.02) * mm});
            skLineSegment(sketch, "E120.1.0.52", {"start": v(-15700, 575.02) * mm, "end": v(-15600, 575.02) * mm});
            skLineSegment(sketch, "E120.1.0.53", {"start": v(-15600, 1575.02) * mm, "end": v(-15400, 1575.02) * mm});
            skLineSegment(sketch, "E120.1.0.54", {"start": v(-16150, 375.02) * mm, "end": v(-16350, 375.02) * mm});
            skLineSegment(sketch, "E120.1.0.55", {"start": v(-16050, 1675.02) * mm, "end": v(-16050, 1375.02) * mm});
            skLineSegment(sketch, "E120.1.0.56", {"start": v(-16750, 375.02) * mm, "end": v(-16750, 275.02) * mm});
            skLineSegment(sketch, "E120.1.0.57", {"start": v(-14800, 1375.02) * mm, "end": v(-14800, 1575.02) * mm});
            skLineSegment(sketch, "E120.1.0.58", {"start": v(-16350, 1575.02) * mm, "end": v(-16350, 1675.02) * mm});
            skLineSegment(sketch, "E120.1.0.59", {"start": v(-17050, 275.02) * mm, "end": v(-16750, 275.02) * mm});
            skLineSegment(sketch, "E120.1.0.60", {"start": v(-16950, 375.02) * mm, "end": v(-16750, 375.02) * mm});
            skLineSegment(sketch, "E120.1.0.61", {"start": v(-14700, 1675.02) * mm, "end": v(-14700, 1375.02) * mm});
            skLineSegment(sketch, "E120.1.0.62", {"start": v(-16150, 575.02) * mm, "end": v(-16150, 375.02) * mm});
            skLineSegment(sketch, "E120.1.0.63", {"start": v(-16150, 1575.02) * mm, "end": v(-16350, 1575.02) * mm});
            skLineSegment(sketch, "E120.1.0.64", {"start": v(-16050, 575.02) * mm, "end": v(-16150, 575.02) * mm});
            skLineSegment(sketch, "E120.1.0.65", {"start": v(-16050, 1375.02) * mm, "end": v(-16150, 1375.02) * mm});
            skLineSegment(sketch, "E120.1.0.66", {"start": v(-14800, 575.02) * mm, "end": v(-14800, 375.02) * mm});
            skLineSegment(sketch, "E120.1.0.67", {"start": v(-15600, 575.02) * mm, "end": v(-15600, 375.02) * mm});
            skLineSegment(sketch, "E120.1.0.68", {"start": v(-14700, 575.02) * mm, "end": v(-14800, 575.02) * mm});
            skLineSegment(sketch, "E120.1.0.69", {"start": v(-16750, 1575.02) * mm, "end": v(-16750, 1675.02) * mm});
            skLineSegment(sketch, "E120.1.0.70", {"start": v(-15400, 1575.02) * mm, "end": v(-15400, 1675.02) * mm});
            skLineSegment(sketch, "E120.1.0.71", {"start": v(-17050, 1375.02) * mm, "end": v(-16950, 1375.02) * mm});
            skLineSegment(sketch, "E120.1.0.72", {"start": v(-15000, 1575.02) * mm, "end": v(-15000, 1675.02) * mm});
            skLineSegment(sketch, "E120.1.0.73", {"start": v(-15700, 275.02) * mm, "end": v(-15400, 275.02) * mm});
            skLineSegment(sketch, "E120.1.0.74", {"start": v(-16950, 1375.02) * mm, "end": v(-16950, 1575.02) * mm});
            skLineSegment(sketch, "E120.1.0.75", {"start": v(-14800, 1575.02) * mm, "end": v(-15000, 1575.02) * mm});
            skLineSegment(sketch, "E120.1.0.76", {"start": v(-16950, 1575.02) * mm, "end": v(-16750, 1575.02) * mm});
            skLineSegment(sketch, "E120.1.0.77", {"start": v(-16350, 375.02) * mm, "end": v(-16350, 275.02) * mm});
            skLineSegment(sketch, "E120.1.0.78", {"start": v(-17050, 1675.02) * mm, "end": v(-17050, 1375.02) * mm});
            skLineSegment(sketch, "E120.1.0.79", {"start": v(-15000, 375.02) * mm, "end": v(-15000, 275.02) * mm});
            skLineSegment(sketch, "E120.1.0.80", {"start": v(-14700, 1375.02) * mm, "end": v(-14800, 1375.02) * mm});
            skLineSegment(sketch, "E120.1.0.81", {"start": v(-16050, 275.02) * mm, "end": v(-16350, 275.02) * mm});
            skLineSegment(sketch, "E120.1.0.82", {"start": v(-16050, 1675.02) * mm, "end": v(-16350, 1675.02) * mm});
            skLineSegment(sketch, "E120.1.0.83", {"start": v(-14700, 1675.02) * mm, "end": v(-15000, 1675.02) * mm});
            skLineSegment(sketch, "E120.1.0.84", {"start": v(-15700, 275.02) * mm, "end": v(-15700, 575.02) * mm});
            skLineSegment(sketch, "E120.1.0.85", {"start": v(-17050, 275.02) * mm, "end": v(-17050, 575.02) * mm});
            skLineSegment(sketch, "E120.1.0.86", {"start": v(-15400, 375.02) * mm, "end": v(-15400, 275.02) * mm});
            skLineSegment(sketch, "E120.1.0.87", {"start": v(-14700, 275.02) * mm, "end": v(-15000, 275.02) * mm});
            skLineSegment(sketch, "E120.1.0.88", {"start": v(-16050, 275.02) * mm, "end": v(-16050, 575.02) * mm});
            skLineSegment(sketch, "E120.1.0.89", {"start": v(-17050, 1675.02) * mm, "end": v(-16750, 1675.02) * mm});
            skLineSegment(sketch, "E120.1.0.90", {"start": v(-17050, 575.02) * mm, "end": v(-16950, 575.02) * mm});
            skLineSegment(sketch, "E120.1.0.91", {"start": v(-15700, 1675.02) * mm, "end": v(-15400, 1675.02) * mm});
            skLineSegment(sketch, "E120.1.0.92", {"start": v(-14700, 275.02) * mm, "end": v(-14700, 575.02) * mm});
            skLineSegment(sketch, "E120.1.0.93", {"start": v(-14800, 375.02) * mm, "end": v(-15000, 375.02) * mm});
            skLineSegment(sketch, "E120.1.0.94", {"start": v(-16150, 1375.02) * mm, "end": v(-16150, 1575.02) * mm});
            skLineSegment(sketch, "E120.1.0.95", {"start": v(-15700, 1675.02) * mm, "end": v(-15700, 1375.02) * mm});
            skLineSegment(sketch, "E121.1.0.0", {"start": v(-19900, 3825.02) * mm, "end": v(-19800, 3825.02) * mm});
            skLineSegment(sketch, "E121.1.0.1", {"start": v(-21250, 3525.02) * mm, "end": v(-20950, 3525.02) * mm});
            skLineSegment(sketch, "E121.1.0.2", {"start": v(-20350, 3625.02) * mm, "end": v(-20550, 3625.02) * mm});
            skLineSegment(sketch, "E121.1.0.3", {"start": v(-20350, 4625.02) * mm, "end": v(-20350, 4825.02) * mm});
            skLineSegment(sketch, "E121.1.0.4", {"start": v(-21150, 3625.02) * mm, "end": v(-20950, 3625.02) * mm});
            skLineSegment(sketch, "E121.1.0.5", {"start": v(-19800, 4625.02) * mm, "end": v(-19800, 4825.02) * mm});
            skLineSegment(sketch, "E121.1.0.6", {"start": v(-21250, 4925.02) * mm, "end": v(-20950, 4925.02) * mm});
            skLineSegment(sketch, "E121.1.0.7", {"start": v(-19000, 4625.02) * mm, "end": v(-19000, 4825.02) * mm});
            skLineSegment(sketch, "E121.1.0.8", {"start": v(-20250, 4625.02) * mm, "end": v(-20350, 4625.02) * mm});
            skLineSegment(sketch, "E121.1.0.9", {"start": v(-19800, 3825.02) * mm, "end": v(-19800, 3625.02) * mm});
            skLineSegment(sketch, "E121.1.0.10", {"start": v(-20950, 3625.02) * mm, "end": v(-20950, 3525.02) * mm});
            skLineSegment(sketch, "E121.1.0.11", {"start": v(-20250, 4925.02) * mm, "end": v(-20550, 4925.02) * mm});
            skLineSegment(sketch, "E121.1.0.12", {"start": v(-20350, 4825.02) * mm, "end": v(-20550, 4825.02) * mm});
            skLineSegment(sketch, "E121.1.0.13", {"start": v(-19600, 4825.02) * mm, "end": v(-19600, 4925.02) * mm});
            skLineSegment(sketch, "E121.1.0.14", {"start": v(-19800, 4825.02) * mm, "end": v(-19600, 4825.02) * mm});
            skLineSegment(sketch, "E121.1.0.15", {"start": v(-20250, 4925.02) * mm, "end": v(-20250, 4625.02) * mm});
            skLineSegment(sketch, "E121.1.0.16", {"start": v(-18900, 3825.02) * mm, "end": v(-19000, 3825.02) * mm});
            skLineSegment(sketch, "E121.1.0.17", {"start": v(-19000, 4825.02) * mm, "end": v(-19200, 4825.02) * mm});
            skLineSegment(sketch, "E121.1.0.18", {"start": v(-20550, 4825.02) * mm, "end": v(-20550, 4925.02) * mm});
            skLineSegment(sketch, "E121.1.0.19", {"start": v(-21250, 3525.02) * mm, "end": v(-21250, 3825.02) * mm});
            skLineSegment(sketch, "E121.1.0.20", {"start": v(-21250, 3825.02) * mm, "end": v(-21150, 3825.02) * mm});
            skLineSegment(sketch, "E121.1.0.21", {"start": v(-19900, 4925.02) * mm, "end": v(-19600, 4925.02) * mm});
            skLineSegment(sketch, "E121.1.0.22", {"start": v(-18900, 4625.02) * mm, "end": v(-19000, 4625.02) * mm});
            skLineSegment(sketch, "E121.1.0.23", {"start": v(-18900, 4925.02) * mm, "end": v(-18900, 4625.02) * mm});
            skLineSegment(sketch, "E121.1.0.24", {"start": v(-19900, 3525.02) * mm, "end": v(-19900, 3825.02) * mm});
            skLineSegment(sketch, "E121.1.0.25", {"start": v(-20250, 3525.02) * mm, "end": v(-20250, 3825.02) * mm});
            skLineSegment(sketch, "E121.1.0.26", {"start": v(-21250, 4625.02) * mm, "end": v(-21150, 4625.02) * mm});
            skLineSegment(sketch, "E121.1.0.27", {"start": v(-19900, 4625.02) * mm, "end": v(-19800, 4625.02) * mm});
            skLineSegment(sketch, "E121.1.0.28", {"start": v(-20950, 4825.02) * mm, "end": v(-20950, 4925.02) * mm});
            skLineSegment(sketch, "E121.1.0.29", {"start": v(-20250, 3525.02) * mm, "end": v(-20550, 3525.02) * mm});
            skLineSegment(sketch, "E121.1.0.30", {"start": v(-19800, 3625.02) * mm, "end": v(-19600, 3625.02) * mm});
            skLineSegment(sketch, "E121.1.0.31", {"start": v(-19900, 4925.02) * mm, "end": v(-19900, 4625.02) * mm});
            skLineSegment(sketch, "E121.1.0.32", {"start": v(-19200, 4825.02) * mm, "end": v(-19200, 4925.02) * mm});
            skLineSegment(sketch, "E121.1.0.33", {"start": v(-20350, 3825.02) * mm, "end": v(-20350, 3625.02) * mm});
            skLineSegment(sketch, "E121.1.0.34", {"start": v(-19900, 3525.02) * mm, "end": v(-19600, 3525.02) * mm});
            skLineSegment(sketch, "E121.1.0.35", {"start": v(-18900, 4925.02) * mm, "end": v(-19200, 4925.02) * mm});
            skLineSegment(sketch, "E121.1.0.36", {"start": v(-20250, 3825.02) * mm, "end": v(-20350, 3825.02) * mm});
            skLineSegment(sketch, "E121.1.0.37", {"start": v(-21150, 3825.02) * mm, "end": v(-21150, 3625.02) * mm});
            skLineSegment(sketch, "E121.1.0.38", {"start": v(-18900, 3525.02) * mm, "end": v(-19200, 3525.02) * mm});
            skLineSegment(sketch, "E121.1.0.39", {"start": v(-21150, 4825.02) * mm, "end": v(-20950, 4825.02) * mm});
            skLineSegment(sketch, "E121.1.0.40", {"start": v(-19200, 3625.02) * mm, "end": v(-19200, 3525.02) * mm});
            skLineSegment(sketch, "E121.1.0.41", {"start": v(-18900, 3525.02) * mm, "end": v(-18900, 3825.02) * mm});
            skLineSegment(sketch, "E121.1.0.42", {"start": v(-19600, 3625.02) * mm, "end": v(-19600, 3525.02) * mm});
            skLineSegment(sketch, "E121.1.0.43", {"start": v(-19000, 3825.02) * mm, "end": v(-19000, 3625.02) * mm});
            skLineSegment(sketch, "E121.1.0.44", {"start": v(-20550, 3625.02) * mm, "end": v(-20550, 3525.02) * mm});
            skLineSegment(sketch, "E121.1.0.45", {"start": v(-21250, 4925.02) * mm, "end": v(-21250, 4625.02) * mm});
            skLineSegment(sketch, "E121.1.0.46", {"start": v(-21150, 4625.02) * mm, "end": v(-21150, 4825.02) * mm});
            skLineSegment(sketch, "E121.1.0.47", {"start": v(-19000, 3625.02) * mm, "end": v(-19200, 3625.02) * mm});
            skLineSegment(sketch, "E121.1.0.48", {"start": v(-19900, 1675.02) * mm, "end": v(-19900, 1375.02) * mm});
            skLineSegment(sketch, "E121.1.0.49", {"start": v(-21250, 1375.02) * mm, "end": v(-21150, 1375.02) * mm});
            skLineSegment(sketch, "E121.1.0.50", {"start": v(-19600, 375.02) * mm, "end": v(-19600, 275.02) * mm});
            skLineSegment(sketch, "E121.1.0.51", {"start": v(-18900, 575.02) * mm, "end": v(-19000, 575.02) * mm});
            skLineSegment(sketch, "E121.1.0.52", {"start": v(-21150, 375.02) * mm, "end": v(-20950, 375.02) * mm});
            skLineSegment(sketch, "E121.1.0.53", {"start": v(-21250, 1675.02) * mm, "end": v(-21250, 1375.02) * mm});
            skLineSegment(sketch, "E121.1.0.54", {"start": v(-20250, 1675.02) * mm, "end": v(-20250, 1375.02) * mm});
            skLineSegment(sketch, "E121.1.0.55", {"start": v(-20350, 375.02) * mm, "end": v(-20550, 375.02) * mm});
            skLineSegment(sketch, "E121.1.0.56", {"start": v(-20250, 275.02) * mm, "end": v(-20550, 275.02) * mm});
            skLineSegment(sketch, "E121.1.0.57", {"start": v(-18900, 275.02) * mm, "end": v(-18900, 575.02) * mm});
            skLineSegment(sketch, "E121.1.0.58", {"start": v(-20250, 1675.02) * mm, "end": v(-20550, 1675.02) * mm});
            skLineSegment(sketch, "E121.1.0.59", {"start": v(-21150, 1375.02) * mm, "end": v(-21150, 1575.02) * mm});
            skLineSegment(sketch, "E121.1.0.60", {"start": v(-19000, 375.02) * mm, "end": v(-19200, 375.02) * mm});
            skLineSegment(sketch, "E121.1.0.61", {"start": v(-20550, 375.02) * mm, "end": v(-20550, 275.02) * mm});
            skLineSegment(sketch, "E121.1.0.62", {"start": v(-20950, 375.02) * mm, "end": v(-20950, 275.02) * mm});
            skLineSegment(sketch, "E121.1.0.63", {"start": v(-20250, 1375.02) * mm, "end": v(-20350, 1375.02) * mm});
            skLineSegment(sketch, "E121.1.0.64", {"start": v(-21250, 275.02) * mm, "end": v(-20950, 275.02) * mm});
            skLineSegment(sketch, "E121.1.0.65", {"start": v(-20250, 275.02) * mm, "end": v(-20250, 575.02) * mm});
            skLineSegment(sketch, "E121.1.0.66", {"start": v(-20350, 575.02) * mm, "end": v(-20350, 375.02) * mm});
            skLineSegment(sketch, "E121.1.0.67", {"start": v(-20350, 1375.02) * mm, "end": v(-20350, 1575.02) * mm});
            skLineSegment(sketch, "E121.1.0.68", {"start": v(-20250, 575.02) * mm, "end": v(-20350, 575.02) * mm});
            skLineSegment(sketch, "E121.1.0.69", {"start": v(-21250, 575.02) * mm, "end": v(-21150, 575.02) * mm});
            skLineSegment(sketch, "E121.1.0.70", {"start": v(-19200, 375.02) * mm, "end": v(-19200, 275.02) * mm});
            skLineSegment(sketch, "E121.1.0.71", {"start": v(-19900, 275.02) * mm, "end": v(-19600, 275.02) * mm});
            skLineSegment(sketch, "E121.1.0.72", {"start": v(-19900, 575.02) * mm, "end": v(-19800, 575.02) * mm});
            skLineSegment(sketch, "E121.1.0.73", {"start": v(-19800, 1375.02) * mm, "end": v(-19800, 1575.02) * mm});
            skLineSegment(sketch, "E121.1.0.74", {"start": v(-18900, 1375.02) * mm, "end": v(-19000, 1375.02) * mm});
            skLineSegment(sketch, "E121.1.0.75", {"start": v(-21150, 575.02) * mm, "end": v(-21150, 375.02) * mm});
            skLineSegment(sketch, "E121.1.0.76", {"start": v(-19000, 1575.02) * mm, "end": v(-19200, 1575.02) * mm});
            skLineSegment(sketch, "E121.1.0.77", {"start": v(-19900, 1375.02) * mm, "end": v(-19800, 1375.02) * mm});
            skLineSegment(sketch, "E121.1.0.78", {"start": v(-19600, 1575.02) * mm, "end": v(-19600, 1675.02) * mm});
            skLineSegment(sketch, "E121.1.0.79", {"start": v(-18900, 1675.02) * mm, "end": v(-19200, 1675.02) * mm});
            skLineSegment(sketch, "E121.1.0.80", {"start": v(-19000, 575.02) * mm, "end": v(-19000, 375.02) * mm});
            skLineSegment(sketch, "E121.1.0.81", {"start": v(-19800, 575.02) * mm, "end": v(-19800, 375.02) * mm});
            skLineSegment(sketch, "E121.1.0.82", {"start": v(-19800, 375.02) * mm, "end": v(-19600, 375.02) * mm});
            skLineSegment(sketch, "E121.1.0.83", {"start": v(-18900, 275.02) * mm, "end": v(-19200, 275.02) * mm});
            skLineSegment(sketch, "E121.1.0.84", {"start": v(-19900, 1675.02) * mm, "end": v(-19600, 1675.02) * mm});
            skLineSegment(sketch, "E121.1.0.85", {"start": v(-18900, 1675.02) * mm, "end": v(-18900, 1375.02) * mm});
            skLineSegment(sketch, "E121.1.0.86", {"start": v(-21150, 1575.02) * mm, "end": v(-20950, 1575.02) * mm});
            skLineSegment(sketch, "E121.1.0.87", {"start": v(-20350, 1575.02) * mm, "end": v(-20550, 1575.02) * mm});
            skLineSegment(sketch, "E121.1.0.88", {"start": v(-21250, 1675.02) * mm, "end": v(-20950, 1675.02) * mm});
            skLineSegment(sketch, "E121.1.0.89", {"start": v(-20950, 1575.02) * mm, "end": v(-20950, 1675.02) * mm});
            skLineSegment(sketch, "E121.1.0.90", {"start": v(-19900, 275.02) * mm, "end": v(-19900, 575.02) * mm});
            skLineSegment(sketch, "E121.1.0.91", {"start": v(-19000, 1375.02) * mm, "end": v(-19000, 1575.02) * mm});
            skLineSegment(sketch, "E121.1.0.92", {"start": v(-21250, 275.02) * mm, "end": v(-21250, 575.02) * mm});
            skLineSegment(sketch, "E121.1.0.93", {"start": v(-20550, 1575.02) * mm, "end": v(-20550, 1675.02) * mm});
            skLineSegment(sketch, "E121.1.0.94", {"start": v(-19800, 1575.02) * mm, "end": v(-19600, 1575.02) * mm});
            skLineSegment(sketch, "E121.1.0.95", {"start": v(-19200, 1575.02) * mm, "end": v(-19200, 1675.02) * mm});
            skLineSegment(sketch, "E121.2.0.0", {"start": v(-24100, 3825.02) * mm, "end": v(-24000, 3825.02) * mm});
            skLineSegment(sketch, "E121.2.0.1", {"start": v(-25450, 3525.02) * mm, "end": v(-25150, 3525.02) * mm});
            skLineSegment(sketch, "E121.2.0.2", {"start": v(-24550, 3625.02) * mm, "end": v(-24750, 3625.02) * mm});
            skLineSegment(sketch, "E121.2.0.3", {"start": v(-24550, 4625.02) * mm, "end": v(-24550, 4825.02) * mm});
            skLineSegment(sketch, "E121.2.0.4", {"start": v(-25350, 3625.02) * mm, "end": v(-25150, 3625.02) * mm});
            skLineSegment(sketch, "E121.2.0.5", {"start": v(-24000, 4625.02) * mm, "end": v(-24000, 4825.02) * mm});
            skLineSegment(sketch, "E121.2.0.6", {"start": v(-25450, 4925.02) * mm, "end": v(-25150, 4925.02) * mm});
            skLineSegment(sketch, "E121.2.0.7", {"start": v(-23200, 4625.02) * mm, "end": v(-23200, 4825.02) * mm});
            skLineSegment(sketch, "E121.2.0.8", {"start": v(-24450, 4625.02) * mm, "end": v(-24550, 4625.02) * mm});
            skLineSegment(sketch, "E121.2.0.9", {"start": v(-24000, 3825.02) * mm, "end": v(-24000, 3625.02) * mm});
            skLineSegment(sketch, "E121.2.0.10", {"start": v(-25150, 3625.02) * mm, "end": v(-25150, 3525.02) * mm});
            skLineSegment(sketch, "E121.2.0.11", {"start": v(-24450, 4925.02) * mm, "end": v(-24750, 4925.02) * mm});
            skLineSegment(sketch, "E121.2.0.12", {"start": v(-24550, 4825.02) * mm, "end": v(-24750, 4825.02) * mm});
            skLineSegment(sketch, "E121.2.0.13", {"start": v(-23800, 4825.02) * mm, "end": v(-23800, 4925.02) * mm});
            skLineSegment(sketch, "E121.2.0.14", {"start": v(-24000, 4825.02) * mm, "end": v(-23800, 4825.02) * mm});
            skLineSegment(sketch, "E121.2.0.15", {"start": v(-24450, 4925.02) * mm, "end": v(-24450, 4625.02) * mm});
            skLineSegment(sketch, "E121.2.0.16", {"start": v(-23100, 3825.02) * mm, "end": v(-23200, 3825.02) * mm});
            skLineSegment(sketch, "E121.2.0.17", {"start": v(-23200, 4825.02) * mm, "end": v(-23400, 4825.02) * mm});
            skLineSegment(sketch, "E121.2.0.18", {"start": v(-24750, 4825.02) * mm, "end": v(-24750, 4925.02) * mm});
            skLineSegment(sketch, "E121.2.0.19", {"start": v(-25450, 3525.02) * mm, "end": v(-25450, 3825.02) * mm});
            skLineSegment(sketch, "E121.2.0.20", {"start": v(-25450, 3825.02) * mm, "end": v(-25350, 3825.02) * mm});
            skLineSegment(sketch, "E121.2.0.21", {"start": v(-24100, 4925.02) * mm, "end": v(-23800, 4925.02) * mm});
            skLineSegment(sketch, "E121.2.0.22", {"start": v(-23100, 4625.02) * mm, "end": v(-23200, 4625.02) * mm});
            skLineSegment(sketch, "E121.2.0.23", {"start": v(-23100, 4925.02) * mm, "end": v(-23100, 4625.02) * mm});
            skLineSegment(sketch, "E121.2.0.24", {"start": v(-24100, 3525.02) * mm, "end": v(-24100, 3825.02) * mm});
            skLineSegment(sketch, "E121.2.0.25", {"start": v(-24450, 3525.02) * mm, "end": v(-24450, 3825.02) * mm});
            skLineSegment(sketch, "E121.2.0.26", {"start": v(-25450, 4625.02) * mm, "end": v(-25350, 4625.02) * mm});
            skLineSegment(sketch, "E121.2.0.27", {"start": v(-24100, 4625.02) * mm, "end": v(-24000, 4625.02) * mm});
            skLineSegment(sketch, "E121.2.0.28", {"start": v(-25150, 4825.02) * mm, "end": v(-25150, 4925.02) * mm});
            skLineSegment(sketch, "E121.2.0.29", {"start": v(-24450, 3525.02) * mm, "end": v(-24750, 3525.02) * mm});
            skLineSegment(sketch, "E121.2.0.30", {"start": v(-24000, 3625.02) * mm, "end": v(-23800, 3625.02) * mm});
            skLineSegment(sketch, "E121.2.0.31", {"start": v(-24100, 4925.02) * mm, "end": v(-24100, 4625.02) * mm});
            skLineSegment(sketch, "E121.2.0.32", {"start": v(-23400, 4825.02) * mm, "end": v(-23400, 4925.02) * mm});
            skLineSegment(sketch, "E121.2.0.33", {"start": v(-24550, 3825.02) * mm, "end": v(-24550, 3625.02) * mm});
            skLineSegment(sketch, "E121.2.0.34", {"start": v(-24100, 3525.02) * mm, "end": v(-23800, 3525.02) * mm});
            skLineSegment(sketch, "E121.2.0.35", {"start": v(-23100, 4925.02) * mm, "end": v(-23400, 4925.02) * mm});
            skLineSegment(sketch, "E121.2.0.36", {"start": v(-24450, 3825.02) * mm, "end": v(-24550, 3825.02) * mm});
            skLineSegment(sketch, "E121.2.0.37", {"start": v(-25350, 3825.02) * mm, "end": v(-25350, 3625.02) * mm});
            skLineSegment(sketch, "E121.2.0.38", {"start": v(-23100, 3525.02) * mm, "end": v(-23400, 3525.02) * mm});
            skLineSegment(sketch, "E121.2.0.39", {"start": v(-25350, 4825.02) * mm, "end": v(-25150, 4825.02) * mm});
            skLineSegment(sketch, "E121.2.0.40", {"start": v(-23400, 3625.02) * mm, "end": v(-23400, 3525.02) * mm});
            skLineSegment(sketch, "E121.2.0.41", {"start": v(-23100, 3525.02) * mm, "end": v(-23100, 3825.02) * mm});
            skLineSegment(sketch, "E121.2.0.42", {"start": v(-23800, 3625.02) * mm, "end": v(-23800, 3525.02) * mm});
            skLineSegment(sketch, "E121.2.0.43", {"start": v(-23200, 3825.02) * mm, "end": v(-23200, 3625.02) * mm});
            skLineSegment(sketch, "E121.2.0.44", {"start": v(-24750, 3625.02) * mm, "end": v(-24750, 3525.02) * mm});
            skLineSegment(sketch, "E121.2.0.45", {"start": v(-25450, 4925.02) * mm, "end": v(-25450, 4625.02) * mm});
            skLineSegment(sketch, "E121.2.0.46", {"start": v(-25350, 4625.02) * mm, "end": v(-25350, 4825.02) * mm});
            skLineSegment(sketch, "E121.2.0.47", {"start": v(-23200, 3625.02) * mm, "end": v(-23400, 3625.02) * mm});
            skLineSegment(sketch, "E121.2.0.48", {"start": v(-24100, 1675.02) * mm, "end": v(-24100, 1375.02) * mm});
            skLineSegment(sketch, "E121.2.0.49", {"start": v(-25450, 1375.02) * mm, "end": v(-25350, 1375.02) * mm});
            skLineSegment(sketch, "E121.2.0.50", {"start": v(-23800, 375.02) * mm, "end": v(-23800, 275.02) * mm});
            skLineSegment(sketch, "E121.2.0.51", {"start": v(-23100, 575.02) * mm, "end": v(-23200, 575.02) * mm});
            skLineSegment(sketch, "E121.2.0.52", {"start": v(-25350, 375.02) * mm, "end": v(-25150, 375.02) * mm});
            skLineSegment(sketch, "E121.2.0.53", {"start": v(-25450, 1675.02) * mm, "end": v(-25450, 1375.02) * mm});
            skLineSegment(sketch, "E121.2.0.54", {"start": v(-24450, 1675.02) * mm, "end": v(-24450, 1375.02) * mm});
            skLineSegment(sketch, "E121.2.0.55", {"start": v(-24550, 375.02) * mm, "end": v(-24750, 375.02) * mm});
            skLineSegment(sketch, "E121.2.0.56", {"start": v(-24450, 275.02) * mm, "end": v(-24750, 275.02) * mm});
            skLineSegment(sketch, "E121.2.0.57", {"start": v(-23100, 275.02) * mm, "end": v(-23100, 575.02) * mm});
            skLineSegment(sketch, "E121.2.0.58", {"start": v(-24450, 1675.02) * mm, "end": v(-24750, 1675.02) * mm});
            skLineSegment(sketch, "E121.2.0.59", {"start": v(-25350, 1375.02) * mm, "end": v(-25350, 1575.02) * mm});
            skLineSegment(sketch, "E121.2.0.60", {"start": v(-23200, 375.02) * mm, "end": v(-23400, 375.02) * mm});
            skLineSegment(sketch, "E121.2.0.61", {"start": v(-24750, 375.02) * mm, "end": v(-24750, 275.02) * mm});
            skLineSegment(sketch, "E121.2.0.62", {"start": v(-25150, 375.02) * mm, "end": v(-25150, 275.02) * mm});
            skLineSegment(sketch, "E121.2.0.63", {"start": v(-24450, 1375.02) * mm, "end": v(-24550, 1375.02) * mm});
            skLineSegment(sketch, "E121.2.0.64", {"start": v(-25450, 275.02) * mm, "end": v(-25150, 275.02) * mm});
            skLineSegment(sketch, "E121.2.0.65", {"start": v(-24450, 275.02) * mm, "end": v(-24450, 575.02) * mm});
            skLineSegment(sketch, "E121.2.0.66", {"start": v(-24550, 575.02) * mm, "end": v(-24550, 375.02) * mm});
            skLineSegment(sketch, "E121.2.0.67", {"start": v(-24550, 1375.02) * mm, "end": v(-24550, 1575.02) * mm});
            skLineSegment(sketch, "E121.2.0.68", {"start": v(-24450, 575.02) * mm, "end": v(-24550, 575.02) * mm});
            skLineSegment(sketch, "E121.2.0.69", {"start": v(-25450, 575.02) * mm, "end": v(-25350, 575.02) * mm});
            skLineSegment(sketch, "E121.2.0.70", {"start": v(-23400, 375.02) * mm, "end": v(-23400, 275.02) * mm});
            skLineSegment(sketch, "E121.2.0.71", {"start": v(-24100, 275.02) * mm, "end": v(-23800, 275.02) * mm});
            skLineSegment(sketch, "E121.2.0.72", {"start": v(-24100, 575.02) * mm, "end": v(-24000, 575.02) * mm});
            skLineSegment(sketch, "E121.2.0.73", {"start": v(-24000, 1375.02) * mm, "end": v(-24000, 1575.02) * mm});
            skLineSegment(sketch, "E121.2.0.74", {"start": v(-23100, 1375.02) * mm, "end": v(-23200, 1375.02) * mm});
            skLineSegment(sketch, "E121.2.0.75", {"start": v(-25350, 575.02) * mm, "end": v(-25350, 375.02) * mm});
            skLineSegment(sketch, "E121.2.0.76", {"start": v(-23200, 1575.02) * mm, "end": v(-23400, 1575.02) * mm});
            skLineSegment(sketch, "E121.2.0.77", {"start": v(-24100, 1375.02) * mm, "end": v(-24000, 1375.02) * mm});
            skLineSegment(sketch, "E121.2.0.78", {"start": v(-23800, 1575.02) * mm, "end": v(-23800, 1675.02) * mm});
            skLineSegment(sketch, "E121.2.0.79", {"start": v(-23100, 1675.02) * mm, "end": v(-23400, 1675.02) * mm});
            skLineSegment(sketch, "E121.2.0.80", {"start": v(-23200, 575.02) * mm, "end": v(-23200, 375.02) * mm});
            skLineSegment(sketch, "E121.2.0.81", {"start": v(-24000, 575.02) * mm, "end": v(-24000, 375.02) * mm});
            skLineSegment(sketch, "E121.2.0.82", {"start": v(-24000, 375.02) * mm, "end": v(-23800, 375.02) * mm});
            skLineSegment(sketch, "E121.2.0.83", {"start": v(-23100, 275.02) * mm, "end": v(-23400, 275.02) * mm});
            skLineSegment(sketch, "E121.2.0.84", {"start": v(-24100, 1675.02) * mm, "end": v(-23800, 1675.02) * mm});
            skLineSegment(sketch, "E121.2.0.85", {"start": v(-23100, 1675.02) * mm, "end": v(-23100, 1375.02) * mm});
            skLineSegment(sketch, "E121.2.0.86", {"start": v(-25350, 1575.02) * mm, "end": v(-25150, 1575.02) * mm});
            skLineSegment(sketch, "E121.2.0.87", {"start": v(-24550, 1575.02) * mm, "end": v(-24750, 1575.02) * mm});
            skLineSegment(sketch, "E121.2.0.88", {"start": v(-25450, 1675.02) * mm, "end": v(-25150, 1675.02) * mm});
            skLineSegment(sketch, "E121.2.0.89", {"start": v(-25150, 1575.02) * mm, "end": v(-25150, 1675.02) * mm});
            skLineSegment(sketch, "E121.2.0.90", {"start": v(-24100, 275.02) * mm, "end": v(-24100, 575.02) * mm});
            skLineSegment(sketch, "E121.2.0.91", {"start": v(-23200, 1375.02) * mm, "end": v(-23200, 1575.02) * mm});
            skLineSegment(sketch, "E121.2.0.92", {"start": v(-25450, 275.02) * mm, "end": v(-25450, 575.02) * mm});
            skLineSegment(sketch, "E121.2.0.93", {"start": v(-24750, 1575.02) * mm, "end": v(-24750, 1675.02) * mm});
            skLineSegment(sketch, "E121.2.0.94", {"start": v(-24000, 1575.02) * mm, "end": v(-23800, 1575.02) * mm});
            skLineSegment(sketch, "E121.2.0.95", {"start": v(-23400, 1575.02) * mm, "end": v(-23400, 1675.02) * mm});
            skLineSegment(sketch, "E122", {"start": v(-22141.24, 3389.9) * mm, "end": v(-22141.24, 1789.9) * mm});
            skLineSegment(sketch, "E123", {"start": v(-17953.2, 3389.9) * mm, "end": v(-17953.2, 1789.9) * mm});
            skLineSegment(sketch, "E124", {"start": v(-13755.8, 3389.9) * mm, "end": v(-13757.63, 1789.9) * mm});
            skLineSegment(sketch, "E125.2.0.1", {"start": v(-25559.6, 1789.9) * mm, "end": v(-26359.6, 1789.9) * mm});
            skLineSegment(sketch, "E125.2.0.2", {"start": v(-25559.6, 1789.9) * mm, "end": v(-25559.6, 3389.9) * mm});
            skLineSegment(sketch, "E125.2.0.6", {"start": v(-25559.6, 3389.9) * mm, "end": v(-26359.6, 3389.9) * mm});
            skCircle(sketch, "E125.2.0.7", {"center": v(-25170.84, 2589.93) * mm, "radius": 256.58 * mm});
            skLineSegment(sketch, "E125.2.0.8", {"start": v(-26359.6, 1789.9) * mm, "end": v(-26359.6, 3389.9) * mm});
            skSolve(sketch);
        }
        {
            var Q0;
            Q0 = qSketchRegion(id + "F4", true);
            extrude(context, id + "F5", {"entities" : qUnion([Q0]), "operationType" : NewBodyOperationType.ADD, "depth" : 25 * mm});
        }
        {
            var Q0;
            Q0=qCreatedBy(makeId("Top.planeOp"),FACE);
            var sketch = newSketch(context, id + "F6", { "sketchPlane" : qUnion([Q0])});
            skLineSegment(sketch, "E126.bottom", {"start": v(-22150.5, 11950) * mm, "end": v(-21350.5, 11950) * mm});
            skLineSegment(sketch, "E126.top", {"start": v(-22150.5, 10450) * mm, "end": v(-21350.5, 10450) * mm});
            skLineSegment(sketch, "E126.left", {"start": v(-22150.5, 11950) * mm, "end": v(-22150.5, 10450) * mm});
            skLineSegment(sketch, "E126.right", {"start": v(-21350.5, 11950) * mm, "end": v(-21350.5, 10450) * mm});
            skLineSegment(sketch, "E127.bottom", {"start": v(-25811.9, 11950) * mm, "end": v(-23850.5, 11950) * mm});
            skLineSegment(sketch, "E127.top", {"start": v(-25811.9, 11150) * mm, "end": v(-23850.5, 11150) * mm});
            skLineSegment(sketch, "E127.right", {"start": v(-23850.5, 11950) * mm, "end": v(-23850.5, 11150) * mm});
            skLineSegment(sketch, "E128.bottom", {"start": v(-25850.5, 11150) * mm, "end": v(-26350.5, 11150) * mm});
            skLineSegment(sketch, "E128.top", {"start": v(-25850.5, 13150) * mm, "end": v(-26350.5, 13150) * mm});
            skLineSegment(sketch, "E128.right", {"start": v(-26350.5, 11150) * mm, "end": v(-26350.5, 13150) * mm});
            skLineSegment(sketch, "E129.bottom", {"start": v(-27900, 13396.37) * mm, "end": v(-27000, 13396.37) * mm});
            skLineSegment(sketch, "E129.top", {"start": v(-27900, 12946.37) * mm, "end": v(-27000, 12946.37) * mm});
            skLineSegment(sketch, "E129.left", {"start": v(-27900, 13396.37) * mm, "end": v(-27900, 12946.37) * mm});
            skLineSegment(sketch, "E129.right", {"start": v(-27000, 13396.37) * mm, "end": v(-27000, 12946.37) * mm});
            skLineSegment(sketch, "E130.bottom", {"start": v(-29445.83, 13361.55) * mm, "end": v(-28945.83, 13361.55) * mm});
            skLineSegment(sketch, "E130.top", {"start": v(-29445.83, 12861.55) * mm, "end": v(-28945.83, 12861.55) * mm});
            skLineSegment(sketch, "E130.left", {"start": v(-29445.83, 13361.55) * mm, "end": v(-29445.83, 12861.55) * mm});
            skLineSegment(sketch, "E130.right", {"start": v(-28945.83, 13361.55) * mm, "end": v(-28945.83, 12861.55) * mm});
            skLineSegment(sketch, "E131.bottom", {"start": v(-33480.78, 12844.06) * mm, "end": v(-31080.78, 12844.06) * mm});
            skLineSegment(sketch, "E131.top", {"start": v(-33480.78, 12344.06) * mm, "end": v(-31080.78, 12344.06) * mm});
            skLineSegment(sketch, "E131.left", {"start": v(-33680.78, 12644.06) * mm, "end": v(-33680.78, 12544.06) * mm});
            skLineSegment(sketch, "E131.right", {"start": v(-30880.78, 12644.06) * mm, "end": v(-30880.78, 12544.06) * mm});
            skPoint(sketch, "E132.visualSharp", {"position": v(-33680.78, 12844.06) * mm});
            skArc(sketch, "E132.filletArc", {"start": v(-33480.78, 12844.06) * mm, "mid": v(-33622.2, 12785.48) * mm, "end": v(-33680.78, 12644.06) * mm});
            skPoint(sketch, "E133.visualSharp", {"position": v(-33680.78, 12344.06) * mm});
            skArc(sketch, "E133.filletArc", {"start": v(-33680.78, 12544.06) * mm, "mid": v(-33622.2, 12402.63) * mm, "end": v(-33480.78, 12344.06) * mm});
            skPoint(sketch, "E134.visualSharp", {"position": v(-30880.78, 12344.06) * mm});
            skArc(sketch, "E134.filletArc", {"start": v(-31080.78, 12344.06) * mm, "mid": v(-30939.36, 12402.63) * mm, "end": v(-30880.78, 12544.06) * mm});
            skPoint(sketch, "E135.visualSharp", {"position": v(-30880.78, 12844.06) * mm});
            skArc(sketch, "E135.filletArc", {"start": v(-30880.78, 12644.06) * mm, "mid": v(-30939.36, 12785.48) * mm, "end": v(-31080.78, 12844.06) * mm});
            skCircle(sketch, "E136", {"center": v(-33189.66, 13113.2) * mm, "radius": 186.7 * mm});
            skCircle(sketch, "E137.0.1.0", {"center": v(-33189.66, 12088.2) * mm, "radius": 186.7 * mm});
            skCircle(sketch, "E137.1.0.0", {"center": v(-32589.66, 13113.2) * mm, "radius": 186.7 * mm});
            skCircle(sketch, "E137.1.1.0", {"center": v(-32589.66, 12088.2) * mm, "radius": 186.7 * mm});
            skCircle(sketch, "E137.2.0.0", {"center": v(-31989.66, 13113.2) * mm, "radius": 186.7 * mm});
            skCircle(sketch, "E137.2.1.0", {"center": v(-31989.66, 12088.2) * mm, "radius": 186.7 * mm});
            skCircle(sketch, "E137.3.0.0", {"center": v(-31389.66, 13113.2) * mm, "radius": 186.7 * mm});
            skCircle(sketch, "E137.3.1.0", {"center": v(-31389.66, 12088.2) * mm, "radius": 186.7 * mm});
            skLineSegment(sketch, "E137.direction1", {"start": v(-33189.66, 13113.2) * mm, "end": v(-32589.66, 13113.2) * mm, "construction": true});
            skLineSegment(sketch, "E137.direction2", {"start": v(-33189.66, 13113.2) * mm, "end": v(-33189.66, 12088.2) * mm, "construction": true});
            skLineSegment(sketch, "E138.0", {"start": v(-20050.5, 11660.51) * mm, "end": v(-20050.5, 11460.51) * mm});
            skLineSegment(sketch, "E138.1", {"start": v(-20050.5, 11460.51) * mm, "end": v(-19850.5, 11460.51) * mm});
            skLineSegment(sketch, "E138.2", {"start": v(-19850.5, 11460.51) * mm, "end": v(-19850.5, 11360.51) * mm});
            skLineSegment(sketch, "E138.3", {"start": v(-20150.5, 11360.51) * mm, "end": v(-19850.5, 11360.51) * mm});
            skLineSegment(sketch, "E138.4", {"start": v(-20150.5, 11660.51) * mm, "end": v(-20150.5, 11360.51) * mm});
            skLineSegment(sketch, "E138.5", {"start": v(-20150.5, 11660.51) * mm, "end": v(-20050.5, 11660.51) * mm});
            skLineSegment(sketch, "E138.6", {"start": v(-20050.5, 12660.51) * mm, "end": v(-19850.5, 12660.51) * mm});
            skLineSegment(sketch, "E138.7", {"start": v(-20050.5, 12460.51) * mm, "end": v(-20050.5, 12660.51) * mm});
            skLineSegment(sketch, "E138.8", {"start": v(-20150.5, 12460.51) * mm, "end": v(-20050.5, 12460.51) * mm});
            skLineSegment(sketch, "E138.9", {"start": v(-20150.5, 12760.51) * mm, "end": v(-20150.5, 12460.51) * mm});
            skLineSegment(sketch, "E138.10", {"start": v(-20150.5, 12760.51) * mm, "end": v(-19850.5, 12760.51) * mm});
            skLineSegment(sketch, "E138.11", {"start": v(-19850.5, 12660.51) * mm, "end": v(-19850.5, 12760.51) * mm});
            skLineSegment(sketch, "E138.12", {"start": v(-19250.5, 12660.51) * mm, "end": v(-19450.5, 12660.51) * mm});
            skLineSegment(sketch, "E138.13", {"start": v(-19450.5, 12660.51) * mm, "end": v(-19450.5, 12760.51) * mm});
            skLineSegment(sketch, "E138.14", {"start": v(-19450.5, 12760.51) * mm, "end": v(-19150.5, 12760.51) * mm});
            skLineSegment(sketch, "E138.15", {"start": v(-19150.5, 12760.51) * mm, "end": v(-19150.5, 12460.51) * mm});
            skLineSegment(sketch, "E138.16", {"start": v(-19150.5, 12460.51) * mm, "end": v(-19250.5, 12460.51) * mm});
            skLineSegment(sketch, "E138.17", {"start": v(-19250.5, 12460.51) * mm, "end": v(-19250.5, 12660.51) * mm});
            skLineSegment(sketch, "E138.18", {"start": v(-19150.5, 11660.51) * mm, "end": v(-19250.5, 11660.51) * mm});
            skLineSegment(sketch, "E138.19", {"start": v(-19150.5, 11660.51) * mm, "end": v(-19150.5, 11360.51) * mm});
            skLineSegment(sketch, "E138.20", {"start": v(-19250.5, 11660.51) * mm, "end": v(-19250.5, 11460.51) * mm});
            skLineSegment(sketch, "E138.21", {"start": v(-19450.5, 11360.51) * mm, "end": v(-19150.5, 11360.51) * mm});
            skLineSegment(sketch, "E138.22", {"start": v(-19250.5, 11460.51) * mm, "end": v(-19450.5, 11460.51) * mm});
            skLineSegment(sketch, "E138.23", {"start": v(-19450.5, 11460.51) * mm, "end": v(-19450.5, 11360.51) * mm});
            skLineSegment(sketch, "E139.0", {"start": v(-27539.98, 12817.64) * mm, "end": v(-27739.98, 12817.64) * mm});
            skLineSegment(sketch, "E139.1", {"start": v(-27739.98, 12817.64) * mm, "end": v(-27739.98, 12617.64) * mm});
            skLineSegment(sketch, "E139.2", {"start": v(-27739.98, 12617.64) * mm, "end": v(-27839.98, 12617.64) * mm});
            skLineSegment(sketch, "E139.3", {"start": v(-27839.98, 12917.64) * mm, "end": v(-27839.98, 12617.64) * mm});
            skLineSegment(sketch, "E139.4", {"start": v(-27539.98, 12917.64) * mm, "end": v(-27839.98, 12917.64) * mm});
            skLineSegment(sketch, "E139.5", {"start": v(-27539.98, 12917.64) * mm, "end": v(-27539.98, 12817.64) * mm});
            skLineSegment(sketch, "E139.6", {"start": v(-26539.98, 12817.64) * mm, "end": v(-26539.98, 12617.64) * mm});
            skLineSegment(sketch, "E139.7", {"start": v(-26739.98, 12817.64) * mm, "end": v(-26539.98, 12817.64) * mm});
            skLineSegment(sketch, "E139.8", {"start": v(-26739.98, 12917.64) * mm, "end": v(-26739.98, 12817.64) * mm});
            skLineSegment(sketch, "E139.9", {"start": v(-26439.98, 12917.64) * mm, "end": v(-26739.98, 12917.64) * mm});
            skLineSegment(sketch, "E139.10", {"start": v(-26439.98, 12917.64) * mm, "end": v(-26439.98, 12617.64) * mm});
            skLineSegment(sketch, "E139.11", {"start": v(-26539.98, 12617.64) * mm, "end": v(-26439.98, 12617.64) * mm});
            skLineSegment(sketch, "E139.12", {"start": v(-26539.98, 12017.64) * mm, "end": v(-26539.98, 12217.64) * mm});
            skLineSegment(sketch, "E139.13", {"start": v(-26539.98, 12217.64) * mm, "end": v(-26439.98, 12217.64) * mm});
            skLineSegment(sketch, "E139.14", {"start": v(-26439.98, 12217.64) * mm, "end": v(-26439.98, 11917.64) * mm});
            skLineSegment(sketch, "E139.15", {"start": v(-26439.98, 11917.64) * mm, "end": v(-26739.98, 11917.64) * mm});
            skLineSegment(sketch, "E139.16", {"start": v(-26739.98, 11917.64) * mm, "end": v(-26739.98, 12017.64) * mm});
            skLineSegment(sketch, "E139.17", {"start": v(-26739.98, 12017.64) * mm, "end": v(-26539.98, 12017.64) * mm});
            skLineSegment(sketch, "E139.18", {"start": v(-27539.98, 11917.64) * mm, "end": v(-27539.98, 12017.64) * mm});
            skLineSegment(sketch, "E139.19", {"start": v(-27539.98, 11917.64) * mm, "end": v(-27839.98, 11917.64) * mm});
            skLineSegment(sketch, "E139.20", {"start": v(-27539.98, 12017.64) * mm, "end": v(-27739.98, 12017.64) * mm});
            skLineSegment(sketch, "E139.21", {"start": v(-27839.98, 12217.64) * mm, "end": v(-27839.98, 11917.64) * mm});
            skLineSegment(sketch, "E139.22", {"start": v(-27739.98, 12017.64) * mm, "end": v(-27739.98, 12217.64) * mm});
            skLineSegment(sketch, "E139.23", {"start": v(-27739.98, 12217.64) * mm, "end": v(-27839.98, 12217.64) * mm});
            skCircle(sketch, "E140.3.0.0", {"center": v(-26755.87, 11539.88) * mm, "radius": 186.7 * mm});
            skCircle(sketch, "E141.3.0.0", {"center": v(-25372.04, 10835.66) * mm, "radius": 186.7 * mm});
            skCircle(sketch, "E142.3.0.0", {"center": v(-23514.78, 11589.37) * mm, "radius": 186.7 * mm});
            skLineSegment(sketch, "E143.0", {"start": v(-24366.39, 12917.46) * mm, "end": v(-24566.39, 12917.46) * mm});
            skLineSegment(sketch, "E143.1", {"start": v(-24566.39, 12917.46) * mm, "end": v(-24566.39, 12717.46) * mm});
            skLineSegment(sketch, "E143.2", {"start": v(-24566.39, 12717.46) * mm, "end": v(-24666.39, 12717.46) * mm});
            skLineSegment(sketch, "E143.3", {"start": v(-24666.39, 13017.46) * mm, "end": v(-24666.39, 12717.46) * mm});
            skLineSegment(sketch, "E143.4", {"start": v(-24366.39, 13017.46) * mm, "end": v(-24666.39, 13017.46) * mm});
            skLineSegment(sketch, "E143.5", {"start": v(-24366.39, 13017.46) * mm, "end": v(-24366.39, 12917.46) * mm});
            skLineSegment(sketch, "E143.6", {"start": v(-23366.39, 12917.46) * mm, "end": v(-23366.39, 12717.46) * mm});
            skLineSegment(sketch, "E143.7", {"start": v(-23566.39, 12917.46) * mm, "end": v(-23366.39, 12917.46) * mm});
            skLineSegment(sketch, "E143.8", {"start": v(-23566.39, 13017.46) * mm, "end": v(-23566.39, 12917.46) * mm});
            skLineSegment(sketch, "E143.9", {"start": v(-23266.39, 13017.46) * mm, "end": v(-23566.39, 13017.46) * mm});
            skLineSegment(sketch, "E143.10", {"start": v(-23266.39, 13017.46) * mm, "end": v(-23266.39, 12717.46) * mm});
            skLineSegment(sketch, "E143.11", {"start": v(-23366.39, 12717.46) * mm, "end": v(-23266.39, 12717.46) * mm});
            skLineSegment(sketch, "E143.12", {"start": v(-23366.39, 12117.46) * mm, "end": v(-23366.39, 12317.46) * mm});
            skLineSegment(sketch, "E143.13", {"start": v(-23366.39, 12317.46) * mm, "end": v(-23266.39, 12317.46) * mm});
            skLineSegment(sketch, "E143.14", {"start": v(-23266.39, 12317.46) * mm, "end": v(-23266.39, 12017.46) * mm});
            skLineSegment(sketch, "E143.15", {"start": v(-23266.39, 12017.46) * mm, "end": v(-23566.39, 12017.46) * mm});
            skLineSegment(sketch, "E143.16", {"start": v(-23566.39, 12017.46) * mm, "end": v(-23566.39, 12117.46) * mm});
            skLineSegment(sketch, "E143.17", {"start": v(-23566.39, 12117.46) * mm, "end": v(-23366.39, 12117.46) * mm});
            skLineSegment(sketch, "E143.18", {"start": v(-24366.39, 12017.46) * mm, "end": v(-24366.39, 12117.46) * mm});
            skLineSegment(sketch, "E143.19", {"start": v(-24366.39, 12017.46) * mm, "end": v(-24666.39, 12017.46) * mm});
            skLineSegment(sketch, "E143.20", {"start": v(-24366.39, 12117.46) * mm, "end": v(-24566.39, 12117.46) * mm});
            skLineSegment(sketch, "E143.21", {"start": v(-24666.39, 12317.46) * mm, "end": v(-24666.39, 12017.46) * mm});
            skLineSegment(sketch, "E143.22", {"start": v(-24566.39, 12117.46) * mm, "end": v(-24566.39, 12317.46) * mm});
            skLineSegment(sketch, "E143.23", {"start": v(-24566.39, 12317.46) * mm, "end": v(-24666.39, 12317.46) * mm});
            skLineSegment(sketch, "E144.0", {"start": v(-21183.74, 11649.88) * mm, "end": v(-21183.74, 11449.88) * mm});
            skLineSegment(sketch, "E144.1", {"start": v(-21183.74, 11449.88) * mm, "end": v(-20983.74, 11449.88) * mm});
            skLineSegment(sketch, "E144.2", {"start": v(-20983.74, 11449.88) * mm, "end": v(-20983.74, 11349.88) * mm});
            skLineSegment(sketch, "E144.3", {"start": v(-21283.74, 11349.88) * mm, "end": v(-20983.74, 11349.88) * mm});
            skLineSegment(sketch, "E144.4", {"start": v(-21283.74, 11649.88) * mm, "end": v(-21283.74, 11349.88) * mm});
            skLineSegment(sketch, "E144.5", {"start": v(-21283.74, 11649.88) * mm, "end": v(-21183.74, 11649.88) * mm});
            skLineSegment(sketch, "E144.6", {"start": v(-21183.74, 12649.88) * mm, "end": v(-20983.74, 12649.88) * mm});
            skLineSegment(sketch, "E144.7", {"start": v(-21183.74, 12449.88) * mm, "end": v(-21183.74, 12649.88) * mm});
            skLineSegment(sketch, "E144.8", {"start": v(-21283.74, 12449.88) * mm, "end": v(-21183.74, 12449.88) * mm});
            skLineSegment(sketch, "E144.9", {"start": v(-21283.74, 12749.88) * mm, "end": v(-21283.74, 12449.88) * mm});
            skLineSegment(sketch, "E144.10", {"start": v(-21283.74, 12749.88) * mm, "end": v(-20983.74, 12749.88) * mm});
            skLineSegment(sketch, "E144.11", {"start": v(-20983.74, 12649.88) * mm, "end": v(-20983.74, 12749.88) * mm});
            skLineSegment(sketch, "E144.12", {"start": v(-20383.74, 12649.88) * mm, "end": v(-20583.74, 12649.88) * mm});
            skLineSegment(sketch, "E144.13", {"start": v(-20583.74, 12649.88) * mm, "end": v(-20583.74, 12749.88) * mm});
            skLineSegment(sketch, "E144.14", {"start": v(-20583.74, 12749.88) * mm, "end": v(-20283.74, 12749.88) * mm});
            skLineSegment(sketch, "E144.15", {"start": v(-20283.74, 12749.88) * mm, "end": v(-20283.74, 12449.88) * mm});
            skLineSegment(sketch, "E144.16", {"start": v(-20283.74, 12449.88) * mm, "end": v(-20383.74, 12449.88) * mm});
            skLineSegment(sketch, "E144.17", {"start": v(-20383.74, 12449.88) * mm, "end": v(-20383.74, 12649.88) * mm});
            skLineSegment(sketch, "E144.18", {"start": v(-20283.74, 11649.88) * mm, "end": v(-20383.74, 11649.88) * mm});
            skLineSegment(sketch, "E144.19", {"start": v(-20283.74, 11649.88) * mm, "end": v(-20283.74, 11349.88) * mm});
            skLineSegment(sketch, "E144.20", {"start": v(-20383.74, 11649.88) * mm, "end": v(-20383.74, 11449.88) * mm});
            skLineSegment(sketch, "E144.21", {"start": v(-20583.74, 11349.88) * mm, "end": v(-20283.74, 11349.88) * mm});
            skLineSegment(sketch, "E144.22", {"start": v(-20383.74, 11449.88) * mm, "end": v(-20583.74, 11449.88) * mm});
            skLineSegment(sketch, "E144.23", {"start": v(-20583.74, 11449.88) * mm, "end": v(-20583.74, 11349.88) * mm});
            skLineSegment(sketch, "E145.0", {"start": v(-23088.22, 11706.46) * mm, "end": v(-23088.22, 11506.46) * mm});
            skLineSegment(sketch, "E145.1", {"start": v(-23088.22, 11506.46) * mm, "end": v(-22888.22, 11506.46) * mm});
            skLineSegment(sketch, "E145.2", {"start": v(-22888.22, 11506.46) * mm, "end": v(-22888.22, 11406.46) * mm});
            skLineSegment(sketch, "E145.3", {"start": v(-23188.22, 11406.46) * mm, "end": v(-22888.22, 11406.46) * mm});
            skLineSegment(sketch, "E145.4", {"start": v(-23188.22, 11706.46) * mm, "end": v(-23188.22, 11406.46) * mm});
            skLineSegment(sketch, "E145.5", {"start": v(-23188.22, 11706.46) * mm, "end": v(-23088.22, 11706.46) * mm});
            skLineSegment(sketch, "E145.6", {"start": v(-23088.22, 12706.46) * mm, "end": v(-22888.22, 12706.46) * mm});
            skLineSegment(sketch, "E145.7", {"start": v(-23088.22, 12506.46) * mm, "end": v(-23088.22, 12706.46) * mm});
            skLineSegment(sketch, "E145.8", {"start": v(-23188.22, 12506.46) * mm, "end": v(-23088.22, 12506.46) * mm});
            skLineSegment(sketch, "E145.9", {"start": v(-23188.22, 12806.46) * mm, "end": v(-23188.22, 12506.46) * mm});
            skLineSegment(sketch, "E145.10", {"start": v(-23188.22, 12806.46) * mm, "end": v(-22888.22, 12806.46) * mm});
            skLineSegment(sketch, "E145.11", {"start": v(-22888.22, 12706.46) * mm, "end": v(-22888.22, 12806.46) * mm});
            skLineSegment(sketch, "E145.12", {"start": v(-22288.22, 12706.46) * mm, "end": v(-22488.22, 12706.46) * mm});
            skLineSegment(sketch, "E145.13", {"start": v(-22488.22, 12706.46) * mm, "end": v(-22488.22, 12806.46) * mm});
            skLineSegment(sketch, "E145.14", {"start": v(-22488.22, 12806.46) * mm, "end": v(-22188.22, 12806.46) * mm});
            skLineSegment(sketch, "E145.15", {"start": v(-22188.22, 12806.46) * mm, "end": v(-22188.22, 12506.46) * mm});
            skLineSegment(sketch, "E145.16", {"start": v(-22188.22, 12506.46) * mm, "end": v(-22288.22, 12506.46) * mm});
            skLineSegment(sketch, "E145.17", {"start": v(-22288.22, 12506.46) * mm, "end": v(-22288.22, 12706.46) * mm});
            skLineSegment(sketch, "E145.18", {"start": v(-22188.22, 11706.46) * mm, "end": v(-22288.22, 11706.46) * mm});
            skLineSegment(sketch, "E145.19", {"start": v(-22188.22, 11706.46) * mm, "end": v(-22188.22, 11406.46) * mm});
            skLineSegment(sketch, "E145.20", {"start": v(-22288.22, 11706.46) * mm, "end": v(-22288.22, 11506.46) * mm});
            skLineSegment(sketch, "E145.21", {"start": v(-22488.22, 11406.46) * mm, "end": v(-22188.22, 11406.46) * mm});
            skLineSegment(sketch, "E145.22", {"start": v(-22288.22, 11506.46) * mm, "end": v(-22488.22, 11506.46) * mm});
            skLineSegment(sketch, "E145.23", {"start": v(-22488.22, 11506.46) * mm, "end": v(-22488.22, 11406.46) * mm});
            skLineSegment(sketch, "E146", {"start": v(-25850.5, 13150) * mm, "end": v(-25850.5, 11150) * mm});
            skLineSegment(sketch, "E147", {"start": v(-25811.9, 11950) * mm, "end": v(-25811.9, 11150) * mm});
            skLineSegment(sketch, "E148.0", {"start": v(-24090.92, 10736.06) * mm, "end": v(-24090.92, 10936.06) * mm});
            skLineSegment(sketch, "E148.1", {"start": v(-24090.92, 10936.06) * mm, "end": v(-24290.92, 10936.06) * mm});
            skLineSegment(sketch, "E148.2", {"start": v(-24290.92, 10936.06) * mm, "end": v(-24290.92, 11036.06) * mm});
            skLineSegment(sketch, "E148.3", {"start": v(-23990.92, 11036.06) * mm, "end": v(-24290.92, 11036.06) * mm});
            skLineSegment(sketch, "E148.4", {"start": v(-23990.92, 10736.06) * mm, "end": v(-23990.92, 11036.06) * mm});
            skLineSegment(sketch, "E148.5", {"start": v(-23990.92, 10736.06) * mm, "end": v(-24090.92, 10736.06) * mm});
            skLineSegment(sketch, "E148.6", {"start": v(-24090.92, 9736.06) * mm, "end": v(-24290.92, 9736.06) * mm});
            skLineSegment(sketch, "E148.7", {"start": v(-24090.92, 9936.06) * mm, "end": v(-24090.92, 9736.06) * mm});
            skLineSegment(sketch, "E148.8", {"start": v(-23990.92, 9936.06) * mm, "end": v(-24090.92, 9936.06) * mm});
            skLineSegment(sketch, "E148.9", {"start": v(-23990.92, 9636.06) * mm, "end": v(-23990.92, 9936.06) * mm});
            skLineSegment(sketch, "E148.10", {"start": v(-23990.92, 9636.06) * mm, "end": v(-24290.92, 9636.06) * mm});
            skLineSegment(sketch, "E148.11", {"start": v(-24290.92, 9736.06) * mm, "end": v(-24290.92, 9636.06) * mm});
            skLineSegment(sketch, "E148.12", {"start": v(-24890.92, 9736.06) * mm, "end": v(-24690.92, 9736.06) * mm});
            skLineSegment(sketch, "E148.13", {"start": v(-24690.92, 9736.06) * mm, "end": v(-24690.92, 9636.06) * mm});
            skLineSegment(sketch, "E148.14", {"start": v(-24690.92, 9636.06) * mm, "end": v(-24990.92, 9636.06) * mm});
            skLineSegment(sketch, "E148.15", {"start": v(-24990.92, 9636.06) * mm, "end": v(-24990.92, 9936.06) * mm});
            skLineSegment(sketch, "E148.16", {"start": v(-24990.92, 9936.06) * mm, "end": v(-24890.92, 9936.06) * mm});
            skLineSegment(sketch, "E148.17", {"start": v(-24890.92, 9936.06) * mm, "end": v(-24890.92, 9736.06) * mm});
            skLineSegment(sketch, "E148.18", {"start": v(-24990.92, 10736.06) * mm, "end": v(-24890.92, 10736.06) * mm});
            skLineSegment(sketch, "E148.19", {"start": v(-24990.92, 10736.06) * mm, "end": v(-24990.92, 11036.06) * mm});
            skLineSegment(sketch, "E148.20", {"start": v(-24890.92, 10736.06) * mm, "end": v(-24890.92, 10936.06) * mm});
            skLineSegment(sketch, "E148.21", {"start": v(-24690.92, 11036.06) * mm, "end": v(-24990.92, 11036.06) * mm});
            skLineSegment(sketch, "E148.22", {"start": v(-24890.92, 10936.06) * mm, "end": v(-24690.92, 10936.06) * mm});
            skLineSegment(sketch, "E148.23", {"start": v(-24690.92, 10936.06) * mm, "end": v(-24690.92, 11036.06) * mm});
            skLineSegment(sketch, "E149.0", {"start": v(-22990.92, 10736.06) * mm, "end": v(-22990.92, 10936.06) * mm});
            skLineSegment(sketch, "E149.1", {"start": v(-22990.92, 10936.06) * mm, "end": v(-23190.92, 10936.06) * mm});
            skLineSegment(sketch, "E149.2", {"start": v(-23190.92, 10936.06) * mm, "end": v(-23190.92, 11036.06) * mm});
            skLineSegment(sketch, "E149.3", {"start": v(-22890.92, 11036.06) * mm, "end": v(-23190.92, 11036.06) * mm});
            skLineSegment(sketch, "E149.4", {"start": v(-22890.92, 10736.06) * mm, "end": v(-22890.92, 11036.06) * mm});
            skLineSegment(sketch, "E149.5", {"start": v(-22890.92, 10736.06) * mm, "end": v(-22990.92, 10736.06) * mm});
            skLineSegment(sketch, "E149.6", {"start": v(-22990.92, 9736.06) * mm, "end": v(-23190.92, 9736.06) * mm});
            skLineSegment(sketch, "E149.7", {"start": v(-22990.92, 9936.06) * mm, "end": v(-22990.92, 9736.06) * mm});
            skLineSegment(sketch, "E149.8", {"start": v(-22890.92, 9936.06) * mm, "end": v(-22990.92, 9936.06) * mm});
            skLineSegment(sketch, "E149.9", {"start": v(-22890.92, 9636.06) * mm, "end": v(-22890.92, 9936.06) * mm});
            skLineSegment(sketch, "E149.10", {"start": v(-22890.92, 9636.06) * mm, "end": v(-23190.92, 9636.06) * mm});
            skLineSegment(sketch, "E149.11", {"start": v(-23190.92, 9736.06) * mm, "end": v(-23190.92, 9636.06) * mm});
            skLineSegment(sketch, "E149.12", {"start": v(-23790.92, 9736.06) * mm, "end": v(-23590.92, 9736.06) * mm});
            skLineSegment(sketch, "E149.13", {"start": v(-23590.92, 9736.06) * mm, "end": v(-23590.92, 9636.06) * mm});
            skLineSegment(sketch, "E149.14", {"start": v(-23590.92, 9636.06) * mm, "end": v(-23890.92, 9636.06) * mm});
            skLineSegment(sketch, "E149.15", {"start": v(-23890.92, 9636.06) * mm, "end": v(-23890.92, 9936.06) * mm});
            skLineSegment(sketch, "E149.16", {"start": v(-23890.92, 9936.06) * mm, "end": v(-23790.92, 9936.06) * mm});
            skLineSegment(sketch, "E149.17", {"start": v(-23790.92, 9936.06) * mm, "end": v(-23790.92, 9736.06) * mm});
            skLineSegment(sketch, "E149.18", {"start": v(-23890.92, 10736.06) * mm, "end": v(-23790.92, 10736.06) * mm});
            skLineSegment(sketch, "E149.19", {"start": v(-23890.92, 10736.06) * mm, "end": v(-23890.92, 11036.06) * mm});
            skLineSegment(sketch, "E149.20", {"start": v(-23790.92, 10736.06) * mm, "end": v(-23790.92, 10936.06) * mm});
            skLineSegment(sketch, "E149.21", {"start": v(-23590.92, 11036.06) * mm, "end": v(-23890.92, 11036.06) * mm});
            skLineSegment(sketch, "E149.22", {"start": v(-23790.92, 10936.06) * mm, "end": v(-23590.92, 10936.06) * mm});
            skLineSegment(sketch, "E149.23", {"start": v(-23590.92, 10936.06) * mm, "end": v(-23590.92, 11036.06) * mm});
            skLineSegment(sketch, "E150.0", {"start": v(-26908.37, 10755.18) * mm, "end": v(-26908.37, 10955.18) * mm});
            skLineSegment(sketch, "E150.1", {"start": v(-26908.37, 10955.18) * mm, "end": v(-27108.37, 10955.18) * mm});
            skLineSegment(sketch, "E150.2", {"start": v(-27108.37, 10955.18) * mm, "end": v(-27108.37, 11055.18) * mm});
            skLineSegment(sketch, "E150.3", {"start": v(-26808.37, 11055.18) * mm, "end": v(-27108.37, 11055.18) * mm});
            skLineSegment(sketch, "E150.4", {"start": v(-26808.37, 10755.18) * mm, "end": v(-26808.37, 11055.18) * mm});
            skLineSegment(sketch, "E150.5", {"start": v(-26808.37, 10755.18) * mm, "end": v(-26908.37, 10755.18) * mm});
            skLineSegment(sketch, "E150.6", {"start": v(-26908.37, 9755.18) * mm, "end": v(-27108.37, 9755.18) * mm});
            skLineSegment(sketch, "E150.7", {"start": v(-26908.37, 9955.18) * mm, "end": v(-26908.37, 9755.18) * mm});
            skLineSegment(sketch, "E150.8", {"start": v(-26808.37, 9955.18) * mm, "end": v(-26908.37, 9955.18) * mm});
            skLineSegment(sketch, "E150.9", {"start": v(-26808.37, 9655.18) * mm, "end": v(-26808.37, 9955.18) * mm});
            skLineSegment(sketch, "E150.10", {"start": v(-26808.37, 9655.18) * mm, "end": v(-27108.37, 9655.18) * mm});
            skLineSegment(sketch, "E150.11", {"start": v(-27108.37, 9755.18) * mm, "end": v(-27108.37, 9655.18) * mm});
            skLineSegment(sketch, "E150.12", {"start": v(-27708.37, 9755.18) * mm, "end": v(-27508.37, 9755.18) * mm});
            skLineSegment(sketch, "E150.13", {"start": v(-27508.37, 9755.18) * mm, "end": v(-27508.37, 9655.18) * mm});
            skLineSegment(sketch, "E150.14", {"start": v(-27508.37, 9655.18) * mm, "end": v(-27808.37, 9655.18) * mm});
            skLineSegment(sketch, "E150.15", {"start": v(-27808.37, 9655.18) * mm, "end": v(-27808.37, 9955.18) * mm});
            skLineSegment(sketch, "E150.16", {"start": v(-27808.37, 9955.18) * mm, "end": v(-27708.37, 9955.18) * mm});
            skLineSegment(sketch, "E150.17", {"start": v(-27708.37, 9955.18) * mm, "end": v(-27708.37, 9755.18) * mm});
            skLineSegment(sketch, "E150.18", {"start": v(-27808.37, 10755.18) * mm, "end": v(-27708.37, 10755.18) * mm});
            skLineSegment(sketch, "E150.19", {"start": v(-27808.37, 10755.18) * mm, "end": v(-27808.37, 11055.18) * mm});
            skLineSegment(sketch, "E150.20", {"start": v(-27708.37, 10755.18) * mm, "end": v(-27708.37, 10955.18) * mm});
            skLineSegment(sketch, "E150.21", {"start": v(-27508.37, 11055.18) * mm, "end": v(-27808.37, 11055.18) * mm});
            skLineSegment(sketch, "E150.22", {"start": v(-27708.37, 10955.18) * mm, "end": v(-27508.37, 10955.18) * mm});
            skLineSegment(sketch, "E150.23", {"start": v(-27508.37, 10955.18) * mm, "end": v(-27508.37, 11055.18) * mm});
            skLineSegment(sketch, "E151.0", {"start": v(-25808.37, 10755.18) * mm, "end": v(-25808.37, 10955.18) * mm});
            skLineSegment(sketch, "E151.1", {"start": v(-25808.37, 10955.18) * mm, "end": v(-26008.37, 10955.18) * mm});
            skLineSegment(sketch, "E151.2", {"start": v(-26008.37, 10955.18) * mm, "end": v(-26008.37, 11055.18) * mm});
            skLineSegment(sketch, "E151.3", {"start": v(-25708.37, 11055.18) * mm, "end": v(-26008.37, 11055.18) * mm});
            skLineSegment(sketch, "E151.4", {"start": v(-25708.37, 10755.18) * mm, "end": v(-25708.37, 11055.18) * mm});
            skLineSegment(sketch, "E151.5", {"start": v(-25708.37, 10755.18) * mm, "end": v(-25808.37, 10755.18) * mm});
            skLineSegment(sketch, "E151.6", {"start": v(-25808.37, 9755.18) * mm, "end": v(-26008.37, 9755.18) * mm});
            skLineSegment(sketch, "E151.7", {"start": v(-25808.37, 9955.18) * mm, "end": v(-25808.37, 9755.18) * mm});
            skLineSegment(sketch, "E151.8", {"start": v(-25708.37, 9955.18) * mm, "end": v(-25808.37, 9955.18) * mm});
            skLineSegment(sketch, "E151.9", {"start": v(-25708.37, 9655.18) * mm, "end": v(-25708.37, 9955.18) * mm});
            skLineSegment(sketch, "E151.10", {"start": v(-25708.37, 9655.18) * mm, "end": v(-26008.37, 9655.18) * mm});
            skLineSegment(sketch, "E151.11", {"start": v(-26008.37, 9755.18) * mm, "end": v(-26008.37, 9655.18) * mm});
            skLineSegment(sketch, "E151.12", {"start": v(-26608.37, 9755.18) * mm, "end": v(-26408.37, 9755.18) * mm});
            skLineSegment(sketch, "E151.13", {"start": v(-26408.37, 9755.18) * mm, "end": v(-26408.37, 9655.18) * mm});
            skLineSegment(sketch, "E151.14", {"start": v(-26408.37, 9655.18) * mm, "end": v(-26708.37, 9655.18) * mm});
            skLineSegment(sketch, "E151.15", {"start": v(-26708.37, 9655.18) * mm, "end": v(-26708.37, 9955.18) * mm});
            skLineSegment(sketch, "E151.16", {"start": v(-26708.37, 9955.18) * mm, "end": v(-26608.37, 9955.18) * mm});
            skLineSegment(sketch, "E151.17", {"start": v(-26608.37, 9955.18) * mm, "end": v(-26608.37, 9755.18) * mm});
            skLineSegment(sketch, "E151.18", {"start": v(-26708.37, 10755.18) * mm, "end": v(-26608.37, 10755.18) * mm});
            skLineSegment(sketch, "E151.19", {"start": v(-26708.37, 10755.18) * mm, "end": v(-26708.37, 11055.18) * mm});
            skLineSegment(sketch, "E151.20", {"start": v(-26608.37, 10755.18) * mm, "end": v(-26608.37, 10955.18) * mm});
            skLineSegment(sketch, "E151.21", {"start": v(-26408.37, 11055.18) * mm, "end": v(-26708.37, 11055.18) * mm});
            skLineSegment(sketch, "E151.22", {"start": v(-26608.37, 10955.18) * mm, "end": v(-26408.37, 10955.18) * mm});
            skLineSegment(sketch, "E151.23", {"start": v(-26408.37, 10955.18) * mm, "end": v(-26408.37, 11055.18) * mm});
            skSolve(sketch);
        }
        {
            var Q0;
            Q0 = qSketchRegion(id + "F6", true);
            extrude(context, id + "F7", {"entities" : qUnion([Q0]), "depth" : 25 * mm});
        }
    });
